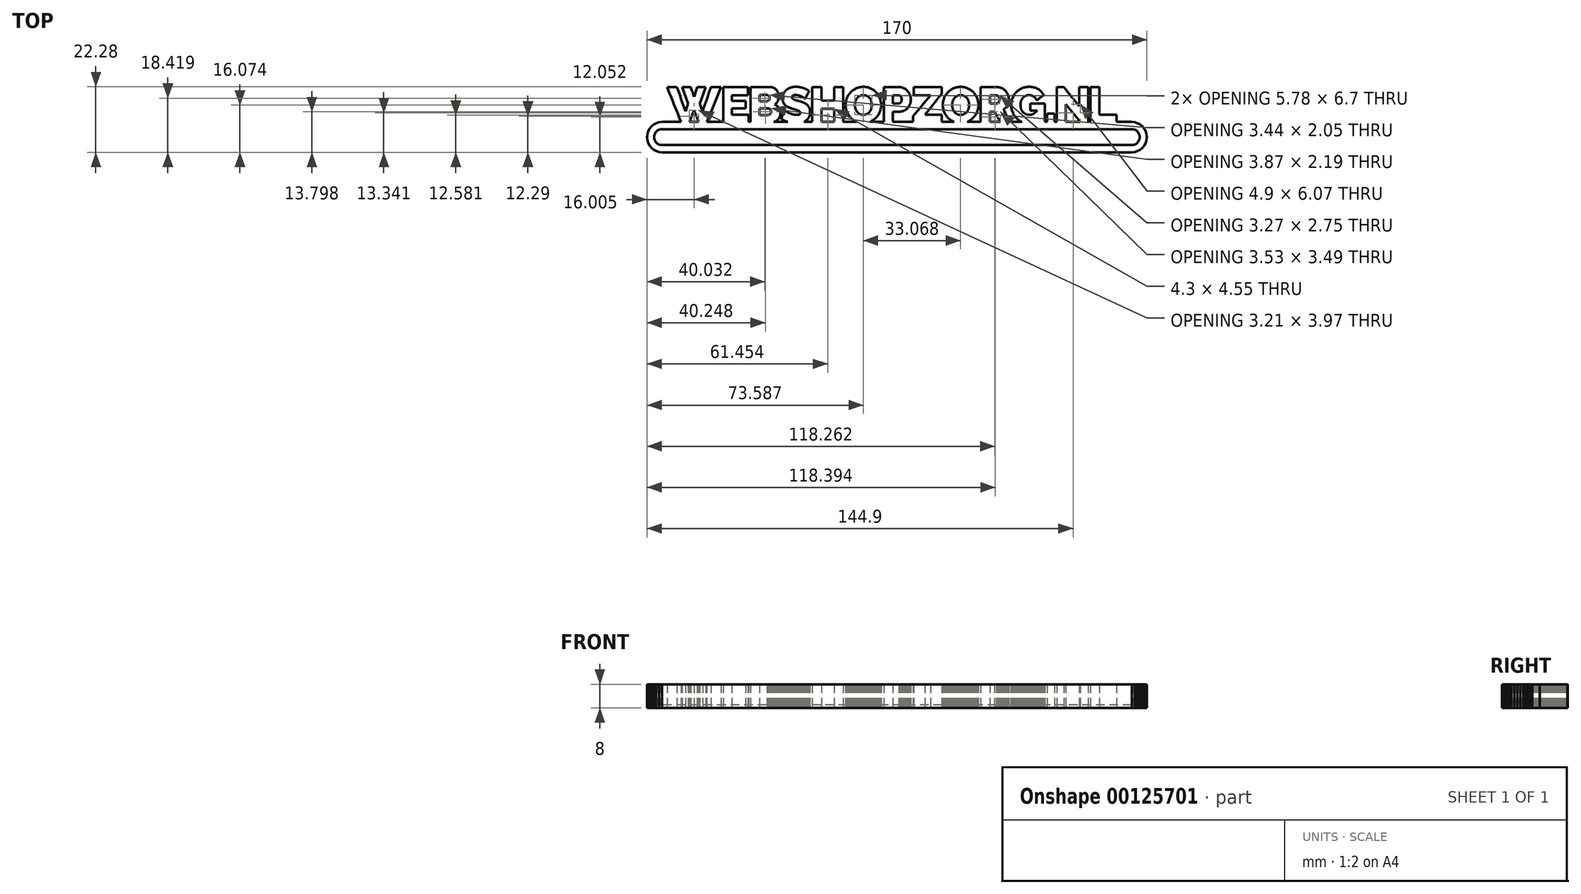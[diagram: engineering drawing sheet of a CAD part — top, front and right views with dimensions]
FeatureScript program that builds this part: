
annotation { "Feature Type Name" : "Feature", "Feature Type Description" : "" }
export const myFeature = defineFeature(function(context is Context, id is Id, definition is map)
    precondition{}
    {
        {
            var Q0;
            Q0=qCreatedBy(makeId("Top.planeOp"),FACE);
            var sketch = newSketch(context, id + "F0", { "sketchPlane" : qUnion([Q0])});
            skLineSegment(sketch, "E0", {"start": v(79.84, -0.83) * mm, "end": v(79.2, -0.83) * mm});
            skLineSegment(sketch, "E1", {"start": v(79.2, -0.83) * mm, "end": v(78.55, -0.83) * mm});
            skLineSegment(sketch, "E2", {"start": v(78.55, -0.83) * mm, "end": v(77.9, -0.83) * mm});
            skLineSegment(sketch, "E3", {"start": v(77.9, -0.83) * mm, "end": v(77.25, -0.83) * mm});
            skLineSegment(sketch, "E4", {"start": v(77.25, -0.83) * mm, "end": v(76.6, -0.83) * mm});
            skLineSegment(sketch, "E5", {"start": v(76.6, -0.83) * mm, "end": v(75.96, -0.83) * mm});
            skLineSegment(sketch, "E6", {"start": v(75.96, -0.83) * mm, "end": v(75.31, -0.83) * mm});
            skLineSegment(sketch, "E7", {"start": v(75.31, -0.83) * mm, "end": v(74.67, -0.83) * mm});
            skLineSegment(sketch, "E8", {"start": v(74.67, -0.83) * mm, "end": v(74.67, -0.53) * mm});
            skLineSegment(sketch, "E9", {"start": v(74.67, -0.53) * mm, "end": v(74.67, -0.22) * mm});
            skLineSegment(sketch, "E10", {"start": v(74.67, -0.22) * mm, "end": v(74.67, 0.1) * mm});
            skLineSegment(sketch, "E11", {"start": v(74.67, 0.1) * mm, "end": v(74.67, 0.4) * mm});
            skLineSegment(sketch, "E12", {"start": v(74.67, 0.4) * mm, "end": v(74.67, 0.7) * mm});
            skLineSegment(sketch, "E13", {"start": v(74.67, 0.7) * mm, "end": v(74.67, 1.02) * mm});
            skLineSegment(sketch, "E14", {"start": v(74.67, 1.02) * mm, "end": v(74.67, 1.33) * mm});
            skLineSegment(sketch, "E15", {"start": v(74.67, 1.33) * mm, "end": v(74.67, 1.63) * mm});
            skLineSegment(sketch, "E16", {"start": v(74.67, 1.63) * mm, "end": v(73.94, 1.63) * mm});
            skLineSegment(sketch, "E17", {"start": v(73.94, 1.63) * mm, "end": v(73.21, 1.63) * mm});
            skLineSegment(sketch, "E18", {"start": v(73.21, 1.63) * mm, "end": v(72.48, 1.63) * mm});
            skLineSegment(sketch, "E19", {"start": v(72.48, 1.63) * mm, "end": v(71.76, 1.63) * mm});
            skLineSegment(sketch, "E20", {"start": v(71.76, 1.63) * mm, "end": v(71.03, 1.63) * mm});
            skLineSegment(sketch, "E21", {"start": v(71.03, 1.63) * mm, "end": v(70.3, 1.63) * mm});
            skLineSegment(sketch, "E22", {"start": v(70.3, 1.63) * mm, "end": v(69.57, 1.63) * mm});
            skLineSegment(sketch, "E23", {"start": v(69.57, 1.63) * mm, "end": v(68.85, 1.63) * mm});
            skLineSegment(sketch, "E24", {"start": v(68.85, 1.63) * mm, "end": v(68.85, 2.8) * mm});
            skLineSegment(sketch, "E25", {"start": v(68.85, 2.8) * mm, "end": v(68.85, 3.98) * mm});
            skLineSegment(sketch, "E26", {"start": v(68.85, 3.98) * mm, "end": v(68.85, 5.15) * mm});
            skLineSegment(sketch, "E27", {"start": v(68.85, 5.15) * mm, "end": v(68.85, 6.33) * mm});
            skLineSegment(sketch, "E28", {"start": v(68.85, 6.33) * mm, "end": v(68.85, 7.5) * mm});
            skLineSegment(sketch, "E29", {"start": v(68.85, 7.5) * mm, "end": v(68.85, 8.67) * mm});
            skLineSegment(sketch, "E30", {"start": v(68.85, 8.67) * mm, "end": v(68.85, 9.85) * mm});
            skLineSegment(sketch, "E31", {"start": v(68.85, 9.85) * mm, "end": v(68.85, 11.02) * mm});
            skLineSegment(sketch, "E32", {"start": v(68.85, 11.02) * mm, "end": v(68.47, 11.02) * mm});
            skLineSegment(sketch, "E33", {"start": v(68.47, 11.02) * mm, "end": v(68.09, 11.02) * mm});
            skLineSegment(sketch, "E34", {"start": v(68.09, 11.02) * mm, "end": v(67.7, 11.02) * mm});
            skLineSegment(sketch, "E35", {"start": v(67.7, 11.02) * mm, "end": v(67.33, 11.02) * mm});
            skLineSegment(sketch, "E36", {"start": v(67.33, 11.02) * mm, "end": v(66.95, 11.02) * mm});
            skLineSegment(sketch, "E37", {"start": v(66.95, 11.02) * mm, "end": v(66.57, 11.02) * mm});
            skLineSegment(sketch, "E38", {"start": v(66.57, 11.02) * mm, "end": v(66.2, 11.02) * mm});
            skLineSegment(sketch, "E39", {"start": v(66.2, 11.02) * mm, "end": v(65.81, 11.02) * mm});
            skLineSegment(sketch, "E40", {"start": v(65.81, 11.02) * mm, "end": v(65.81, 9.54) * mm});
            skLineSegment(sketch, "E41", {"start": v(65.81, 9.54) * mm, "end": v(65.81, 8.06) * mm});
            skLineSegment(sketch, "E42", {"start": v(65.81, 8.06) * mm, "end": v(65.81, 6.57) * mm});
            skLineSegment(sketch, "E43", {"start": v(65.81, 6.57) * mm, "end": v(65.81, 5.1) * mm});
            skLineSegment(sketch, "E44", {"start": v(65.81, 5.1) * mm, "end": v(65.81, 3.61) * mm});
            skLineSegment(sketch, "E45", {"start": v(65.81, 3.61) * mm, "end": v(65.81, 2.13) * mm});
            skLineSegment(sketch, "E46", {"start": v(65.81, 2.13) * mm, "end": v(65.81, 0.65) * mm});
            skLineSegment(sketch, "E47", {"start": v(65.81, 0.65) * mm, "end": v(65.81, -0.83) * mm});
            skLineSegment(sketch, "E48", {"start": v(65.81, -0.83) * mm, "end": v(65.72, -0.83) * mm});
            skLineSegment(sketch, "E49", {"start": v(65.72, -0.83) * mm, "end": v(65.63, -0.83) * mm});
            skLineSegment(sketch, "E50", {"start": v(65.63, -0.83) * mm, "end": v(65.53, -0.83) * mm});
            skLineSegment(sketch, "E51", {"start": v(65.53, -0.83) * mm, "end": v(65.44, -0.83) * mm});
            skLineSegment(sketch, "E52", {"start": v(65.44, -0.83) * mm, "end": v(65.35, -0.83) * mm});
            skLineSegment(sketch, "E53", {"start": v(65.35, -0.83) * mm, "end": v(65.26, -0.83) * mm});
            skLineSegment(sketch, "E54", {"start": v(65.26, -0.83) * mm, "end": v(65.16, -0.83) * mm});
            skLineSegment(sketch, "E55", {"start": v(65.16, -0.83) * mm, "end": v(65.07, -0.83) * mm});
            skLineSegment(sketch, "E56", {"start": v(65.07, -0.83) * mm, "end": v(65.07, 0.65) * mm});
            skLineSegment(sketch, "E57", {"start": v(65.07, 0.65) * mm, "end": v(65.07, 2.13) * mm});
            skLineSegment(sketch, "E58", {"start": v(65.07, 2.13) * mm, "end": v(65.07, 3.61) * mm});
            skLineSegment(sketch, "E59", {"start": v(65.07, 3.61) * mm, "end": v(65.07, 5.1) * mm});
            skLineSegment(sketch, "E60", {"start": v(65.07, 5.1) * mm, "end": v(65.07, 6.57) * mm});
            skLineSegment(sketch, "E61", {"start": v(65.07, 6.57) * mm, "end": v(65.07, 8.06) * mm});
            skLineSegment(sketch, "E62", {"start": v(65.07, 8.06) * mm, "end": v(65.07, 9.54) * mm});
            skLineSegment(sketch, "E63", {"start": v(65.07, 9.54) * mm, "end": v(65.07, 11.02) * mm});
            skLineSegment(sketch, "E64", {"start": v(65.07, 11.02) * mm, "end": v(64.68, 11.02) * mm});
            skLineSegment(sketch, "E65", {"start": v(64.68, 11.02) * mm, "end": v(64.3, 11.02) * mm});
            skLineSegment(sketch, "E66", {"start": v(64.3, 11.02) * mm, "end": v(63.9, 11.02) * mm});
            skLineSegment(sketch, "E67", {"start": v(63.9, 11.02) * mm, "end": v(63.52, 11.02) * mm});
            skLineSegment(sketch, "E68", {"start": v(63.52, 11.02) * mm, "end": v(63.13, 11.02) * mm});
            skLineSegment(sketch, "E69", {"start": v(63.13, 11.02) * mm, "end": v(62.74, 11.02) * mm});
            skLineSegment(sketch, "E70", {"start": v(62.74, 11.02) * mm, "end": v(62.36, 11.02) * mm});
            skLineSegment(sketch, "E71", {"start": v(62.36, 11.02) * mm, "end": v(61.97, 11.02) * mm});
            skLineSegment(sketch, "E72", {"start": v(61.97, 11.02) * mm, "end": v(61.97, 10.2) * mm});
            skLineSegment(sketch, "E73", {"start": v(61.97, 10.2) * mm, "end": v(61.97, 9.39) * mm});
            skLineSegment(sketch, "E74", {"start": v(61.97, 9.39) * mm, "end": v(61.97, 8.57) * mm});
            skLineSegment(sketch, "E75", {"start": v(61.97, 8.57) * mm, "end": v(61.97, 7.75) * mm});
            skLineSegment(sketch, "E76", {"start": v(61.97, 7.75) * mm, "end": v(61.97, 6.94) * mm});
            skLineSegment(sketch, "E77", {"start": v(61.97, 6.94) * mm, "end": v(61.97, 6.12) * mm});
            skLineSegment(sketch, "E78", {"start": v(61.97, 6.12) * mm, "end": v(61.97, 5.3) * mm});
            skLineSegment(sketch, "E79", {"start": v(61.97, 5.3) * mm, "end": v(61.97, 4.49) * mm});
            skLineSegment(sketch, "E80", {"start": v(61.97, 4.49) * mm, "end": v(61.32, 5.3) * mm});
            skLineSegment(sketch, "E81", {"start": v(61.32, 5.3) * mm, "end": v(60.67, 6.12) * mm});
            skLineSegment(sketch, "E82", {"start": v(60.67, 6.12) * mm, "end": v(60.02, 6.94) * mm});
            skLineSegment(sketch, "E83", {"start": v(60.02, 6.94) * mm, "end": v(59.37, 7.75) * mm});
            skLineSegment(sketch, "E84", {"start": v(59.37, 7.75) * mm, "end": v(58.72, 8.57) * mm});
            skLineSegment(sketch, "E85", {"start": v(58.72, 8.57) * mm, "end": v(58.07, 9.39) * mm});
            skLineSegment(sketch, "E86", {"start": v(58.07, 9.39) * mm, "end": v(57.42, 10.2) * mm});
            skLineSegment(sketch, "E87", {"start": v(57.42, 10.2) * mm, "end": v(56.77, 11.02) * mm});
            skLineSegment(sketch, "E88", {"start": v(56.77, 11.02) * mm, "end": v(56.46, 11.02) * mm});
            skLineSegment(sketch, "E89", {"start": v(56.46, 11.02) * mm, "end": v(56.16, 11.02) * mm});
            skLineSegment(sketch, "E90", {"start": v(56.16, 11.02) * mm, "end": v(55.85, 11.02) * mm});
            skLineSegment(sketch, "E91", {"start": v(55.85, 11.02) * mm, "end": v(55.54, 11.02) * mm});
            skLineSegment(sketch, "E92", {"start": v(55.54, 11.02) * mm, "end": v(55.23, 11.02) * mm});
            skLineSegment(sketch, "E93", {"start": v(55.23, 11.02) * mm, "end": v(54.93, 11.02) * mm});
            skLineSegment(sketch, "E94", {"start": v(54.93, 11.02) * mm, "end": v(54.62, 11.02) * mm});
            skLineSegment(sketch, "E95", {"start": v(54.62, 11.02) * mm, "end": v(54.31, 11.02) * mm});
            skLineSegment(sketch, "E96", {"start": v(54.31, 11.02) * mm, "end": v(54.31, 9.54) * mm});
            skLineSegment(sketch, "E97", {"start": v(54.31, 9.54) * mm, "end": v(54.31, 8.06) * mm});
            skLineSegment(sketch, "E98", {"start": v(54.31, 8.06) * mm, "end": v(54.31, 6.57) * mm});
            skLineSegment(sketch, "E99", {"start": v(54.31, 6.57) * mm, "end": v(54.31, 5.1) * mm});
            skLineSegment(sketch, "E100", {"start": v(54.31, 5.1) * mm, "end": v(54.31, 3.61) * mm});
            skLineSegment(sketch, "E101", {"start": v(54.31, 3.61) * mm, "end": v(54.31, 2.13) * mm});
            skLineSegment(sketch, "E102", {"start": v(54.31, 2.13) * mm, "end": v(54.31, 0.65) * mm});
            skLineSegment(sketch, "E103", {"start": v(54.31, 0.65) * mm, "end": v(54.31, -0.83) * mm});
            skLineSegment(sketch, "E104", {"start": v(54.31, -0.83) * mm, "end": v(54.22, -0.83) * mm});
            skLineSegment(sketch, "E105", {"start": v(54.22, -0.83) * mm, "end": v(54.14, -0.83) * mm});
            skLineSegment(sketch, "E106", {"start": v(54.14, -0.83) * mm, "end": v(54.05, -0.83) * mm});
            skLineSegment(sketch, "E107", {"start": v(54.05, -0.83) * mm, "end": v(53.96, -0.83) * mm});
            skLineSegment(sketch, "E108", {"start": v(53.96, -0.83) * mm, "end": v(53.87, -0.83) * mm});
            skLineSegment(sketch, "E109", {"start": v(53.87, -0.83) * mm, "end": v(53.78, -0.83) * mm});
            skLineSegment(sketch, "E110", {"start": v(53.78, -0.83) * mm, "end": v(53.7, -0.83) * mm});
            skLineSegment(sketch, "E111", {"start": v(53.7, -0.83) * mm, "end": v(53.6, -0.83) * mm});
            skLineSegment(sketch, "E112", {"start": v(53.6, -0.83) * mm, "end": v(53.6, -0.48) * mm});
            skLineSegment(sketch, "E113", {"start": v(53.6, -0.48) * mm, "end": v(53.6, -0.12) * mm});
            skLineSegment(sketch, "E114", {"start": v(53.6, -0.12) * mm, "end": v(53.6, 0.24) * mm});
            skLineSegment(sketch, "E115", {"start": v(53.6, 0.24) * mm, "end": v(53.6, 0.6) * mm});
            skLineSegment(sketch, "E116", {"start": v(53.6, 0.6) * mm, "end": v(53.6, 0.95) * mm});
            skLineSegment(sketch, "E117", {"start": v(53.6, 0.95) * mm, "end": v(53.6, 1.3) * mm});
            skLineSegment(sketch, "E118", {"start": v(53.6, 1.3) * mm, "end": v(53.6, 1.67) * mm});
            skLineSegment(sketch, "E119", {"start": v(53.6, 1.67) * mm, "end": v(53.6, 2.02) * mm});
            skLineSegment(sketch, "E120", {"start": v(53.6, 2.02) * mm, "end": v(53.28, 2.02) * mm});
            skLineSegment(sketch, "E121", {"start": v(53.28, 2.02) * mm, "end": v(52.95, 2.02) * mm});
            skLineSegment(sketch, "E122", {"start": v(52.95, 2.02) * mm, "end": v(52.63, 2.02) * mm});
            skLineSegment(sketch, "E123", {"start": v(52.63, 2.02) * mm, "end": v(52.3, 2.02) * mm});
            skLineSegment(sketch, "E124", {"start": v(52.3, 2.02) * mm, "end": v(51.97, 2.02) * mm});
            skLineSegment(sketch, "E125", {"start": v(51.97, 2.02) * mm, "end": v(51.65, 2.02) * mm});
            skLineSegment(sketch, "E126", {"start": v(51.65, 2.02) * mm, "end": v(51.32, 2.02) * mm});
            skLineSegment(sketch, "E127", {"start": v(51.32, 2.02) * mm, "end": v(51, 2.02) * mm});
            skLineSegment(sketch, "E128", {"start": v(51, 2.02) * mm, "end": v(51, 1.67) * mm});
            skLineSegment(sketch, "E129", {"start": v(51, 1.67) * mm, "end": v(51, 1.3) * mm});
            skLineSegment(sketch, "E130", {"start": v(51, 1.3) * mm, "end": v(51, 0.95) * mm});
            skLineSegment(sketch, "E131", {"start": v(51, 0.95) * mm, "end": v(51, 0.6) * mm});
            skLineSegment(sketch, "E132", {"start": v(51, 0.6) * mm, "end": v(51, 0.24) * mm});
            skLineSegment(sketch, "E133", {"start": v(51, 0.24) * mm, "end": v(51, -0.12) * mm});
            skLineSegment(sketch, "E134", {"start": v(51, -0.12) * mm, "end": v(51, -0.48) * mm});
            skLineSegment(sketch, "E135", {"start": v(51, -0.48) * mm, "end": v(51, -0.83) * mm});
            skLineSegment(sketch, "E136", {"start": v(51, -0.83) * mm, "end": v(50.9, -0.83) * mm});
            skLineSegment(sketch, "E137", {"start": v(50.9, -0.83) * mm, "end": v(50.81, -0.83) * mm});
            skLineSegment(sketch, "E138", {"start": v(50.81, -0.83) * mm, "end": v(50.72, -0.83) * mm});
            skLineSegment(sketch, "E139", {"start": v(50.72, -0.83) * mm, "end": v(50.63, -0.83) * mm});
            skLineSegment(sketch, "E140", {"start": v(50.63, -0.83) * mm, "end": v(50.53, -0.83) * mm});
            skLineSegment(sketch, "E141", {"start": v(50.53, -0.83) * mm, "end": v(50.44, -0.83) * mm});
            skLineSegment(sketch, "E142", {"start": v(50.44, -0.83) * mm, "end": v(50.35, -0.83) * mm});
            skLineSegment(sketch, "E143", {"start": v(50.35, -0.83) * mm, "end": v(50.25, -0.83) * mm});
            skLineSegment(sketch, "E144", {"start": v(50.25, -0.83) * mm, "end": v(50.25, -0.05) * mm});
            skLineSegment(sketch, "E145", {"start": v(50.25, -0.05) * mm, "end": v(50.25, 0.73) * mm});
            skLineSegment(sketch, "E146", {"start": v(50.25, 0.73) * mm, "end": v(50.25, 1.5) * mm});
            skLineSegment(sketch, "E147", {"start": v(50.25, 1.5) * mm, "end": v(50.25, 2.29) * mm});
            skLineSegment(sketch, "E148", {"start": v(50.25, 2.29) * mm, "end": v(50.25, 3.07) * mm});
            skLineSegment(sketch, "E149", {"start": v(50.25, 3.07) * mm, "end": v(50.25, 3.85) * mm});
            skLineSegment(sketch, "E150", {"start": v(50.25, 3.85) * mm, "end": v(50.25, 4.63) * mm});
            skLineSegment(sketch, "E151", {"start": v(50.25, 4.63) * mm, "end": v(50.25, 5.4) * mm});
            skLineSegment(sketch, "E152", {"start": v(50.25, 5.4) * mm, "end": v(49.63, 5.4) * mm});
            skLineSegment(sketch, "E153", {"start": v(49.63, 5.4) * mm, "end": v(49.01, 5.4) * mm});
            skLineSegment(sketch, "E154", {"start": v(49.01, 5.4) * mm, "end": v(48.39, 5.4) * mm});
            skLineSegment(sketch, "E155", {"start": v(48.39, 5.4) * mm, "end": v(47.77, 5.4) * mm});
            skLineSegment(sketch, "E156", {"start": v(47.77, 5.4) * mm, "end": v(47.15, 5.4) * mm});
            skLineSegment(sketch, "E157", {"start": v(47.15, 5.4) * mm, "end": v(46.52, 5.4) * mm});
            skLineSegment(sketch, "E158", {"start": v(46.52, 5.4) * mm, "end": v(45.9, 5.4) * mm});
            skLineSegment(sketch, "E159", {"start": v(45.9, 5.4) * mm, "end": v(45.28, 5.4) * mm});
            skLineSegment(sketch, "E160", {"start": v(45.28, 5.4) * mm, "end": v(45.28, 5.1) * mm});
            skLineSegment(sketch, "E161", {"start": v(45.28, 5.1) * mm, "end": v(45.28, 4.8) * mm});
            skLineSegment(sketch, "E162", {"start": v(45.28, 4.8) * mm, "end": v(45.28, 4.5) * mm});
            skLineSegment(sketch, "E163", {"start": v(45.28, 4.5) * mm, "end": v(45.28, 4.21) * mm});
            skLineSegment(sketch, "E164", {"start": v(45.28, 4.21) * mm, "end": v(45.28, 3.91) * mm});
            skLineSegment(sketch, "E165", {"start": v(45.28, 3.91) * mm, "end": v(45.28, 3.61) * mm});
            skLineSegment(sketch, "E166", {"start": v(45.28, 3.61) * mm, "end": v(45.28, 3.31) * mm});
            skLineSegment(sketch, "E167", {"start": v(45.28, 3.31) * mm, "end": v(45.28, 3.01) * mm});
            skLineSegment(sketch, "E168", {"start": v(45.28, 3.01) * mm, "end": v(45.58, 3.01) * mm});
            skLineSegment(sketch, "E169", {"start": v(45.58, 3.01) * mm, "end": v(45.87, 3.01) * mm});
            skLineSegment(sketch, "E170", {"start": v(45.87, 3.01) * mm, "end": v(46.17, 3.01) * mm});
            skLineSegment(sketch, "E171", {"start": v(46.17, 3.01) * mm, "end": v(46.46, 3.01) * mm});
            skLineSegment(sketch, "E172", {"start": v(46.46, 3.01) * mm, "end": v(46.76, 3.01) * mm});
            skLineSegment(sketch, "E173", {"start": v(46.76, 3.01) * mm, "end": v(47.05, 3.01) * mm});
            skLineSegment(sketch, "E174", {"start": v(47.05, 3.01) * mm, "end": v(47.35, 3.01) * mm});
            skLineSegment(sketch, "E175", {"start": v(47.35, 3.01) * mm, "end": v(47.64, 3.01) * mm});
            skLineSegment(sketch, "E176", {"start": v(47.64, 3.01) * mm, "end": v(47.64, 3) * mm});
            skLineSegment(sketch, "E177", {"start": v(47.64, 3) * mm, "end": v(47.64, 3) * mm});
            skLineSegment(sketch, "E178", {"start": v(47.64, 3) * mm, "end": v(47.64, 2.99) * mm});
            skLineSegment(sketch, "E179", {"start": v(47.64, 2.99) * mm, "end": v(47.64, 2.98) * mm});
            skLineSegment(sketch, "E180", {"start": v(47.64, 2.98) * mm, "end": v(47.64, 2.97) * mm});
            skLineSegment(sketch, "E181", {"start": v(47.64, 2.97) * mm, "end": v(47.64, 2.97) * mm});
            skLineSegment(sketch, "E182", {"start": v(47.64, 2.97) * mm, "end": v(47.64, 2.96) * mm});
            skLineSegment(sketch, "E183", {"start": v(47.64, 2.96) * mm, "end": v(47.64, 2.95) * mm});
            skLineSegment(sketch, "E184", {"start": v(47.64, 2.95) * mm, "end": v(47.33, 2.63) * mm});
            skLineSegment(sketch, "E185", {"start": v(47.33, 2.63) * mm, "end": v(47, 2.36) * mm});
            skLineSegment(sketch, "E186", {"start": v(47, 2.36) * mm, "end": v(46.68, 2.12) * mm});
            skLineSegment(sketch, "E187", {"start": v(46.68, 2.12) * mm, "end": v(46.36, 1.93) * mm});
            skLineSegment(sketch, "E188", {"start": v(46.36, 1.93) * mm, "end": v(46.02, 1.79) * mm});
            skLineSegment(sketch, "E189", {"start": v(46.02, 1.79) * mm, "end": v(45.68, 1.68) * mm});
            skLineSegment(sketch, "E190", {"start": v(45.68, 1.68) * mm, "end": v(45.32, 1.62) * mm});
            skLineSegment(sketch, "E191", {"start": v(45.32, 1.62) * mm, "end": v(44.96, 1.6) * mm});
            skLineSegment(sketch, "E192", {"start": v(44.96, 1.6) * mm, "end": v(44.8, 1.6) * mm});
            skLineSegment(sketch, "E193", {"start": v(44.8, 1.6) * mm, "end": v(44.64, 1.61) * mm});
            skLineSegment(sketch, "E194", {"start": v(44.64, 1.61) * mm, "end": v(44.48, 1.63) * mm});
            skLineSegment(sketch, "E195", {"start": v(44.48, 1.63) * mm, "end": v(44.33, 1.66) * mm});
            skLineSegment(sketch, "E196", {"start": v(44.33, 1.66) * mm, "end": v(44.18, 1.7) * mm});
            skLineSegment(sketch, "E197", {"start": v(44.18, 1.7) * mm, "end": v(44.04, 1.74) * mm});
            skLineSegment(sketch, "E198", {"start": v(44.04, 1.74) * mm, "end": v(43.9, 1.79) * mm});
            skLineSegment(sketch, "E199", {"start": v(43.9, 1.79) * mm, "end": v(43.76, 1.85) * mm});
            skLineSegment(sketch, "E200", {"start": v(43.76, 1.85) * mm, "end": v(43.63, 1.91) * mm});
            skLineSegment(sketch, "E201", {"start": v(43.63, 1.91) * mm, "end": v(43.5, 1.98) * mm});
            skLineSegment(sketch, "E202", {"start": v(43.5, 1.98) * mm, "end": v(43.38, 2.06) * mm});
            skLineSegment(sketch, "E203", {"start": v(43.38, 2.06) * mm, "end": v(43.26, 2.14) * mm});
            skLineSegment(sketch, "E204", {"start": v(43.26, 2.14) * mm, "end": v(43.15, 2.23) * mm});
            skLineSegment(sketch, "E205", {"start": v(43.15, 2.23) * mm, "end": v(43.04, 2.33) * mm});
            skLineSegment(sketch, "E206", {"start": v(43.04, 2.33) * mm, "end": v(42.94, 2.43) * mm});
            skLineSegment(sketch, "E207", {"start": v(42.94, 2.43) * mm, "end": v(42.84, 2.53) * mm});
            skLineSegment(sketch, "E208", {"start": v(42.84, 2.53) * mm, "end": v(42.74, 2.65) * mm});
            skLineSegment(sketch, "E209", {"start": v(42.74, 2.65) * mm, "end": v(42.65, 2.77) * mm});
            skLineSegment(sketch, "E210", {"start": v(42.65, 2.77) * mm, "end": v(42.57, 2.9) * mm});
            skLineSegment(sketch, "E211", {"start": v(42.57, 2.9) * mm, "end": v(42.5, 3.02) * mm});
            skLineSegment(sketch, "E212", {"start": v(42.5, 3.02) * mm, "end": v(42.42, 3.16) * mm});
            skLineSegment(sketch, "E213", {"start": v(42.42, 3.16) * mm, "end": v(42.35, 3.3) * mm});
            skLineSegment(sketch, "E214", {"start": v(42.35, 3.3) * mm, "end": v(42.28, 3.44) * mm});
            skLineSegment(sketch, "E215", {"start": v(42.28, 3.44) * mm, "end": v(42.23, 3.6) * mm});
            skLineSegment(sketch, "E216", {"start": v(42.23, 3.6) * mm, "end": v(42.18, 3.75) * mm});
            skLineSegment(sketch, "E217", {"start": v(42.18, 3.75) * mm, "end": v(42.13, 3.9) * mm});
            skLineSegment(sketch, "E218", {"start": v(42.13, 3.9) * mm, "end": v(42.1, 4.07) * mm});
            skLineSegment(sketch, "E219", {"start": v(42.1, 4.07) * mm, "end": v(42.06, 4.23) * mm});
            skLineSegment(sketch, "E220", {"start": v(42.06, 4.23) * mm, "end": v(42.04, 4.4) * mm});
            skLineSegment(sketch, "E221", {"start": v(42.04, 4.4) * mm, "end": v(42.02, 4.58) * mm});
            skLineSegment(sketch, "E222", {"start": v(42.02, 4.58) * mm, "end": v(42, 4.75) * mm});
            skLineSegment(sketch, "E223", {"start": v(42, 4.75) * mm, "end": v(42, 4.93) * mm});
            skLineSegment(sketch, "E224", {"start": v(42, 4.93) * mm, "end": v(42, 5.11) * mm});
            skLineSegment(sketch, "E225", {"start": v(42, 5.11) * mm, "end": v(42.02, 5.28) * mm});
            skLineSegment(sketch, "E226", {"start": v(42.02, 5.28) * mm, "end": v(42.03, 5.46) * mm});
            skLineSegment(sketch, "E227", {"start": v(42.03, 5.46) * mm, "end": v(42.06, 5.62) * mm});
            skLineSegment(sketch, "E228", {"start": v(42.06, 5.62) * mm, "end": v(42.09, 5.79) * mm});
            skLineSegment(sketch, "E229", {"start": v(42.09, 5.79) * mm, "end": v(42.12, 5.95) * mm});
            skLineSegment(sketch, "E230", {"start": v(42.12, 5.95) * mm, "end": v(42.16, 6.1) * mm});
            skLineSegment(sketch, "E231", {"start": v(42.16, 6.1) * mm, "end": v(42.21, 6.26) * mm});
            skLineSegment(sketch, "E232", {"start": v(42.21, 6.26) * mm, "end": v(42.26, 6.42) * mm});
            skLineSegment(sketch, "E233", {"start": v(42.26, 6.42) * mm, "end": v(42.32, 6.56) * mm});
            skLineSegment(sketch, "E234", {"start": v(42.32, 6.56) * mm, "end": v(42.39, 6.7) * mm});
            skLineSegment(sketch, "E235", {"start": v(42.39, 6.7) * mm, "end": v(42.46, 6.84) * mm});
            skLineSegment(sketch, "E236", {"start": v(42.46, 6.84) * mm, "end": v(42.53, 6.97) * mm});
            skLineSegment(sketch, "E237", {"start": v(42.53, 6.97) * mm, "end": v(42.61, 7.1) * mm});
            skLineSegment(sketch, "E238", {"start": v(42.61, 7.1) * mm, "end": v(42.7, 7.22) * mm});
            skLineSegment(sketch, "E239", {"start": v(42.7, 7.22) * mm, "end": v(42.79, 7.34) * mm});
            skLineSegment(sketch, "E240", {"start": v(42.79, 7.34) * mm, "end": v(42.88, 7.45) * mm});
            skLineSegment(sketch, "E241", {"start": v(42.88, 7.45) * mm, "end": v(42.98, 7.55) * mm});
            skLineSegment(sketch, "E242", {"start": v(42.98, 7.55) * mm, "end": v(43.09, 7.65) * mm});
            skLineSegment(sketch, "E243", {"start": v(43.09, 7.65) * mm, "end": v(43.2, 7.74) * mm});
            skLineSegment(sketch, "E244", {"start": v(43.2, 7.74) * mm, "end": v(43.31, 7.83) * mm});
            skLineSegment(sketch, "E245", {"start": v(43.31, 7.83) * mm, "end": v(43.43, 7.9) * mm});
            skLineSegment(sketch, "E246", {"start": v(43.43, 7.9) * mm, "end": v(43.55, 7.98) * mm});
            skLineSegment(sketch, "E247", {"start": v(43.55, 7.98) * mm, "end": v(43.68, 8.05) * mm});
            skLineSegment(sketch, "E248", {"start": v(43.68, 8.05) * mm, "end": v(43.8, 8.1) * mm});
            skLineSegment(sketch, "E249", {"start": v(43.8, 8.1) * mm, "end": v(43.94, 8.16) * mm});
            skLineSegment(sketch, "E250", {"start": v(43.94, 8.16) * mm, "end": v(44.08, 8.2) * mm});
            skLineSegment(sketch, "E251", {"start": v(44.08, 8.2) * mm, "end": v(44.22, 8.24) * mm});
            skLineSegment(sketch, "E252", {"start": v(44.22, 8.24) * mm, "end": v(44.37, 8.27) * mm});
            skLineSegment(sketch, "E253", {"start": v(44.37, 8.27) * mm, "end": v(44.52, 8.29) * mm});
            skLineSegment(sketch, "E254", {"start": v(44.52, 8.29) * mm, "end": v(44.67, 8.3) * mm});
            skLineSegment(sketch, "E255", {"start": v(44.67, 8.3) * mm, "end": v(44.83, 8.3) * mm});
            skLineSegment(sketch, "E256", {"start": v(44.83, 8.3) * mm, "end": v(45.03, 8.3) * mm});
            skLineSegment(sketch, "E257", {"start": v(45.03, 8.3) * mm, "end": v(45.23, 8.28) * mm});
            skLineSegment(sketch, "E258", {"start": v(45.23, 8.28) * mm, "end": v(45.43, 8.24) * mm});
            skLineSegment(sketch, "E259", {"start": v(45.43, 8.24) * mm, "end": v(45.62, 8.2) * mm});
            skLineSegment(sketch, "E260", {"start": v(45.62, 8.2) * mm, "end": v(45.81, 8.14) * mm});
            skLineSegment(sketch, "E261", {"start": v(45.81, 8.14) * mm, "end": v(46, 8.07) * mm});
            skLineSegment(sketch, "E262", {"start": v(46, 8.07) * mm, "end": v(46.18, 7.99) * mm});
            skLineSegment(sketch, "E263", {"start": v(46.18, 7.99) * mm, "end": v(46.36, 7.9) * mm});
            skLineSegment(sketch, "E264", {"start": v(46.36, 7.9) * mm, "end": v(46.53, 7.78) * mm});
            skLineSegment(sketch, "E265", {"start": v(46.53, 7.78) * mm, "end": v(46.7, 7.66) * mm});
            skLineSegment(sketch, "E266", {"start": v(46.7, 7.66) * mm, "end": v(46.84, 7.54) * mm});
            skLineSegment(sketch, "E267", {"start": v(46.84, 7.54) * mm, "end": v(46.98, 7.4) * mm});
            skLineSegment(sketch, "E268", {"start": v(46.98, 7.4) * mm, "end": v(47.11, 7.25) * mm});
            skLineSegment(sketch, "E269", {"start": v(47.11, 7.25) * mm, "end": v(47.23, 7.09) * mm});
            skLineSegment(sketch, "E270", {"start": v(47.23, 7.09) * mm, "end": v(47.34, 6.92) * mm});
            skLineSegment(sketch, "E271", {"start": v(47.34, 6.92) * mm, "end": v(47.44, 6.74) * mm});
            skLineSegment(sketch, "E272", {"start": v(47.44, 6.74) * mm, "end": v(47.45, 6.7) * mm});
            skLineSegment(sketch, "E273", {"start": v(47.45, 6.7) * mm, "end": v(47.46, 6.68) * mm});
            skLineSegment(sketch, "E274", {"start": v(47.46, 6.68) * mm, "end": v(47.48, 6.66) * mm});
            skLineSegment(sketch, "E275", {"start": v(47.48, 6.66) * mm, "end": v(47.49, 6.63) * mm});
            skLineSegment(sketch, "E276", {"start": v(47.49, 6.63) * mm, "end": v(47.5, 6.6) * mm});
            skLineSegment(sketch, "E277", {"start": v(47.5, 6.6) * mm, "end": v(47.52, 6.58) * mm});
            skLineSegment(sketch, "E278", {"start": v(47.52, 6.58) * mm, "end": v(47.53, 6.55) * mm});
            skLineSegment(sketch, "E279", {"start": v(47.53, 6.55) * mm, "end": v(47.54, 6.52) * mm});
            skLineSegment(sketch, "E280", {"start": v(47.54, 6.52) * mm, "end": v(47.84, 6.75) * mm});
            skLineSegment(sketch, "E281", {"start": v(47.84, 6.75) * mm, "end": v(48.13, 6.97) * mm});
            skLineSegment(sketch, "E282", {"start": v(48.13, 6.97) * mm, "end": v(48.42, 7.19) * mm});
            skLineSegment(sketch, "E283", {"start": v(48.42, 7.19) * mm, "end": v(48.71, 7.4) * mm});
            skLineSegment(sketch, "E284", {"start": v(48.71, 7.4) * mm, "end": v(49, 7.63) * mm});
            skLineSegment(sketch, "E285", {"start": v(49, 7.63) * mm, "end": v(49.3, 7.85) * mm});
            skLineSegment(sketch, "E286", {"start": v(49.3, 7.85) * mm, "end": v(49.6, 8.07) * mm});
            skLineSegment(sketch, "E287", {"start": v(49.6, 8.07) * mm, "end": v(49.89, 8.3) * mm});
            skLineSegment(sketch, "E288", {"start": v(49.89, 8.3) * mm, "end": v(49.88, 8.31) * mm});
            skLineSegment(sketch, "E289", {"start": v(49.88, 8.31) * mm, "end": v(49.87, 8.33) * mm});
            skLineSegment(sketch, "E290", {"start": v(49.87, 8.33) * mm, "end": v(49.86, 8.35) * mm});
            skLineSegment(sketch, "E291", {"start": v(49.86, 8.35) * mm, "end": v(49.85, 8.37) * mm});
            skLineSegment(sketch, "E292", {"start": v(49.85, 8.37) * mm, "end": v(49.84, 8.39) * mm});
            skLineSegment(sketch, "E293", {"start": v(49.84, 8.39) * mm, "end": v(49.83, 8.4) * mm});
            skLineSegment(sketch, "E294", {"start": v(49.83, 8.4) * mm, "end": v(49.82, 8.42) * mm});
            skLineSegment(sketch, "E295", {"start": v(49.82, 8.42) * mm, "end": v(49.81, 8.44) * mm});
            skLineSegment(sketch, "E296", {"start": v(49.81, 8.44) * mm, "end": v(49.64, 8.74) * mm});
            skLineSegment(sketch, "E297", {"start": v(49.64, 8.74) * mm, "end": v(49.45, 9.03) * mm});
            skLineSegment(sketch, "E298", {"start": v(49.45, 9.03) * mm, "end": v(49.24, 9.3) * mm});
            skLineSegment(sketch, "E299", {"start": v(49.24, 9.3) * mm, "end": v(49.01, 9.56) * mm});
            skLineSegment(sketch, "E300", {"start": v(49.01, 9.56) * mm, "end": v(48.76, 9.8) * mm});
            skLineSegment(sketch, "E301", {"start": v(48.76, 9.8) * mm, "end": v(48.49, 10.01) * mm});
            skLineSegment(sketch, "E302", {"start": v(48.49, 10.01) * mm, "end": v(48.2, 10.22) * mm});
            skLineSegment(sketch, "E303", {"start": v(48.2, 10.22) * mm, "end": v(47.9, 10.4) * mm});
            skLineSegment(sketch, "E304", {"start": v(47.9, 10.4) * mm, "end": v(47.57, 10.57) * mm});
            skLineSegment(sketch, "E305", {"start": v(47.57, 10.57) * mm, "end": v(47.23, 10.72) * mm});
            skLineSegment(sketch, "E306", {"start": v(47.23, 10.72) * mm, "end": v(46.88, 10.84) * mm});
            skLineSegment(sketch, "E307", {"start": v(46.88, 10.84) * mm, "end": v(46.51, 10.94) * mm});
            skLineSegment(sketch, "E308", {"start": v(46.51, 10.94) * mm, "end": v(46.13, 11.02) * mm});
            skLineSegment(sketch, "E309", {"start": v(46.13, 11.02) * mm, "end": v(45.74, 11.07) * mm});
            skLineSegment(sketch, "E310", {"start": v(45.74, 11.07) * mm, "end": v(45.34, 11.1) * mm});
            skLineSegment(sketch, "E311", {"start": v(45.34, 11.1) * mm, "end": v(44.93, 11.12) * mm});
            skLineSegment(sketch, "E312", {"start": v(44.93, 11.12) * mm, "end": v(44.6, 11.11) * mm});
            skLineSegment(sketch, "E313", {"start": v(44.6, 11.11) * mm, "end": v(44.3, 11.09) * mm});
            skLineSegment(sketch, "E314", {"start": v(44.3, 11.09) * mm, "end": v(43.99, 11.05) * mm});
            skLineSegment(sketch, "E315", {"start": v(43.99, 11.05) * mm, "end": v(43.68, 11) * mm});
            skLineSegment(sketch, "E316", {"start": v(43.68, 11) * mm, "end": v(43.39, 10.93) * mm});
            skLineSegment(sketch, "E317", {"start": v(43.39, 10.93) * mm, "end": v(43.1, 10.85) * mm});
            skLineSegment(sketch, "E318", {"start": v(43.1, 10.85) * mm, "end": v(42.8, 10.75) * mm});
            skLineSegment(sketch, "E319", {"start": v(42.8, 10.75) * mm, "end": v(42.53, 10.64) * mm});
            skLineSegment(sketch, "E320", {"start": v(42.53, 10.64) * mm, "end": v(42.25, 10.51) * mm});
            skLineSegment(sketch, "E321", {"start": v(42.25, 10.51) * mm, "end": v(41.99, 10.38) * mm});
            skLineSegment(sketch, "E322", {"start": v(41.99, 10.38) * mm, "end": v(41.73, 10.23) * mm});
            skLineSegment(sketch, "E323", {"start": v(41.73, 10.23) * mm, "end": v(41.49, 10.07) * mm});
            skLineSegment(sketch, "E324", {"start": v(41.49, 10.07) * mm, "end": v(41.25, 9.9) * mm});
            skLineSegment(sketch, "E325", {"start": v(41.25, 9.9) * mm, "end": v(41.02, 9.73) * mm});
            skLineSegment(sketch, "E326", {"start": v(41.02, 9.73) * mm, "end": v(40.8, 9.54) * mm});
            skLineSegment(sketch, "E327", {"start": v(40.8, 9.54) * mm, "end": v(40.6, 9.34) * mm});
            skLineSegment(sketch, "E328", {"start": v(40.6, 9.34) * mm, "end": v(40.4, 9.13) * mm});
            skLineSegment(sketch, "E329", {"start": v(40.4, 9.13) * mm, "end": v(40.21, 8.9) * mm});
            skLineSegment(sketch, "E330", {"start": v(40.21, 8.9) * mm, "end": v(40.04, 8.68) * mm});
            skLineSegment(sketch, "E331", {"start": v(40.04, 8.68) * mm, "end": v(39.87, 8.44) * mm});
            skLineSegment(sketch, "E332", {"start": v(39.87, 8.44) * mm, "end": v(39.72, 8.2) * mm});
            skLineSegment(sketch, "E333", {"start": v(39.72, 8.2) * mm, "end": v(39.57, 7.94) * mm});
            skLineSegment(sketch, "E334", {"start": v(39.57, 7.94) * mm, "end": v(39.44, 7.67) * mm});
            skLineSegment(sketch, "E335", {"start": v(39.44, 7.67) * mm, "end": v(39.32, 7.4) * mm});
            skLineSegment(sketch, "E336", {"start": v(39.32, 7.4) * mm, "end": v(39.21, 7.12) * mm});
            skLineSegment(sketch, "E337", {"start": v(39.21, 7.12) * mm, "end": v(39.12, 6.83) * mm});
            skLineSegment(sketch, "E338", {"start": v(39.12, 6.83) * mm, "end": v(39.04, 6.54) * mm});
            skLineSegment(sketch, "E339", {"start": v(39.04, 6.54) * mm, "end": v(38.97, 6.25) * mm});
            skLineSegment(sketch, "E340", {"start": v(38.97, 6.25) * mm, "end": v(38.92, 5.95) * mm});
            skLineSegment(sketch, "E341", {"start": v(38.92, 5.95) * mm, "end": v(38.89, 5.65) * mm});
            skLineSegment(sketch, "E342", {"start": v(38.89, 5.65) * mm, "end": v(38.86, 5.34) * mm});
            skLineSegment(sketch, "E343", {"start": v(38.86, 5.34) * mm, "end": v(38.86, 5.03) * mm});
            skLineSegment(sketch, "E344", {"start": v(38.86, 5.03) * mm, "end": v(38.86, 4.7) * mm});
            skLineSegment(sketch, "E345", {"start": v(38.86, 4.7) * mm, "end": v(38.89, 4.36) * mm});
            skLineSegment(sketch, "E346", {"start": v(38.89, 4.36) * mm, "end": v(38.92, 4.03) * mm});
            skLineSegment(sketch, "E347", {"start": v(38.92, 4.03) * mm, "end": v(38.97, 3.7) * mm});
            skLineSegment(sketch, "E348", {"start": v(38.97, 3.7) * mm, "end": v(39.04, 3.4) * mm});
            skLineSegment(sketch, "E349", {"start": v(39.04, 3.4) * mm, "end": v(39.12, 3.09) * mm});
            skLineSegment(sketch, "E350", {"start": v(39.12, 3.09) * mm, "end": v(39.21, 2.79) * mm});
            skLineSegment(sketch, "E351", {"start": v(39.21, 2.79) * mm, "end": v(39.32, 2.5) * mm});
            skLineSegment(sketch, "E352", {"start": v(39.32, 2.5) * mm, "end": v(39.44, 2.21) * mm});
            skLineSegment(sketch, "E353", {"start": v(39.44, 2.21) * mm, "end": v(39.57, 1.94) * mm});
            skLineSegment(sketch, "E354", {"start": v(39.57, 1.94) * mm, "end": v(39.71, 1.68) * mm});
            skLineSegment(sketch, "E355", {"start": v(39.71, 1.68) * mm, "end": v(39.87, 1.42) * mm});
            skLineSegment(sketch, "E356", {"start": v(39.87, 1.42) * mm, "end": v(40.03, 1.18) * mm});
            skLineSegment(sketch, "E357", {"start": v(40.03, 1.18) * mm, "end": v(40.2, 0.95) * mm});
            skLineSegment(sketch, "E358", {"start": v(40.2, 0.95) * mm, "end": v(40.39, 0.73) * mm});
            skLineSegment(sketch, "E359", {"start": v(40.39, 0.73) * mm, "end": v(40.58, 0.52) * mm});
            skLineSegment(sketch, "E360", {"start": v(40.58, 0.52) * mm, "end": v(40.78, 0.32) * mm});
            skLineSegment(sketch, "E361", {"start": v(40.78, 0.32) * mm, "end": v(41, 0.13) * mm});
            skLineSegment(sketch, "E362", {"start": v(41, 0.13) * mm, "end": v(41.22, -0.05) * mm});
            skLineSegment(sketch, "E363", {"start": v(41.22, -0.05) * mm, "end": v(41.45, -0.22) * mm});
            skLineSegment(sketch, "E364", {"start": v(41.45, -0.22) * mm, "end": v(41.68, -0.38) * mm});
            skLineSegment(sketch, "E365", {"start": v(41.68, -0.38) * mm, "end": v(41.93, -0.52) * mm});
            skLineSegment(sketch, "E366", {"start": v(41.93, -0.52) * mm, "end": v(42.18, -0.66) * mm});
            skLineSegment(sketch, "E367", {"start": v(42.18, -0.66) * mm, "end": v(42.44, -0.78) * mm});
            skLineSegment(sketch, "E368", {"start": v(42.44, -0.78) * mm, "end": v(42.46, -0.78) * mm});
            skLineSegment(sketch, "E369", {"start": v(42.46, -0.78) * mm, "end": v(42.47, -0.8) * mm});
            skLineSegment(sketch, "E370", {"start": v(42.47, -0.8) * mm, "end": v(42.49, -0.8) * mm});
            skLineSegment(sketch, "E371", {"start": v(42.49, -0.8) * mm, "end": v(42.5, -0.81) * mm});
            skLineSegment(sketch, "E372", {"start": v(42.5, -0.81) * mm, "end": v(42.51, -0.82) * mm});
            skLineSegment(sketch, "E373", {"start": v(42.51, -0.82) * mm, "end": v(42.53, -0.83) * mm});
            skLineSegment(sketch, "E374", {"start": v(42.53, -0.83) * mm, "end": v(42.54, -0.83) * mm});
            skLineSegment(sketch, "E375", {"start": v(42.54, -0.83) * mm, "end": v(42.56, -0.83) * mm});
            skLineSegment(sketch, "E376", {"start": v(42.56, -0.83) * mm, "end": v(42.07, -0.83) * mm});
            skLineSegment(sketch, "E377", {"start": v(42.07, -0.83) * mm, "end": v(41.59, -0.83) * mm});
            skLineSegment(sketch, "E378", {"start": v(41.59, -0.83) * mm, "end": v(41.1, -0.83) * mm});
            skLineSegment(sketch, "E379", {"start": v(41.1, -0.83) * mm, "end": v(40.62, -0.83) * mm});
            skLineSegment(sketch, "E380", {"start": v(40.62, -0.83) * mm, "end": v(40.14, -0.83) * mm});
            skLineSegment(sketch, "E381", {"start": v(40.14, -0.83) * mm, "end": v(39.65, -0.83) * mm});
            skLineSegment(sketch, "E382", {"start": v(39.65, -0.83) * mm, "end": v(39.17, -0.83) * mm});
            skLineSegment(sketch, "E383", {"start": v(39.17, -0.83) * mm, "end": v(38.69, -0.83) * mm});
            skLineSegment(sketch, "E384", {"start": v(38.69, -0.83) * mm, "end": v(38.38, -0.3) * mm});
            skLineSegment(sketch, "E385", {"start": v(38.38, -0.3) * mm, "end": v(38.07, 0.22) * mm});
            skLineSegment(sketch, "E386", {"start": v(38.07, 0.22) * mm, "end": v(37.76, 0.74) * mm});
            skLineSegment(sketch, "E387", {"start": v(37.76, 0.74) * mm, "end": v(37.45, 1.27) * mm});
            skLineSegment(sketch, "E388", {"start": v(37.45, 1.27) * mm, "end": v(37.14, 1.8) * mm});
            skLineSegment(sketch, "E389", {"start": v(37.14, 1.8) * mm, "end": v(36.83, 2.32) * mm});
            skLineSegment(sketch, "E390", {"start": v(36.83, 2.32) * mm, "end": v(36.52, 2.84) * mm});
            skLineSegment(sketch, "E391", {"start": v(36.52, 2.84) * mm, "end": v(36.2, 3.37) * mm});
            skLineSegment(sketch, "E392", {"start": v(36.2, 3.37) * mm, "end": v(36.3, 3.42) * mm});
            skLineSegment(sketch, "E393", {"start": v(36.3, 3.42) * mm, "end": v(36.39, 3.49) * mm});
            skLineSegment(sketch, "E394", {"start": v(36.39, 3.49) * mm, "end": v(36.48, 3.55) * mm});
            skLineSegment(sketch, "E395", {"start": v(36.48, 3.55) * mm, "end": v(36.56, 3.62) * mm});
            skLineSegment(sketch, "E396", {"start": v(36.56, 3.62) * mm, "end": v(36.65, 3.68) * mm});
            skLineSegment(sketch, "E397", {"start": v(36.65, 3.68) * mm, "end": v(36.73, 3.76) * mm});
            skLineSegment(sketch, "E398", {"start": v(36.73, 3.76) * mm, "end": v(36.8, 3.83) * mm});
            skLineSegment(sketch, "E399", {"start": v(36.8, 3.83) * mm, "end": v(36.88, 3.9) * mm});
            skLineSegment(sketch, "E400", {"start": v(36.88, 3.9) * mm, "end": v(36.98, 4) * mm});
            skLineSegment(sketch, "E401", {"start": v(36.98, 4) * mm, "end": v(37.06, 4.1) * mm});
            skLineSegment(sketch, "E402", {"start": v(37.06, 4.1) * mm, "end": v(37.15, 4.2) * mm});
            skLineSegment(sketch, "E403", {"start": v(37.15, 4.2) * mm, "end": v(37.23, 4.3) * mm});
            skLineSegment(sketch, "E404", {"start": v(37.23, 4.3) * mm, "end": v(37.3, 4.41) * mm});
            skLineSegment(sketch, "E405", {"start": v(37.3, 4.41) * mm, "end": v(37.38, 4.52) * mm});
            skLineSegment(sketch, "E406", {"start": v(37.38, 4.52) * mm, "end": v(37.45, 4.64) * mm});
            skLineSegment(sketch, "E407", {"start": v(37.45, 4.64) * mm, "end": v(37.52, 4.75) * mm});
            skLineSegment(sketch, "E408", {"start": v(37.52, 4.75) * mm, "end": v(37.58, 4.87) * mm});
            skLineSegment(sketch, "E409", {"start": v(37.58, 4.87) * mm, "end": v(37.64, 5) * mm});
            skLineSegment(sketch, "E410", {"start": v(37.64, 5) * mm, "end": v(37.7, 5.11) * mm});
            skLineSegment(sketch, "E411", {"start": v(37.7, 5.11) * mm, "end": v(37.75, 5.24) * mm});
            skLineSegment(sketch, "E412", {"start": v(37.75, 5.24) * mm, "end": v(37.8, 5.36) * mm});
            skLineSegment(sketch, "E413", {"start": v(37.8, 5.36) * mm, "end": v(37.84, 5.5) * mm});
            skLineSegment(sketch, "E414", {"start": v(37.84, 5.5) * mm, "end": v(37.88, 5.62) * mm});
            skLineSegment(sketch, "E415", {"start": v(37.88, 5.62) * mm, "end": v(37.92, 5.75) * mm});
            skLineSegment(sketch, "E416", {"start": v(37.92, 5.75) * mm, "end": v(37.95, 5.89) * mm});
            skLineSegment(sketch, "E417", {"start": v(37.95, 5.89) * mm, "end": v(37.98, 6.02) * mm});
            skLineSegment(sketch, "E418", {"start": v(37.98, 6.02) * mm, "end": v(38, 6.16) * mm});
            skLineSegment(sketch, "E419", {"start": v(38, 6.16) * mm, "end": v(38.03, 6.3) * mm});
            skLineSegment(sketch, "E420", {"start": v(38.03, 6.3) * mm, "end": v(38.04, 6.43) * mm});
            skLineSegment(sketch, "E421", {"start": v(38.04, 6.43) * mm, "end": v(38.05, 6.57) * mm});
            skLineSegment(sketch, "E422", {"start": v(38.05, 6.57) * mm, "end": v(38.06, 6.72) * mm});
            skLineSegment(sketch, "E423", {"start": v(38.06, 6.72) * mm, "end": v(38.06, 6.86) * mm});
            skLineSegment(sketch, "E424", {"start": v(38.06, 6.86) * mm, "end": v(38.06, 7.05) * mm});
            skLineSegment(sketch, "E425", {"start": v(38.06, 7.05) * mm, "end": v(38.04, 7.24) * mm});
            skLineSegment(sketch, "E426", {"start": v(38.04, 7.24) * mm, "end": v(38.02, 7.43) * mm});
            skLineSegment(sketch, "E427", {"start": v(38.02, 7.43) * mm, "end": v(37.98, 7.62) * mm});
            skLineSegment(sketch, "E428", {"start": v(37.98, 7.62) * mm, "end": v(37.94, 7.81) * mm});
            skLineSegment(sketch, "E429", {"start": v(37.94, 7.81) * mm, "end": v(37.89, 8) * mm});
            skLineSegment(sketch, "E430", {"start": v(37.89, 8) * mm, "end": v(37.83, 8.19) * mm});
            skLineSegment(sketch, "E431", {"start": v(37.83, 8.19) * mm, "end": v(37.76, 8.38) * mm});
            skLineSegment(sketch, "E432", {"start": v(37.76, 8.38) * mm, "end": v(37.68, 8.56) * mm});
            skLineSegment(sketch, "E433", {"start": v(37.68, 8.56) * mm, "end": v(37.59, 8.74) * mm});
            skLineSegment(sketch, "E434", {"start": v(37.59, 8.74) * mm, "end": v(37.5, 8.91) * mm});
            skLineSegment(sketch, "E435", {"start": v(37.5, 8.91) * mm, "end": v(37.4, 9.08) * mm});
            skLineSegment(sketch, "E436", {"start": v(37.4, 9.08) * mm, "end": v(37.28, 9.25) * mm});
            skLineSegment(sketch, "E437", {"start": v(37.28, 9.25) * mm, "end": v(37.17, 9.4) * mm});
            skLineSegment(sketch, "E438", {"start": v(37.17, 9.4) * mm, "end": v(37.04, 9.56) * mm});
            skLineSegment(sketch, "E439", {"start": v(37.04, 9.56) * mm, "end": v(36.91, 9.71) * mm});
            skLineSegment(sketch, "E440", {"start": v(36.91, 9.71) * mm, "end": v(36.78, 9.86) * mm});
            skLineSegment(sketch, "E441", {"start": v(36.78, 9.86) * mm, "end": v(36.63, 10) * mm});
            skLineSegment(sketch, "E442", {"start": v(36.63, 10) * mm, "end": v(36.48, 10.12) * mm});
            skLineSegment(sketch, "E443", {"start": v(36.48, 10.12) * mm, "end": v(36.32, 10.24) * mm});
            skLineSegment(sketch, "E444", {"start": v(36.32, 10.24) * mm, "end": v(36.16, 10.36) * mm});
            skLineSegment(sketch, "E445", {"start": v(36.16, 10.36) * mm, "end": v(36, 10.46) * mm});
            skLineSegment(sketch, "E446", {"start": v(36, 10.46) * mm, "end": v(35.82, 10.57) * mm});
            skLineSegment(sketch, "E447", {"start": v(35.82, 10.57) * mm, "end": v(35.64, 10.66) * mm});
            skLineSegment(sketch, "E448", {"start": v(35.64, 10.66) * mm, "end": v(35.45, 10.74) * mm});
            skLineSegment(sketch, "E449", {"start": v(35.45, 10.74) * mm, "end": v(35.26, 10.82) * mm});
            skLineSegment(sketch, "E450", {"start": v(35.26, 10.82) * mm, "end": v(35.06, 10.88) * mm});
            skLineSegment(sketch, "E451", {"start": v(35.06, 10.88) * mm, "end": v(34.86, 10.93) * mm});
            skLineSegment(sketch, "E452", {"start": v(34.86, 10.93) * mm, "end": v(34.65, 10.97) * mm});
            skLineSegment(sketch, "E453", {"start": v(34.65, 10.97) * mm, "end": v(34.44, 11) * mm});
            skLineSegment(sketch, "E454", {"start": v(34.44, 11) * mm, "end": v(34.23, 11.01) * mm});
            skLineSegment(sketch, "E455", {"start": v(34.23, 11.01) * mm, "end": v(34.01, 11.02) * mm});
            skLineSegment(sketch, "E456", {"start": v(34.01, 11.02) * mm, "end": v(33.32, 11.02) * mm});
            skLineSegment(sketch, "E457", {"start": v(33.32, 11.02) * mm, "end": v(32.63, 11.02) * mm});
            skLineSegment(sketch, "E458", {"start": v(32.63, 11.02) * mm, "end": v(31.94, 11.02) * mm});
            skLineSegment(sketch, "E459", {"start": v(31.94, 11.02) * mm, "end": v(31.25, 11.02) * mm});
            skLineSegment(sketch, "E460", {"start": v(31.25, 11.02) * mm, "end": v(30.56, 11.02) * mm});
            skLineSegment(sketch, "E461", {"start": v(30.56, 11.02) * mm, "end": v(29.87, 11.02) * mm});
            skLineSegment(sketch, "E462", {"start": v(29.87, 11.02) * mm, "end": v(29.18, 11.02) * mm});
            skLineSegment(sketch, "E463", {"start": v(29.18, 11.02) * mm, "end": v(28.49, 11.02) * mm});
            skLineSegment(sketch, "E464", {"start": v(28.49, 11.02) * mm, "end": v(28.49, 9.54) * mm});
            skLineSegment(sketch, "E465", {"start": v(28.49, 9.54) * mm, "end": v(28.49, 8.06) * mm});
            skLineSegment(sketch, "E466", {"start": v(28.49, 8.06) * mm, "end": v(28.49, 6.57) * mm});
            skLineSegment(sketch, "E467", {"start": v(28.49, 6.57) * mm, "end": v(28.49, 5.1) * mm});
            skLineSegment(sketch, "E468", {"start": v(28.49, 5.1) * mm, "end": v(28.49, 3.61) * mm});
            skLineSegment(sketch, "E469", {"start": v(28.49, 3.61) * mm, "end": v(28.49, 2.13) * mm});
            skLineSegment(sketch, "E470", {"start": v(28.49, 2.13) * mm, "end": v(28.49, 0.65) * mm});
            skLineSegment(sketch, "E471", {"start": v(28.49, 0.65) * mm, "end": v(28.49, -0.83) * mm});
            skLineSegment(sketch, "E472", {"start": v(28.49, -0.83) * mm, "end": v(27.91, -0.83) * mm});
            skLineSegment(sketch, "E473", {"start": v(27.91, -0.83) * mm, "end": v(27.33, -0.83) * mm});
            skLineSegment(sketch, "E474", {"start": v(27.33, -0.83) * mm, "end": v(26.76, -0.83) * mm});
            skLineSegment(sketch, "E475", {"start": v(26.76, -0.83) * mm, "end": v(26.18, -0.83) * mm});
            skLineSegment(sketch, "E476", {"start": v(26.18, -0.83) * mm, "end": v(25.6, -0.83) * mm});
            skLineSegment(sketch, "E477", {"start": v(25.6, -0.83) * mm, "end": v(25.02, -0.83) * mm});
            skLineSegment(sketch, "E478", {"start": v(25.02, -0.83) * mm, "end": v(24.45, -0.83) * mm});
            skLineSegment(sketch, "E479", {"start": v(24.45, -0.83) * mm, "end": v(23.87, -0.83) * mm});
            skLineSegment(sketch, "E480", {"start": v(23.87, -0.83) * mm, "end": v(23.9, -0.82) * mm});
            skLineSegment(sketch, "E481", {"start": v(23.9, -0.82) * mm, "end": v(23.92, -0.8) * mm});
            skLineSegment(sketch, "E482", {"start": v(23.92, -0.8) * mm, "end": v(23.95, -0.8) * mm});
            skLineSegment(sketch, "E483", {"start": v(23.95, -0.8) * mm, "end": v(23.97, -0.78) * mm});
            skLineSegment(sketch, "E484", {"start": v(23.97, -0.78) * mm, "end": v(24, -0.77) * mm});
            skLineSegment(sketch, "E485", {"start": v(24, -0.77) * mm, "end": v(24.02, -0.76) * mm});
            skLineSegment(sketch, "E486", {"start": v(24.02, -0.76) * mm, "end": v(24.05, -0.74) * mm});
            skLineSegment(sketch, "E487", {"start": v(24.05, -0.74) * mm, "end": v(24.08, -0.73) * mm});
            skLineSegment(sketch, "E488", {"start": v(24.08, -0.73) * mm, "end": v(24.35, -0.6) * mm});
            skLineSegment(sketch, "E489", {"start": v(24.35, -0.6) * mm, "end": v(24.61, -0.45) * mm});
            skLineSegment(sketch, "E490", {"start": v(24.61, -0.45) * mm, "end": v(24.87, -0.3) * mm});
            skLineSegment(sketch, "E491", {"start": v(24.87, -0.3) * mm, "end": v(25.11, -0.13) * mm});
            skLineSegment(sketch, "E492", {"start": v(25.11, -0.13) * mm, "end": v(25.35, 0.05) * mm});
            skLineSegment(sketch, "E493", {"start": v(25.35, 0.05) * mm, "end": v(25.57, 0.23) * mm});
            skLineSegment(sketch, "E494", {"start": v(25.57, 0.23) * mm, "end": v(25.79, 0.43) * mm});
            skLineSegment(sketch, "E495", {"start": v(25.79, 0.43) * mm, "end": v(26, 0.64) * mm});
            skLineSegment(sketch, "E496", {"start": v(26, 0.64) * mm, "end": v(26.2, 0.85) * mm});
            skLineSegment(sketch, "E497", {"start": v(26.2, 0.85) * mm, "end": v(26.37, 1.08) * mm});
            skLineSegment(sketch, "E498", {"start": v(26.37, 1.08) * mm, "end": v(26.55, 1.31) * mm});
            skLineSegment(sketch, "E499", {"start": v(26.55, 1.31) * mm, "end": v(26.71, 1.55) * mm});
            skLineSegment(sketch, "E500", {"start": v(26.71, 1.55) * mm, "end": v(26.86, 1.8) * mm});
            skLineSegment(sketch, "E501", {"start": v(26.86, 1.8) * mm, "end": v(27, 2.06) * mm});
            skLineSegment(sketch, "E502", {"start": v(27, 2.06) * mm, "end": v(27.13, 2.33) * mm});
            skLineSegment(sketch, "E503", {"start": v(27.13, 2.33) * mm, "end": v(27.25, 2.6) * mm});
            skLineSegment(sketch, "E504", {"start": v(27.25, 2.6) * mm, "end": v(27.36, 2.88) * mm});
            skLineSegment(sketch, "E505", {"start": v(27.36, 2.88) * mm, "end": v(27.45, 3.16) * mm});
            skLineSegment(sketch, "E506", {"start": v(27.45, 3.16) * mm, "end": v(27.53, 3.45) * mm});
            skLineSegment(sketch, "E507", {"start": v(27.53, 3.45) * mm, "end": v(27.6, 3.74) * mm});
            skLineSegment(sketch, "E508", {"start": v(27.6, 3.74) * mm, "end": v(27.64, 4.03) * mm});
            skLineSegment(sketch, "E509", {"start": v(27.64, 4.03) * mm, "end": v(27.68, 4.32) * mm});
            skLineSegment(sketch, "E510", {"start": v(27.68, 4.32) * mm, "end": v(27.7, 4.62) * mm});
            skLineSegment(sketch, "E511", {"start": v(27.7, 4.62) * mm, "end": v(27.7, 4.92) * mm});
            skLineSegment(sketch, "E512", {"start": v(27.7, 4.92) * mm, "end": v(27.7, 5.2) * mm});
            skLineSegment(sketch, "E513", {"start": v(27.7, 5.2) * mm, "end": v(27.68, 5.49) * mm});
            skLineSegment(sketch, "E514", {"start": v(27.68, 5.49) * mm, "end": v(27.65, 5.77) * mm});
            skLineSegment(sketch, "E515", {"start": v(27.65, 5.77) * mm, "end": v(27.6, 6.06) * mm});
            skLineSegment(sketch, "E516", {"start": v(27.6, 6.06) * mm, "end": v(27.54, 6.34) * mm});
            skLineSegment(sketch, "E517", {"start": v(27.54, 6.34) * mm, "end": v(27.47, 6.62) * mm});
            skLineSegment(sketch, "E518", {"start": v(27.47, 6.62) * mm, "end": v(27.38, 6.9) * mm});
            skLineSegment(sketch, "E519", {"start": v(27.38, 6.9) * mm, "end": v(27.28, 7.18) * mm});
            skLineSegment(sketch, "E520", {"start": v(27.28, 7.18) * mm, "end": v(27.17, 7.45) * mm});
            skLineSegment(sketch, "E521", {"start": v(27.17, 7.45) * mm, "end": v(27.04, 7.72) * mm});
            skLineSegment(sketch, "E522", {"start": v(27.04, 7.72) * mm, "end": v(26.9, 7.98) * mm});
            skLineSegment(sketch, "E523", {"start": v(26.9, 7.98) * mm, "end": v(26.76, 8.23) * mm});
            skLineSegment(sketch, "E524", {"start": v(26.76, 8.23) * mm, "end": v(26.6, 8.47) * mm});
            skLineSegment(sketch, "E525", {"start": v(26.6, 8.47) * mm, "end": v(26.43, 8.71) * mm});
            skLineSegment(sketch, "E526", {"start": v(26.43, 8.71) * mm, "end": v(26.26, 8.94) * mm});
            skLineSegment(sketch, "E527", {"start": v(26.26, 8.94) * mm, "end": v(26.06, 9.16) * mm});
            skLineSegment(sketch, "E528", {"start": v(26.06, 9.16) * mm, "end": v(25.86, 9.38) * mm});
            skLineSegment(sketch, "E529", {"start": v(25.86, 9.38) * mm, "end": v(25.65, 9.58) * mm});
            skLineSegment(sketch, "E530", {"start": v(25.65, 9.58) * mm, "end": v(25.43, 9.77) * mm});
            skLineSegment(sketch, "E531", {"start": v(25.43, 9.77) * mm, "end": v(25.2, 9.95) * mm});
            skLineSegment(sketch, "E532", {"start": v(25.2, 9.95) * mm, "end": v(24.95, 10.12) * mm});
            skLineSegment(sketch, "E533", {"start": v(24.95, 10.12) * mm, "end": v(24.7, 10.28) * mm});
            skLineSegment(sketch, "E534", {"start": v(24.7, 10.28) * mm, "end": v(24.43, 10.43) * mm});
            skLineSegment(sketch, "E535", {"start": v(24.43, 10.43) * mm, "end": v(24.16, 10.57) * mm});
            skLineSegment(sketch, "E536", {"start": v(24.16, 10.57) * mm, "end": v(23.88, 10.7) * mm});
            skLineSegment(sketch, "E537", {"start": v(23.88, 10.7) * mm, "end": v(23.59, 10.8) * mm});
            skLineSegment(sketch, "E538", {"start": v(23.59, 10.8) * mm, "end": v(23.29, 10.9) * mm});
            skLineSegment(sketch, "E539", {"start": v(23.29, 10.9) * mm, "end": v(22.98, 10.97) * mm});
            skLineSegment(sketch, "E540", {"start": v(22.98, 10.97) * mm, "end": v(22.67, 11.03) * mm});
            skLineSegment(sketch, "E541", {"start": v(22.67, 11.03) * mm, "end": v(22.35, 11.07) * mm});
            skLineSegment(sketch, "E542", {"start": v(22.35, 11.07) * mm, "end": v(22.02, 11.1) * mm});
            skLineSegment(sketch, "E543", {"start": v(22.02, 11.1) * mm, "end": v(21.69, 11.1) * mm});
            skLineSegment(sketch, "E544", {"start": v(21.69, 11.1) * mm, "end": v(21.36, 11.1) * mm});
            skLineSegment(sketch, "E545", {"start": v(21.36, 11.1) * mm, "end": v(21.04, 11.07) * mm});
            skLineSegment(sketch, "E546", {"start": v(21.04, 11.07) * mm, "end": v(20.73, 11.03) * mm});
            skLineSegment(sketch, "E547", {"start": v(20.73, 11.03) * mm, "end": v(20.42, 10.98) * mm});
            skLineSegment(sketch, "E548", {"start": v(20.42, 10.98) * mm, "end": v(20.12, 10.9) * mm});
            skLineSegment(sketch, "E549", {"start": v(20.12, 10.9) * mm, "end": v(19.82, 10.82) * mm});
            skLineSegment(sketch, "E550", {"start": v(19.82, 10.82) * mm, "end": v(19.53, 10.71) * mm});
            skLineSegment(sketch, "E551", {"start": v(19.53, 10.71) * mm, "end": v(19.25, 10.6) * mm});
            skLineSegment(sketch, "E552", {"start": v(19.25, 10.6) * mm, "end": v(18.98, 10.46) * mm});
            skLineSegment(sketch, "E553", {"start": v(18.98, 10.46) * mm, "end": v(18.71, 10.32) * mm});
            skLineSegment(sketch, "E554", {"start": v(18.71, 10.32) * mm, "end": v(18.46, 10.17) * mm});
            skLineSegment(sketch, "E555", {"start": v(18.46, 10.17) * mm, "end": v(18.21, 10) * mm});
            skLineSegment(sketch, "E556", {"start": v(18.21, 10) * mm, "end": v(17.98, 9.83) * mm});
            skLineSegment(sketch, "E557", {"start": v(17.98, 9.83) * mm, "end": v(17.75, 9.64) * mm});
            skLineSegment(sketch, "E558", {"start": v(17.75, 9.64) * mm, "end": v(17.53, 9.45) * mm});
            skLineSegment(sketch, "E559", {"start": v(17.53, 9.45) * mm, "end": v(17.32, 9.24) * mm});
            skLineSegment(sketch, "E560", {"start": v(17.32, 9.24) * mm, "end": v(17.13, 9.03) * mm});
            skLineSegment(sketch, "E561", {"start": v(17.13, 9.03) * mm, "end": v(16.94, 8.8) * mm});
            skLineSegment(sketch, "E562", {"start": v(16.94, 8.8) * mm, "end": v(16.77, 8.57) * mm});
            skLineSegment(sketch, "E563", {"start": v(16.77, 8.57) * mm, "end": v(16.6, 8.33) * mm});
            skLineSegment(sketch, "E564", {"start": v(16.6, 8.33) * mm, "end": v(16.45, 8.08) * mm});
            skLineSegment(sketch, "E565", {"start": v(16.45, 8.08) * mm, "end": v(16.3, 7.82) * mm});
            skLineSegment(sketch, "E566", {"start": v(16.3, 7.82) * mm, "end": v(16.18, 7.55) * mm});
            skLineSegment(sketch, "E567", {"start": v(16.18, 7.55) * mm, "end": v(16.06, 7.28) * mm});
            skLineSegment(sketch, "E568", {"start": v(16.06, 7.28) * mm, "end": v(15.95, 7) * mm});
            skLineSegment(sketch, "E569", {"start": v(15.95, 7) * mm, "end": v(15.86, 6.72) * mm});
            skLineSegment(sketch, "E570", {"start": v(15.86, 6.72) * mm, "end": v(15.78, 6.43) * mm});
            skLineSegment(sketch, "E571", {"start": v(15.78, 6.43) * mm, "end": v(15.72, 6.15) * mm});
            skLineSegment(sketch, "E572", {"start": v(15.72, 6.15) * mm, "end": v(15.67, 5.85) * mm});
            skLineSegment(sketch, "E573", {"start": v(15.67, 5.85) * mm, "end": v(15.63, 5.56) * mm});
            skLineSegment(sketch, "E574", {"start": v(15.63, 5.56) * mm, "end": v(15.6, 5.26) * mm});
            skLineSegment(sketch, "E575", {"start": v(15.6, 5.26) * mm, "end": v(15.6, 4.97) * mm});
            skLineSegment(sketch, "E576", {"start": v(15.6, 4.97) * mm, "end": v(15.6, 4.67) * mm});
            skLineSegment(sketch, "E577", {"start": v(15.6, 4.67) * mm, "end": v(15.63, 4.38) * mm});
            skLineSegment(sketch, "E578", {"start": v(15.63, 4.38) * mm, "end": v(15.66, 4.1) * mm});
            skLineSegment(sketch, "E579", {"start": v(15.66, 4.1) * mm, "end": v(15.71, 3.8) * mm});
            skLineSegment(sketch, "E580", {"start": v(15.71, 3.8) * mm, "end": v(15.77, 3.52) * mm});
            skLineSegment(sketch, "E581", {"start": v(15.77, 3.52) * mm, "end": v(15.85, 3.23) * mm});
            skLineSegment(sketch, "E582", {"start": v(15.85, 3.23) * mm, "end": v(15.94, 2.95) * mm});
            skLineSegment(sketch, "E583", {"start": v(15.94, 2.95) * mm, "end": v(16.04, 2.67) * mm});
            skLineSegment(sketch, "E584", {"start": v(16.04, 2.67) * mm, "end": v(16.15, 2.4) * mm});
            skLineSegment(sketch, "E585", {"start": v(16.15, 2.4) * mm, "end": v(16.28, 2.13) * mm});
            skLineSegment(sketch, "E586", {"start": v(16.28, 2.13) * mm, "end": v(16.41, 1.87) * mm});
            skLineSegment(sketch, "E587", {"start": v(16.41, 1.87) * mm, "end": v(16.56, 1.62) * mm});
            skLineSegment(sketch, "E588", {"start": v(16.56, 1.62) * mm, "end": v(16.72, 1.38) * mm});
            skLineSegment(sketch, "E589", {"start": v(16.72, 1.38) * mm, "end": v(16.9, 1.14) * mm});
            skLineSegment(sketch, "E590", {"start": v(16.9, 1.14) * mm, "end": v(17.07, 0.92) * mm});
            skLineSegment(sketch, "E591", {"start": v(17.07, 0.92) * mm, "end": v(17.26, 0.7) * mm});
            skLineSegment(sketch, "E592", {"start": v(17.26, 0.7) * mm, "end": v(17.46, 0.48) * mm});
            skLineSegment(sketch, "E593", {"start": v(17.46, 0.48) * mm, "end": v(17.68, 0.28) * mm});
            skLineSegment(sketch, "E594", {"start": v(17.68, 0.28) * mm, "end": v(17.9, 0.1) * mm});
            skLineSegment(sketch, "E595", {"start": v(17.9, 0.1) * mm, "end": v(18.13, -0.1) * mm});
            skLineSegment(sketch, "E596", {"start": v(18.13, -0.1) * mm, "end": v(18.38, -0.26) * mm});
            skLineSegment(sketch, "E597", {"start": v(18.38, -0.26) * mm, "end": v(18.63, -0.43) * mm});
            skLineSegment(sketch, "E598", {"start": v(18.63, -0.43) * mm, "end": v(18.9, -0.58) * mm});
            skLineSegment(sketch, "E599", {"start": v(18.9, -0.58) * mm, "end": v(19.16, -0.71) * mm});
            skLineSegment(sketch, "E600", {"start": v(19.16, -0.71) * mm, "end": v(19.2, -0.73) * mm});
            skLineSegment(sketch, "E601", {"start": v(19.2, -0.73) * mm, "end": v(19.22, -0.74) * mm});
            skLineSegment(sketch, "E602", {"start": v(19.22, -0.74) * mm, "end": v(19.26, -0.76) * mm});
            skLineSegment(sketch, "E603", {"start": v(19.26, -0.76) * mm, "end": v(19.29, -0.78) * mm});
            skLineSegment(sketch, "E604", {"start": v(19.29, -0.78) * mm, "end": v(19.32, -0.8) * mm});
            skLineSegment(sketch, "E605", {"start": v(19.32, -0.8) * mm, "end": v(19.35, -0.8) * mm});
            skLineSegment(sketch, "E606", {"start": v(19.35, -0.8) * mm, "end": v(19.38, -0.82) * mm});
            skLineSegment(sketch, "E607", {"start": v(19.38, -0.82) * mm, "end": v(19.4, -0.83) * mm});
            skLineSegment(sketch, "E608", {"start": v(19.4, -0.83) * mm, "end": v(18.89, -0.83) * mm});
            skLineSegment(sketch, "E609", {"start": v(18.89, -0.83) * mm, "end": v(18.37, -0.83) * mm});
            skLineSegment(sketch, "E610", {"start": v(18.37, -0.83) * mm, "end": v(17.85, -0.83) * mm});
            skLineSegment(sketch, "E611", {"start": v(17.85, -0.83) * mm, "end": v(17.33, -0.83) * mm});
            skLineSegment(sketch, "E612", {"start": v(17.33, -0.83) * mm, "end": v(16.82, -0.83) * mm});
            skLineSegment(sketch, "E613", {"start": v(16.82, -0.83) * mm, "end": v(16.3, -0.83) * mm});
            skLineSegment(sketch, "E614", {"start": v(16.3, -0.83) * mm, "end": v(15.78, -0.83) * mm});
            skLineSegment(sketch, "E615", {"start": v(15.78, -0.83) * mm, "end": v(15.26, -0.83) * mm});
            skLineSegment(sketch, "E616", {"start": v(15.26, -0.83) * mm, "end": v(15.26, -0.53) * mm});
            skLineSegment(sketch, "E617", {"start": v(15.26, -0.53) * mm, "end": v(15.26, -0.22) * mm});
            skLineSegment(sketch, "E618", {"start": v(15.26, -0.22) * mm, "end": v(15.26, 0.1) * mm});
            skLineSegment(sketch, "E619", {"start": v(15.26, 0.1) * mm, "end": v(15.26, 0.4) * mm});
            skLineSegment(sketch, "E620", {"start": v(15.26, 0.4) * mm, "end": v(15.26, 0.7) * mm});
            skLineSegment(sketch, "E621", {"start": v(15.26, 0.7) * mm, "end": v(15.26, 1.02) * mm});
            skLineSegment(sketch, "E622", {"start": v(15.26, 1.02) * mm, "end": v(15.26, 1.33) * mm});
            skLineSegment(sketch, "E623", {"start": v(15.26, 1.33) * mm, "end": v(15.26, 1.63) * mm});
            skLineSegment(sketch, "E624", {"start": v(15.26, 1.63) * mm, "end": v(14.55, 1.63) * mm});
            skLineSegment(sketch, "E625", {"start": v(14.55, 1.63) * mm, "end": v(13.84, 1.63) * mm});
            skLineSegment(sketch, "E626", {"start": v(13.84, 1.63) * mm, "end": v(13.12, 1.63) * mm});
            skLineSegment(sketch, "E627", {"start": v(13.12, 1.63) * mm, "end": v(12.41, 1.63) * mm});
            skLineSegment(sketch, "E628", {"start": v(12.41, 1.63) * mm, "end": v(11.7, 1.63) * mm});
            skLineSegment(sketch, "E629", {"start": v(11.7, 1.63) * mm, "end": v(10.99, 1.63) * mm});
            skLineSegment(sketch, "E630", {"start": v(10.99, 1.63) * mm, "end": v(10.27, 1.63) * mm});
            skLineSegment(sketch, "E631", {"start": v(10.27, 1.63) * mm, "end": v(9.56, 1.63) * mm});
            skLineSegment(sketch, "E632", {"start": v(9.56, 1.63) * mm, "end": v(10.27, 2.52) * mm});
            skLineSegment(sketch, "E633", {"start": v(10.27, 2.52) * mm, "end": v(10.97, 3.4) * mm});
            skLineSegment(sketch, "E634", {"start": v(10.97, 3.4) * mm, "end": v(11.67, 4.3) * mm});
            skLineSegment(sketch, "E635", {"start": v(11.67, 4.3) * mm, "end": v(12.38, 5.18) * mm});
            skLineSegment(sketch, "E636", {"start": v(12.38, 5.18) * mm, "end": v(13.08, 6.07) * mm});
            skLineSegment(sketch, "E637", {"start": v(13.08, 6.07) * mm, "end": v(13.78, 6.96) * mm});
            skLineSegment(sketch, "E638", {"start": v(13.78, 6.96) * mm, "end": v(14.49, 7.84) * mm});
            skLineSegment(sketch, "E639", {"start": v(14.49, 7.84) * mm, "end": v(15.19, 8.73) * mm});
            skLineSegment(sketch, "E640", {"start": v(15.19, 8.73) * mm, "end": v(15.19, 9.02) * mm});
            skLineSegment(sketch, "E641", {"start": v(15.19, 9.02) * mm, "end": v(15.19, 9.3) * mm});
            skLineSegment(sketch, "E642", {"start": v(15.19, 9.3) * mm, "end": v(15.19, 9.59) * mm});
            skLineSegment(sketch, "E643", {"start": v(15.19, 9.59) * mm, "end": v(15.19, 9.87) * mm});
            skLineSegment(sketch, "E644", {"start": v(15.19, 9.87) * mm, "end": v(15.19, 10.16) * mm});
            skLineSegment(sketch, "E645", {"start": v(15.19, 10.16) * mm, "end": v(15.19, 10.45) * mm});
            skLineSegment(sketch, "E646", {"start": v(15.19, 10.45) * mm, "end": v(15.19, 10.73) * mm});
            skLineSegment(sketch, "E647", {"start": v(15.19, 10.73) * mm, "end": v(15.19, 11.02) * mm});
            skLineSegment(sketch, "E648", {"start": v(15.19, 11.02) * mm, "end": v(14, 11.02) * mm});
            skLineSegment(sketch, "E649", {"start": v(14, 11.02) * mm, "end": v(12.83, 11.02) * mm});
            skLineSegment(sketch, "E650", {"start": v(12.83, 11.02) * mm, "end": v(11.64, 11.02) * mm});
            skLineSegment(sketch, "E651", {"start": v(11.64, 11.02) * mm, "end": v(10.46, 11.02) * mm});
            skLineSegment(sketch, "E652", {"start": v(10.46, 11.02) * mm, "end": v(9.28, 11.02) * mm});
            skLineSegment(sketch, "E653", {"start": v(9.28, 11.02) * mm, "end": v(8.1, 11.02) * mm});
            skLineSegment(sketch, "E654", {"start": v(8.1, 11.02) * mm, "end": v(6.92, 11.02) * mm});
            skLineSegment(sketch, "E655", {"start": v(6.92, 11.02) * mm, "end": v(5.73, 11.02) * mm});
            skLineSegment(sketch, "E656", {"start": v(5.73, 11.02) * mm, "end": v(5.73, 10.67) * mm});
            skLineSegment(sketch, "E657", {"start": v(5.73, 10.67) * mm, "end": v(5.73, 10.31) * mm});
            skLineSegment(sketch, "E658", {"start": v(5.73, 10.31) * mm, "end": v(5.73, 9.96) * mm});
            skLineSegment(sketch, "E659", {"start": v(5.73, 9.96) * mm, "end": v(5.73, 9.6) * mm});
            skLineSegment(sketch, "E660", {"start": v(5.73, 9.6) * mm, "end": v(5.73, 9.25) * mm});
            skLineSegment(sketch, "E661", {"start": v(5.73, 9.25) * mm, "end": v(5.73, 8.9) * mm});
            skLineSegment(sketch, "E662", {"start": v(5.73, 8.9) * mm, "end": v(5.73, 8.55) * mm});
            skLineSegment(sketch, "E663", {"start": v(5.73, 8.55) * mm, "end": v(5.73, 8.2) * mm});
            skLineSegment(sketch, "E664", {"start": v(5.73, 8.2) * mm, "end": v(6.45, 8.2) * mm});
            skLineSegment(sketch, "E665", {"start": v(6.45, 8.2) * mm, "end": v(7.16, 8.2) * mm});
            skLineSegment(sketch, "E666", {"start": v(7.16, 8.2) * mm, "end": v(7.87, 8.2) * mm});
            skLineSegment(sketch, "E667", {"start": v(7.87, 8.2) * mm, "end": v(8.58, 8.2) * mm});
            skLineSegment(sketch, "E668", {"start": v(8.58, 8.2) * mm, "end": v(9.3, 8.2) * mm});
            skLineSegment(sketch, "E669", {"start": v(9.3, 8.2) * mm, "end": v(10, 8.2) * mm});
            skLineSegment(sketch, "E670", {"start": v(10, 8.2) * mm, "end": v(10.72, 8.2) * mm});
            skLineSegment(sketch, "E671", {"start": v(10.72, 8.2) * mm, "end": v(11.43, 8.2) * mm});
            skLineSegment(sketch, "E672", {"start": v(11.43, 8.2) * mm, "end": v(10.7, 7.32) * mm});
            skLineSegment(sketch, "E673", {"start": v(10.7, 7.32) * mm, "end": v(9.95, 6.44) * mm});
            skLineSegment(sketch, "E674", {"start": v(9.95, 6.44) * mm, "end": v(9.2, 5.56) * mm});
            skLineSegment(sketch, "E675", {"start": v(9.2, 5.56) * mm, "end": v(8.46, 4.69) * mm});
            skLineSegment(sketch, "E676", {"start": v(8.46, 4.69) * mm, "end": v(7.72, 3.8) * mm});
            skLineSegment(sketch, "E677", {"start": v(7.72, 3.8) * mm, "end": v(6.97, 2.93) * mm});
            skLineSegment(sketch, "E678", {"start": v(6.97, 2.93) * mm, "end": v(6.23, 2.05) * mm});
            skLineSegment(sketch, "E679", {"start": v(6.23, 2.05) * mm, "end": v(5.49, 1.17) * mm});
            skLineSegment(sketch, "E680", {"start": v(5.49, 1.17) * mm, "end": v(5.49, 0.92) * mm});
            skLineSegment(sketch, "E681", {"start": v(5.49, 0.92) * mm, "end": v(5.49, 0.67) * mm});
            skLineSegment(sketch, "E682", {"start": v(5.49, 0.67) * mm, "end": v(5.49, 0.42) * mm});
            skLineSegment(sketch, "E683", {"start": v(5.49, 0.42) * mm, "end": v(5.49, 0.17) * mm});
            skLineSegment(sketch, "E684", {"start": v(5.49, 0.17) * mm, "end": v(5.49, -0.08) * mm});
            skLineSegment(sketch, "E685", {"start": v(5.49, -0.08) * mm, "end": v(5.49, -0.33) * mm});
            skLineSegment(sketch, "E686", {"start": v(5.49, -0.33) * mm, "end": v(5.49, -0.58) * mm});
            skLineSegment(sketch, "E687", {"start": v(5.49, -0.58) * mm, "end": v(5.49, -0.83) * mm});
            skLineSegment(sketch, "E688", {"start": v(5.49, -0.83) * mm, "end": v(4.63, -0.83) * mm});
            skLineSegment(sketch, "E689", {"start": v(4.63, -0.83) * mm, "end": v(3.77, -0.83) * mm});
            skLineSegment(sketch, "E690", {"start": v(3.77, -0.83) * mm, "end": v(2.9, -0.83) * mm});
            skLineSegment(sketch, "E691", {"start": v(2.9, -0.83) * mm, "end": v(2.05, -0.83) * mm});
            skLineSegment(sketch, "E692", {"start": v(2.05, -0.83) * mm, "end": v(1.19, -0.83) * mm});
            skLineSegment(sketch, "E693", {"start": v(1.19, -0.83) * mm, "end": v(0.33, -0.83) * mm});
            skLineSegment(sketch, "E694", {"start": v(0.33, -0.83) * mm, "end": v(-0.53, -0.83) * mm});
            skLineSegment(sketch, "E695", {"start": v(-0.53, -0.83) * mm, "end": v(-1.4, -0.83) * mm});
            skLineSegment(sketch, "E696", {"start": v(-1.4, -0.83) * mm, "end": v(-1.4, -0.4) * mm});
            skLineSegment(sketch, "E697", {"start": v(-1.4, -0.4) * mm, "end": v(-1.4, 0.04) * mm});
            skLineSegment(sketch, "E698", {"start": v(-1.4, 0.04) * mm, "end": v(-1.4, 0.47) * mm});
            skLineSegment(sketch, "E699", {"start": v(-1.4, 0.47) * mm, "end": v(-1.4, 0.91) * mm});
            skLineSegment(sketch, "E700", {"start": v(-1.4, 0.91) * mm, "end": v(-1.4, 1.35) * mm});
            skLineSegment(sketch, "E701", {"start": v(-1.4, 1.35) * mm, "end": v(-1.4, 1.78) * mm});
            skLineSegment(sketch, "E702", {"start": v(-1.4, 1.78) * mm, "end": v(-1.4, 2.22) * mm});
            skLineSegment(sketch, "E703", {"start": v(-1.4, 2.22) * mm, "end": v(-1.4, 2.66) * mm});
            skLineSegment(sketch, "E704", {"start": v(-1.4, 2.66) * mm, "end": v(-1.12, 2.66) * mm});
            skLineSegment(sketch, "E705", {"start": v(-1.12, 2.66) * mm, "end": v(-0.85, 2.66) * mm});
            skLineSegment(sketch, "E706", {"start": v(-0.85, 2.66) * mm, "end": v(-0.57, 2.66) * mm});
            skLineSegment(sketch, "E707", {"start": v(-0.57, 2.66) * mm, "end": v(-0.3, 2.66) * mm});
            skLineSegment(sketch, "E708", {"start": v(-0.3, 2.66) * mm, "end": v(-0.03, 2.66) * mm});
            skLineSegment(sketch, "E709", {"start": v(-0.03, 2.66) * mm, "end": v(0.24, 2.66) * mm});
            skLineSegment(sketch, "E710", {"start": v(0.24, 2.66) * mm, "end": v(0.51, 2.66) * mm});
            skLineSegment(sketch, "E711", {"start": v(0.51, 2.66) * mm, "end": v(0.79, 2.66) * mm});
            skLineSegment(sketch, "E712", {"start": v(0.79, 2.66) * mm, "end": v(1, 2.66) * mm});
            skLineSegment(sketch, "E713", {"start": v(1, 2.66) * mm, "end": v(1.22, 2.68) * mm});
            skLineSegment(sketch, "E714", {"start": v(1.22, 2.68) * mm, "end": v(1.43, 2.7) * mm});
            skLineSegment(sketch, "E715", {"start": v(1.43, 2.7) * mm, "end": v(1.64, 2.75) * mm});
            skLineSegment(sketch, "E716", {"start": v(1.64, 2.75) * mm, "end": v(1.84, 2.8) * mm});
            skLineSegment(sketch, "E717", {"start": v(1.84, 2.8) * mm, "end": v(2.04, 2.86) * mm});
            skLineSegment(sketch, "E718", {"start": v(2.04, 2.86) * mm, "end": v(2.23, 2.93) * mm});
            skLineSegment(sketch, "E719", {"start": v(2.23, 2.93) * mm, "end": v(2.41, 3.01) * mm});
            skLineSegment(sketch, "E720", {"start": v(2.41, 3.01) * mm, "end": v(2.6, 3.1) * mm});
            skLineSegment(sketch, "E721", {"start": v(2.6, 3.1) * mm, "end": v(2.77, 3.2) * mm});
            skLineSegment(sketch, "E722", {"start": v(2.77, 3.2) * mm, "end": v(2.93, 3.3) * mm});
            skLineSegment(sketch, "E723", {"start": v(2.93, 3.3) * mm, "end": v(3.1, 3.42) * mm});
            skLineSegment(sketch, "E724", {"start": v(3.1, 3.42) * mm, "end": v(3.25, 3.55) * mm});
            skLineSegment(sketch, "E725", {"start": v(3.25, 3.55) * mm, "end": v(3.4, 3.68) * mm});
            skLineSegment(sketch, "E726", {"start": v(3.4, 3.68) * mm, "end": v(3.53, 3.81) * mm});
            skLineSegment(sketch, "E727", {"start": v(3.53, 3.81) * mm, "end": v(3.67, 3.96) * mm});
            skLineSegment(sketch, "E728", {"start": v(3.67, 3.96) * mm, "end": v(3.79, 4.1) * mm});
            skLineSegment(sketch, "E729", {"start": v(3.79, 4.1) * mm, "end": v(3.9, 4.26) * mm});
            skLineSegment(sketch, "E730", {"start": v(3.9, 4.26) * mm, "end": v(4.02, 4.42) * mm});
            skLineSegment(sketch, "E731", {"start": v(4.02, 4.42) * mm, "end": v(4.12, 4.59) * mm});
            skLineSegment(sketch, "E732", {"start": v(4.12, 4.59) * mm, "end": v(4.22, 4.76) * mm});
            skLineSegment(sketch, "E733", {"start": v(4.22, 4.76) * mm, "end": v(4.3, 4.93) * mm});
            skLineSegment(sketch, "E734", {"start": v(4.3, 4.93) * mm, "end": v(4.39, 5.11) * mm});
            skLineSegment(sketch, "E735", {"start": v(4.39, 5.11) * mm, "end": v(4.46, 5.3) * mm});
            skLineSegment(sketch, "E736", {"start": v(4.46, 5.3) * mm, "end": v(4.53, 5.48) * mm});
            skLineSegment(sketch, "E737", {"start": v(4.53, 5.48) * mm, "end": v(4.59, 5.67) * mm});
            skLineSegment(sketch, "E738", {"start": v(4.59, 5.67) * mm, "end": v(4.64, 5.86) * mm});
            skLineSegment(sketch, "E739", {"start": v(4.64, 5.86) * mm, "end": v(4.68, 6.06) * mm});
            skLineSegment(sketch, "E740", {"start": v(4.68, 6.06) * mm, "end": v(4.7, 6.26) * mm});
            skLineSegment(sketch, "E741", {"start": v(4.7, 6.26) * mm, "end": v(4.73, 6.46) * mm});
            skLineSegment(sketch, "E742", {"start": v(4.73, 6.46) * mm, "end": v(4.75, 6.66) * mm});
            skLineSegment(sketch, "E743", {"start": v(4.75, 6.66) * mm, "end": v(4.75, 6.86) * mm});
            skLineSegment(sketch, "E744", {"start": v(4.75, 6.86) * mm, "end": v(4.75, 7.05) * mm});
            skLineSegment(sketch, "E745", {"start": v(4.75, 7.05) * mm, "end": v(4.73, 7.24) * mm});
            skLineSegment(sketch, "E746", {"start": v(4.73, 7.24) * mm, "end": v(4.7, 7.43) * mm});
            skLineSegment(sketch, "E747", {"start": v(4.7, 7.43) * mm, "end": v(4.67, 7.62) * mm});
            skLineSegment(sketch, "E748", {"start": v(4.67, 7.62) * mm, "end": v(4.63, 7.81) * mm});
            skLineSegment(sketch, "E749", {"start": v(4.63, 7.81) * mm, "end": v(4.58, 8) * mm});
            skLineSegment(sketch, "E750", {"start": v(4.58, 8) * mm, "end": v(4.52, 8.19) * mm});
            skLineSegment(sketch, "E751", {"start": v(4.52, 8.19) * mm, "end": v(4.44, 8.38) * mm});
            skLineSegment(sketch, "E752", {"start": v(4.44, 8.38) * mm, "end": v(4.37, 8.56) * mm});
            skLineSegment(sketch, "E753", {"start": v(4.37, 8.56) * mm, "end": v(4.28, 8.74) * mm});
            skLineSegment(sketch, "E754", {"start": v(4.28, 8.74) * mm, "end": v(4.19, 8.91) * mm});
            skLineSegment(sketch, "E755", {"start": v(4.19, 8.91) * mm, "end": v(4.09, 9.08) * mm});
            skLineSegment(sketch, "E756", {"start": v(4.09, 9.08) * mm, "end": v(3.98, 9.25) * mm});
            skLineSegment(sketch, "E757", {"start": v(3.98, 9.25) * mm, "end": v(3.86, 9.4) * mm});
            skLineSegment(sketch, "E758", {"start": v(3.86, 9.4) * mm, "end": v(3.74, 9.56) * mm});
            skLineSegment(sketch, "E759", {"start": v(3.74, 9.56) * mm, "end": v(3.61, 9.71) * mm});
            skLineSegment(sketch, "E760", {"start": v(3.61, 9.71) * mm, "end": v(3.48, 9.85) * mm});
            skLineSegment(sketch, "E761", {"start": v(3.48, 9.85) * mm, "end": v(3.33, 10) * mm});
            skLineSegment(sketch, "E762", {"start": v(3.33, 10) * mm, "end": v(3.18, 10.12) * mm});
            skLineSegment(sketch, "E763", {"start": v(3.18, 10.12) * mm, "end": v(3.03, 10.24) * mm});
            skLineSegment(sketch, "E764", {"start": v(3.03, 10.24) * mm, "end": v(2.87, 10.36) * mm});
            skLineSegment(sketch, "E765", {"start": v(2.87, 10.36) * mm, "end": v(2.7, 10.46) * mm});
            skLineSegment(sketch, "E766", {"start": v(2.7, 10.46) * mm, "end": v(2.52, 10.57) * mm});
            skLineSegment(sketch, "E767", {"start": v(2.52, 10.57) * mm, "end": v(2.34, 10.66) * mm});
            skLineSegment(sketch, "E768", {"start": v(2.34, 10.66) * mm, "end": v(2.15, 10.74) * mm});
            skLineSegment(sketch, "E769", {"start": v(2.15, 10.74) * mm, "end": v(1.96, 10.82) * mm});
            skLineSegment(sketch, "E770", {"start": v(1.96, 10.82) * mm, "end": v(1.76, 10.88) * mm});
            skLineSegment(sketch, "E771", {"start": v(1.76, 10.88) * mm, "end": v(1.56, 10.93) * mm});
            skLineSegment(sketch, "E772", {"start": v(1.56, 10.93) * mm, "end": v(1.35, 10.97) * mm});
            skLineSegment(sketch, "E773", {"start": v(1.35, 10.97) * mm, "end": v(1.14, 11) * mm});
            skLineSegment(sketch, "E774", {"start": v(1.14, 11) * mm, "end": v(0.92, 11.01) * mm});
            skLineSegment(sketch, "E775", {"start": v(0.92, 11.01) * mm, "end": v(0.7, 11.02) * mm});
            skLineSegment(sketch, "E776", {"start": v(0.7, 11.02) * mm, "end": v(0.05, 11.02) * mm});
            skLineSegment(sketch, "E777", {"start": v(0.05, 11.02) * mm, "end": v(-0.6, 11.02) * mm});
            skLineSegment(sketch, "E778", {"start": v(-0.6, 11.02) * mm, "end": v(-1.25, 11.02) * mm});
            skLineSegment(sketch, "E779", {"start": v(-1.25, 11.02) * mm, "end": v(-1.9, 11.02) * mm});
            skLineSegment(sketch, "E780", {"start": v(-1.9, 11.02) * mm, "end": v(-2.55, 11.02) * mm});
            skLineSegment(sketch, "E781", {"start": v(-2.55, 11.02) * mm, "end": v(-3.2, 11.02) * mm});
            skLineSegment(sketch, "E782", {"start": v(-3.2, 11.02) * mm, "end": v(-3.85, 11.02) * mm});
            skLineSegment(sketch, "E783", {"start": v(-3.85, 11.02) * mm, "end": v(-4.5, 11.02) * mm});
            skLineSegment(sketch, "E784", {"start": v(-4.5, 11.02) * mm, "end": v(-4.5, 9.54) * mm});
            skLineSegment(sketch, "E785", {"start": v(-4.5, 9.54) * mm, "end": v(-4.5, 8.06) * mm});
            skLineSegment(sketch, "E786", {"start": v(-4.5, 8.06) * mm, "end": v(-4.5, 6.57) * mm});
            skLineSegment(sketch, "E787", {"start": v(-4.5, 6.57) * mm, "end": v(-4.5, 5.1) * mm});
            skLineSegment(sketch, "E788", {"start": v(-4.5, 5.1) * mm, "end": v(-4.5, 3.61) * mm});
            skLineSegment(sketch, "E789", {"start": v(-4.5, 3.61) * mm, "end": v(-4.5, 2.13) * mm});
            skLineSegment(sketch, "E790", {"start": v(-4.5, 2.13) * mm, "end": v(-4.5, 0.65) * mm});
            skLineSegment(sketch, "E791", {"start": v(-4.5, 0.65) * mm, "end": v(-4.5, -0.83) * mm});
            skLineSegment(sketch, "E792", {"start": v(-4.5, -0.83) * mm, "end": v(-5.08, -0.83) * mm});
            skLineSegment(sketch, "E793", {"start": v(-5.08, -0.83) * mm, "end": v(-5.67, -0.83) * mm});
            skLineSegment(sketch, "E794", {"start": v(-5.67, -0.83) * mm, "end": v(-6.26, -0.83) * mm});
            skLineSegment(sketch, "E795", {"start": v(-6.26, -0.83) * mm, "end": v(-6.85, -0.83) * mm});
            skLineSegment(sketch, "E796", {"start": v(-6.85, -0.83) * mm, "end": v(-7.44, -0.83) * mm});
            skLineSegment(sketch, "E797", {"start": v(-7.44, -0.83) * mm, "end": v(-8.02, -0.83) * mm});
            skLineSegment(sketch, "E798", {"start": v(-8.02, -0.83) * mm, "end": v(-8.61, -0.83) * mm});
            skLineSegment(sketch, "E799", {"start": v(-8.61, -0.83) * mm, "end": v(-9.2, -0.83) * mm});
            skLineSegment(sketch, "E800", {"start": v(-9.2, -0.83) * mm, "end": v(-9.17, -0.82) * mm});
            skLineSegment(sketch, "E801", {"start": v(-9.17, -0.82) * mm, "end": v(-9.15, -0.8) * mm});
            skLineSegment(sketch, "E802", {"start": v(-9.15, -0.8) * mm, "end": v(-9.12, -0.8) * mm});
            skLineSegment(sketch, "E803", {"start": v(-9.12, -0.8) * mm, "end": v(-9.1, -0.78) * mm});
            skLineSegment(sketch, "E804", {"start": v(-9.1, -0.78) * mm, "end": v(-9.07, -0.77) * mm});
            skLineSegment(sketch, "E805", {"start": v(-9.07, -0.77) * mm, "end": v(-9.04, -0.76) * mm});
            skLineSegment(sketch, "E806", {"start": v(-9.04, -0.76) * mm, "end": v(-9.02, -0.74) * mm});
            skLineSegment(sketch, "E807", {"start": v(-9.02, -0.74) * mm, "end": v(-9, -0.73) * mm});
            skLineSegment(sketch, "E808", {"start": v(-9, -0.73) * mm, "end": v(-8.72, -0.6) * mm});
            skLineSegment(sketch, "E809", {"start": v(-8.72, -0.6) * mm, "end": v(-8.46, -0.45) * mm});
            skLineSegment(sketch, "E810", {"start": v(-8.46, -0.45) * mm, "end": v(-8.2, -0.3) * mm});
            skLineSegment(sketch, "E811", {"start": v(-8.2, -0.3) * mm, "end": v(-7.96, -0.13) * mm});
            skLineSegment(sketch, "E812", {"start": v(-7.96, -0.13) * mm, "end": v(-7.72, 0.05) * mm});
            skLineSegment(sketch, "E813", {"start": v(-7.72, 0.05) * mm, "end": v(-7.5, 0.23) * mm});
            skLineSegment(sketch, "E814", {"start": v(-7.5, 0.23) * mm, "end": v(-7.28, 0.43) * mm});
            skLineSegment(sketch, "E815", {"start": v(-7.28, 0.43) * mm, "end": v(-7.07, 0.64) * mm});
            skLineSegment(sketch, "E816", {"start": v(-7.07, 0.64) * mm, "end": v(-6.88, 0.85) * mm});
            skLineSegment(sketch, "E817", {"start": v(-6.88, 0.85) * mm, "end": v(-6.7, 1.08) * mm});
            skLineSegment(sketch, "E818", {"start": v(-6.7, 1.08) * mm, "end": v(-6.52, 1.31) * mm});
            skLineSegment(sketch, "E819", {"start": v(-6.52, 1.31) * mm, "end": v(-6.36, 1.55) * mm});
            skLineSegment(sketch, "E820", {"start": v(-6.36, 1.55) * mm, "end": v(-6.2, 1.8) * mm});
            skLineSegment(sketch, "E821", {"start": v(-6.2, 1.8) * mm, "end": v(-6.06, 2.06) * mm});
            skLineSegment(sketch, "E822", {"start": v(-6.06, 2.06) * mm, "end": v(-5.93, 2.33) * mm});
            skLineSegment(sketch, "E823", {"start": v(-5.93, 2.33) * mm, "end": v(-5.81, 2.6) * mm});
            skLineSegment(sketch, "E824", {"start": v(-5.81, 2.6) * mm, "end": v(-5.7, 2.88) * mm});
            skLineSegment(sketch, "E825", {"start": v(-5.7, 2.88) * mm, "end": v(-5.62, 3.16) * mm});
            skLineSegment(sketch, "E826", {"start": v(-5.62, 3.16) * mm, "end": v(-5.54, 3.45) * mm});
            skLineSegment(sketch, "E827", {"start": v(-5.54, 3.45) * mm, "end": v(-5.47, 3.74) * mm});
            skLineSegment(sketch, "E828", {"start": v(-5.47, 3.74) * mm, "end": v(-5.42, 4.03) * mm});
            skLineSegment(sketch, "E829", {"start": v(-5.42, 4.03) * mm, "end": v(-5.39, 4.32) * mm});
            skLineSegment(sketch, "E830", {"start": v(-5.39, 4.32) * mm, "end": v(-5.37, 4.62) * mm});
            skLineSegment(sketch, "E831", {"start": v(-5.37, 4.62) * mm, "end": v(-5.36, 4.92) * mm});
            skLineSegment(sketch, "E832", {"start": v(-5.36, 4.92) * mm, "end": v(-5.37, 5.2) * mm});
            skLineSegment(sketch, "E833", {"start": v(-5.37, 5.2) * mm, "end": v(-5.39, 5.49) * mm});
            skLineSegment(sketch, "E834", {"start": v(-5.39, 5.49) * mm, "end": v(-5.42, 5.77) * mm});
            skLineSegment(sketch, "E835", {"start": v(-5.42, 5.77) * mm, "end": v(-5.47, 6.05) * mm});
            skLineSegment(sketch, "E836", {"start": v(-5.47, 6.05) * mm, "end": v(-5.53, 6.34) * mm});
            skLineSegment(sketch, "E837", {"start": v(-5.53, 6.34) * mm, "end": v(-5.6, 6.62) * mm});
            skLineSegment(sketch, "E838", {"start": v(-5.6, 6.62) * mm, "end": v(-5.69, 6.9) * mm});
            skLineSegment(sketch, "E839", {"start": v(-5.69, 6.9) * mm, "end": v(-5.79, 7.18) * mm});
            skLineSegment(sketch, "E840", {"start": v(-5.79, 7.18) * mm, "end": v(-5.9, 7.45) * mm});
            skLineSegment(sketch, "E841", {"start": v(-5.9, 7.45) * mm, "end": v(-6.02, 7.72) * mm});
            skLineSegment(sketch, "E842", {"start": v(-6.02, 7.72) * mm, "end": v(-6.16, 7.98) * mm});
            skLineSegment(sketch, "E843", {"start": v(-6.16, 7.98) * mm, "end": v(-6.3, 8.23) * mm});
            skLineSegment(sketch, "E844", {"start": v(-6.3, 8.23) * mm, "end": v(-6.46, 8.47) * mm});
            skLineSegment(sketch, "E845", {"start": v(-6.46, 8.47) * mm, "end": v(-6.63, 8.71) * mm});
            skLineSegment(sketch, "E846", {"start": v(-6.63, 8.71) * mm, "end": v(-6.81, 8.94) * mm});
            skLineSegment(sketch, "E847", {"start": v(-6.81, 8.94) * mm, "end": v(-7, 9.16) * mm});
            skLineSegment(sketch, "E848", {"start": v(-7, 9.16) * mm, "end": v(-7.2, 9.38) * mm});
            skLineSegment(sketch, "E849", {"start": v(-7.2, 9.38) * mm, "end": v(-7.42, 9.58) * mm});
            skLineSegment(sketch, "E850", {"start": v(-7.42, 9.58) * mm, "end": v(-7.64, 9.77) * mm});
            skLineSegment(sketch, "E851", {"start": v(-7.64, 9.77) * mm, "end": v(-7.87, 9.95) * mm});
            skLineSegment(sketch, "E852", {"start": v(-7.87, 9.95) * mm, "end": v(-8.12, 10.12) * mm});
            skLineSegment(sketch, "E853", {"start": v(-8.12, 10.12) * mm, "end": v(-8.37, 10.28) * mm});
            skLineSegment(sketch, "E854", {"start": v(-8.37, 10.28) * mm, "end": v(-8.63, 10.43) * mm});
            skLineSegment(sketch, "E855", {"start": v(-8.63, 10.43) * mm, "end": v(-8.9, 10.57) * mm});
            skLineSegment(sketch, "E856", {"start": v(-8.9, 10.57) * mm, "end": v(-9.19, 10.7) * mm});
            skLineSegment(sketch, "E857", {"start": v(-9.19, 10.7) * mm, "end": v(-9.48, 10.8) * mm});
            skLineSegment(sketch, "E858", {"start": v(-9.48, 10.8) * mm, "end": v(-9.78, 10.9) * mm});
            skLineSegment(sketch, "E859", {"start": v(-9.78, 10.9) * mm, "end": v(-10.08, 10.97) * mm});
            skLineSegment(sketch, "E860", {"start": v(-10.08, 10.97) * mm, "end": v(-10.4, 11.03) * mm});
            skLineSegment(sketch, "E861", {"start": v(-10.4, 11.03) * mm, "end": v(-10.72, 11.07) * mm});
            skLineSegment(sketch, "E862", {"start": v(-10.72, 11.07) * mm, "end": v(-11.05, 11.1) * mm});
            skLineSegment(sketch, "E863", {"start": v(-11.05, 11.1) * mm, "end": v(-11.38, 11.1) * mm});
            skLineSegment(sketch, "E864", {"start": v(-11.38, 11.1) * mm, "end": v(-11.7, 11.1) * mm});
            skLineSegment(sketch, "E865", {"start": v(-11.7, 11.1) * mm, "end": v(-12.03, 11.07) * mm});
            skLineSegment(sketch, "E866", {"start": v(-12.03, 11.07) * mm, "end": v(-12.34, 11.03) * mm});
            skLineSegment(sketch, "E867", {"start": v(-12.34, 11.03) * mm, "end": v(-12.65, 10.98) * mm});
            skLineSegment(sketch, "E868", {"start": v(-12.65, 10.98) * mm, "end": v(-12.95, 10.9) * mm});
            skLineSegment(sketch, "E869", {"start": v(-12.95, 10.9) * mm, "end": v(-13.25, 10.82) * mm});
            skLineSegment(sketch, "E870", {"start": v(-13.25, 10.82) * mm, "end": v(-13.54, 10.71) * mm});
            skLineSegment(sketch, "E871", {"start": v(-13.54, 10.71) * mm, "end": v(-13.82, 10.6) * mm});
            skLineSegment(sketch, "E872", {"start": v(-13.82, 10.6) * mm, "end": v(-14.09, 10.46) * mm});
            skLineSegment(sketch, "E873", {"start": v(-14.09, 10.46) * mm, "end": v(-14.35, 10.32) * mm});
            skLineSegment(sketch, "E874", {"start": v(-14.35, 10.32) * mm, "end": v(-14.6, 10.17) * mm});
            skLineSegment(sketch, "E875", {"start": v(-14.6, 10.17) * mm, "end": v(-14.85, 10) * mm});
            skLineSegment(sketch, "E876", {"start": v(-14.85, 10) * mm, "end": v(-15.1, 9.83) * mm});
            skLineSegment(sketch, "E877", {"start": v(-15.1, 9.83) * mm, "end": v(-15.32, 9.64) * mm});
            skLineSegment(sketch, "E878", {"start": v(-15.32, 9.64) * mm, "end": v(-15.54, 9.45) * mm});
            skLineSegment(sketch, "E879", {"start": v(-15.54, 9.45) * mm, "end": v(-15.74, 9.24) * mm});
            skLineSegment(sketch, "E880", {"start": v(-15.74, 9.24) * mm, "end": v(-15.94, 9.03) * mm});
            skLineSegment(sketch, "E881", {"start": v(-15.94, 9.03) * mm, "end": v(-16.13, 8.8) * mm});
            skLineSegment(sketch, "E882", {"start": v(-16.13, 8.8) * mm, "end": v(-16.3, 8.57) * mm});
            skLineSegment(sketch, "E883", {"start": v(-16.3, 8.57) * mm, "end": v(-16.47, 8.33) * mm});
            skLineSegment(sketch, "E884", {"start": v(-16.47, 8.33) * mm, "end": v(-16.62, 8.08) * mm});
            skLineSegment(sketch, "E885", {"start": v(-16.62, 8.08) * mm, "end": v(-16.76, 7.82) * mm});
            skLineSegment(sketch, "E886", {"start": v(-16.76, 7.82) * mm, "end": v(-16.9, 7.55) * mm});
            skLineSegment(sketch, "E887", {"start": v(-16.9, 7.55) * mm, "end": v(-17.01, 7.28) * mm});
            skLineSegment(sketch, "E888", {"start": v(-17.01, 7.28) * mm, "end": v(-17.12, 7) * mm});
            skLineSegment(sketch, "E889", {"start": v(-17.12, 7) * mm, "end": v(-17.2, 6.72) * mm});
            skLineSegment(sketch, "E890", {"start": v(-17.2, 6.72) * mm, "end": v(-17.29, 6.43) * mm});
            skLineSegment(sketch, "E891", {"start": v(-17.29, 6.43) * mm, "end": v(-17.35, 6.15) * mm});
            skLineSegment(sketch, "E892", {"start": v(-17.35, 6.15) * mm, "end": v(-17.4, 5.85) * mm});
            skLineSegment(sketch, "E893", {"start": v(-17.4, 5.85) * mm, "end": v(-17.44, 5.56) * mm});
            skLineSegment(sketch, "E894", {"start": v(-17.44, 5.56) * mm, "end": v(-17.46, 5.26) * mm});
            skLineSegment(sketch, "E895", {"start": v(-17.46, 5.26) * mm, "end": v(-17.47, 4.97) * mm});
            skLineSegment(sketch, "E896", {"start": v(-17.47, 4.97) * mm, "end": v(-17.46, 4.67) * mm});
            skLineSegment(sketch, "E897", {"start": v(-17.46, 4.67) * mm, "end": v(-17.44, 4.38) * mm});
            skLineSegment(sketch, "E898", {"start": v(-17.44, 4.38) * mm, "end": v(-17.4, 4.1) * mm});
            skLineSegment(sketch, "E899", {"start": v(-17.4, 4.1) * mm, "end": v(-17.36, 3.8) * mm});
            skLineSegment(sketch, "E900", {"start": v(-17.36, 3.8) * mm, "end": v(-17.3, 3.52) * mm});
            skLineSegment(sketch, "E901", {"start": v(-17.3, 3.52) * mm, "end": v(-17.22, 3.23) * mm});
            skLineSegment(sketch, "E902", {"start": v(-17.22, 3.23) * mm, "end": v(-17.13, 2.95) * mm});
            skLineSegment(sketch, "E903", {"start": v(-17.13, 2.95) * mm, "end": v(-17.03, 2.67) * mm});
            skLineSegment(sketch, "E904", {"start": v(-17.03, 2.67) * mm, "end": v(-16.91, 2.4) * mm});
            skLineSegment(sketch, "E905", {"start": v(-16.91, 2.4) * mm, "end": v(-16.79, 2.13) * mm});
            skLineSegment(sketch, "E906", {"start": v(-16.79, 2.13) * mm, "end": v(-16.65, 1.87) * mm});
            skLineSegment(sketch, "E907", {"start": v(-16.65, 1.87) * mm, "end": v(-16.5, 1.62) * mm});
            skLineSegment(sketch, "E908", {"start": v(-16.5, 1.62) * mm, "end": v(-16.35, 1.38) * mm});
            skLineSegment(sketch, "E909", {"start": v(-16.35, 1.38) * mm, "end": v(-16.18, 1.14) * mm});
            skLineSegment(sketch, "E910", {"start": v(-16.18, 1.14) * mm, "end": v(-16, 0.92) * mm});
            skLineSegment(sketch, "E911", {"start": v(-16, 0.92) * mm, "end": v(-15.8, 0.7) * mm});
            skLineSegment(sketch, "E912", {"start": v(-15.8, 0.7) * mm, "end": v(-15.6, 0.48) * mm});
            skLineSegment(sketch, "E913", {"start": v(-15.6, 0.48) * mm, "end": v(-15.4, 0.28) * mm});
            skLineSegment(sketch, "E914", {"start": v(-15.4, 0.28) * mm, "end": v(-15.17, 0.1) * mm});
            skLineSegment(sketch, "E915", {"start": v(-15.17, 0.1) * mm, "end": v(-14.93, -0.1) * mm});
            skLineSegment(sketch, "E916", {"start": v(-14.93, -0.1) * mm, "end": v(-14.7, -0.26) * mm});
            skLineSegment(sketch, "E917", {"start": v(-14.7, -0.26) * mm, "end": v(-14.44, -0.43) * mm});
            skLineSegment(sketch, "E918", {"start": v(-14.44, -0.43) * mm, "end": v(-14.18, -0.58) * mm});
            skLineSegment(sketch, "E919", {"start": v(-14.18, -0.58) * mm, "end": v(-13.9, -0.71) * mm});
            skLineSegment(sketch, "E920", {"start": v(-13.9, -0.71) * mm, "end": v(-13.87, -0.73) * mm});
            skLineSegment(sketch, "E921", {"start": v(-13.87, -0.73) * mm, "end": v(-13.84, -0.74) * mm});
            skLineSegment(sketch, "E922", {"start": v(-13.84, -0.74) * mm, "end": v(-13.81, -0.76) * mm});
            skLineSegment(sketch, "E923", {"start": v(-13.81, -0.76) * mm, "end": v(-13.78, -0.78) * mm});
            skLineSegment(sketch, "E924", {"start": v(-13.78, -0.78) * mm, "end": v(-13.75, -0.8) * mm});
            skLineSegment(sketch, "E925", {"start": v(-13.75, -0.8) * mm, "end": v(-13.72, -0.8) * mm});
            skLineSegment(sketch, "E926", {"start": v(-13.72, -0.8) * mm, "end": v(-13.7, -0.82) * mm});
            skLineSegment(sketch, "E927", {"start": v(-13.7, -0.82) * mm, "end": v(-13.66, -0.83) * mm});
            skLineSegment(sketch, "E928", {"start": v(-13.66, -0.83) * mm, "end": v(-14.24, -0.83) * mm});
            skLineSegment(sketch, "E929", {"start": v(-14.24, -0.83) * mm, "end": v(-14.83, -0.83) * mm});
            skLineSegment(sketch, "E930", {"start": v(-14.83, -0.83) * mm, "end": v(-15.4, -0.83) * mm});
            skLineSegment(sketch, "E931", {"start": v(-15.4, -0.83) * mm, "end": v(-16, -0.83) * mm});
            skLineSegment(sketch, "E932", {"start": v(-16, -0.83) * mm, "end": v(-16.58, -0.83) * mm});
            skLineSegment(sketch, "E933", {"start": v(-16.58, -0.83) * mm, "end": v(-17.16, -0.83) * mm});
            skLineSegment(sketch, "E934", {"start": v(-17.16, -0.83) * mm, "end": v(-17.74, -0.83) * mm});
            skLineSegment(sketch, "E935", {"start": v(-17.74, -0.83) * mm, "end": v(-18.33, -0.83) * mm});
            skLineSegment(sketch, "E936", {"start": v(-18.33, -0.83) * mm, "end": v(-18.33, 0.65) * mm});
            skLineSegment(sketch, "E937", {"start": v(-18.33, 0.65) * mm, "end": v(-18.33, 2.13) * mm});
            skLineSegment(sketch, "E938", {"start": v(-18.33, 2.13) * mm, "end": v(-18.33, 3.61) * mm});
            skLineSegment(sketch, "E939", {"start": v(-18.33, 3.61) * mm, "end": v(-18.33, 5.1) * mm});
            skLineSegment(sketch, "E940", {"start": v(-18.33, 5.1) * mm, "end": v(-18.33, 6.57) * mm});
            skLineSegment(sketch, "E941", {"start": v(-18.33, 6.57) * mm, "end": v(-18.33, 8.06) * mm});
            skLineSegment(sketch, "E942", {"start": v(-18.33, 8.06) * mm, "end": v(-18.33, 9.54) * mm});
            skLineSegment(sketch, "E943", {"start": v(-18.33, 9.54) * mm, "end": v(-18.33, 11.02) * mm});
            skLineSegment(sketch, "E944", {"start": v(-18.33, 11.02) * mm, "end": v(-18.7, 11.02) * mm});
            skLineSegment(sketch, "E945", {"start": v(-18.7, 11.02) * mm, "end": v(-19.1, 11.02) * mm});
            skLineSegment(sketch, "E946", {"start": v(-19.1, 11.02) * mm, "end": v(-19.48, 11.02) * mm});
            skLineSegment(sketch, "E947", {"start": v(-19.48, 11.02) * mm, "end": v(-19.86, 11.02) * mm});
            skLineSegment(sketch, "E948", {"start": v(-19.86, 11.02) * mm, "end": v(-20.24, 11.02) * mm});
            skLineSegment(sketch, "E949", {"start": v(-20.24, 11.02) * mm, "end": v(-20.63, 11.02) * mm});
            skLineSegment(sketch, "E950", {"start": v(-20.63, 11.02) * mm, "end": v(-21.01, 11.02) * mm});
            skLineSegment(sketch, "E951", {"start": v(-21.01, 11.02) * mm, "end": v(-21.4, 11.02) * mm});
            skLineSegment(sketch, "E952", {"start": v(-21.4, 11.02) * mm, "end": v(-21.4, 10.45) * mm});
            skLineSegment(sketch, "E953", {"start": v(-21.4, 10.45) * mm, "end": v(-21.4, 9.88) * mm});
            skLineSegment(sketch, "E954", {"start": v(-21.4, 9.88) * mm, "end": v(-21.4, 9.31) * mm});
            skLineSegment(sketch, "E955", {"start": v(-21.4, 9.31) * mm, "end": v(-21.4, 8.74) * mm});
            skLineSegment(sketch, "E956", {"start": v(-21.4, 8.74) * mm, "end": v(-21.4, 8.17) * mm});
            skLineSegment(sketch, "E957", {"start": v(-21.4, 8.17) * mm, "end": v(-21.4, 7.6) * mm});
            skLineSegment(sketch, "E958", {"start": v(-21.4, 7.6) * mm, "end": v(-21.4, 7.04) * mm});
            skLineSegment(sketch, "E959", {"start": v(-21.4, 7.04) * mm, "end": v(-21.4, 6.47) * mm});
            skLineSegment(sketch, "E960", {"start": v(-21.4, 6.47) * mm, "end": v(-21.93, 6.47) * mm});
            skLineSegment(sketch, "E961", {"start": v(-21.93, 6.47) * mm, "end": v(-22.47, 6.47) * mm});
            skLineSegment(sketch, "E962", {"start": v(-22.47, 6.47) * mm, "end": v(-23, 6.47) * mm});
            skLineSegment(sketch, "E963", {"start": v(-23, 6.47) * mm, "end": v(-23.55, 6.47) * mm});
            skLineSegment(sketch, "E964", {"start": v(-23.55, 6.47) * mm, "end": v(-24.08, 6.47) * mm});
            skLineSegment(sketch, "E965", {"start": v(-24.08, 6.47) * mm, "end": v(-24.62, 6.47) * mm});
            skLineSegment(sketch, "E966", {"start": v(-24.62, 6.47) * mm, "end": v(-25.16, 6.47) * mm});
            skLineSegment(sketch, "E967", {"start": v(-25.16, 6.47) * mm, "end": v(-25.7, 6.47) * mm});
            skLineSegment(sketch, "E968", {"start": v(-25.7, 6.47) * mm, "end": v(-25.7, 7.04) * mm});
            skLineSegment(sketch, "E969", {"start": v(-25.7, 7.04) * mm, "end": v(-25.7, 7.6) * mm});
            skLineSegment(sketch, "E970", {"start": v(-25.7, 7.6) * mm, "end": v(-25.7, 8.17) * mm});
            skLineSegment(sketch, "E971", {"start": v(-25.7, 8.17) * mm, "end": v(-25.7, 8.74) * mm});
            skLineSegment(sketch, "E972", {"start": v(-25.7, 8.74) * mm, "end": v(-25.7, 9.31) * mm});
            skLineSegment(sketch, "E973", {"start": v(-25.7, 9.31) * mm, "end": v(-25.7, 9.88) * mm});
            skLineSegment(sketch, "E974", {"start": v(-25.7, 9.88) * mm, "end": v(-25.7, 10.45) * mm});
            skLineSegment(sketch, "E975", {"start": v(-25.7, 10.45) * mm, "end": v(-25.7, 11.02) * mm});
            skLineSegment(sketch, "E976", {"start": v(-25.7, 11.02) * mm, "end": v(-26.1, 11.02) * mm});
            skLineSegment(sketch, "E977", {"start": v(-26.1, 11.02) * mm, "end": v(-26.48, 11.02) * mm});
            skLineSegment(sketch, "E978", {"start": v(-26.48, 11.02) * mm, "end": v(-26.88, 11.02) * mm});
            skLineSegment(sketch, "E979", {"start": v(-26.88, 11.02) * mm, "end": v(-27.27, 11.02) * mm});
            skLineSegment(sketch, "E980", {"start": v(-27.27, 11.02) * mm, "end": v(-27.66, 11.02) * mm});
            skLineSegment(sketch, "E981", {"start": v(-27.66, 11.02) * mm, "end": v(-28.05, 11.02) * mm});
            skLineSegment(sketch, "E982", {"start": v(-28.05, 11.02) * mm, "end": v(-28.45, 11.02) * mm});
            skLineSegment(sketch, "E983", {"start": v(-28.45, 11.02) * mm, "end": v(-28.84, 11.02) * mm});
            skLineSegment(sketch, "E984", {"start": v(-28.84, 11.02) * mm, "end": v(-28.84, 9.54) * mm});
            skLineSegment(sketch, "E985", {"start": v(-28.84, 9.54) * mm, "end": v(-28.84, 8.06) * mm});
            skLineSegment(sketch, "E986", {"start": v(-28.84, 8.06) * mm, "end": v(-28.84, 6.57) * mm});
            skLineSegment(sketch, "E987", {"start": v(-28.84, 6.57) * mm, "end": v(-28.84, 5.1) * mm});
            skLineSegment(sketch, "E988", {"start": v(-28.84, 5.1) * mm, "end": v(-28.84, 3.61) * mm});
            skLineSegment(sketch, "E989", {"start": v(-28.84, 3.61) * mm, "end": v(-28.84, 2.13) * mm});
            skLineSegment(sketch, "E990", {"start": v(-28.84, 2.13) * mm, "end": v(-28.84, 0.65) * mm});
            skLineSegment(sketch, "E991", {"start": v(-28.84, 0.65) * mm, "end": v(-28.84, -0.83) * mm});
            skLineSegment(sketch, "E992", {"start": v(-28.84, -0.83) * mm, "end": v(-29.2, -0.83) * mm});
            skLineSegment(sketch, "E993", {"start": v(-29.2, -0.83) * mm, "end": v(-29.55, -0.83) * mm});
            skLineSegment(sketch, "E994", {"start": v(-29.55, -0.83) * mm, "end": v(-29.9, -0.83) * mm});
            skLineSegment(sketch, "E995", {"start": v(-29.9, -0.83) * mm, "end": v(-30.25, -0.83) * mm});
            skLineSegment(sketch, "E996", {"start": v(-30.25, -0.83) * mm, "end": v(-30.6, -0.83) * mm});
            skLineSegment(sketch, "E997", {"start": v(-30.6, -0.83) * mm, "end": v(-30.96, -0.83) * mm});
            skLineSegment(sketch, "E998", {"start": v(-30.96, -0.83) * mm, "end": v(-31.32, -0.83) * mm});
            skLineSegment(sketch, "E999", {"start": v(-31.32, -0.83) * mm, "end": v(-31.67, -0.83) * mm});
            skLineSegment(sketch, "E1000", {"start": v(-31.67, -0.83) * mm, "end": v(-31.58, -0.8) * mm});
            skLineSegment(sketch, "E1001", {"start": v(-31.58, -0.8) * mm, "end": v(-31.49, -0.75) * mm});
            skLineSegment(sketch, "E1002", {"start": v(-31.49, -0.75) * mm, "end": v(-31.4, -0.7) * mm});
            skLineSegment(sketch, "E1003", {"start": v(-31.4, -0.7) * mm, "end": v(-31.31, -0.65) * mm});
            skLineSegment(sketch, "E1004", {"start": v(-31.31, -0.65) * mm, "end": v(-31.23, -0.6) * mm});
            skLineSegment(sketch, "E1005", {"start": v(-31.23, -0.6) * mm, "end": v(-31.14, -0.55) * mm});
            skLineSegment(sketch, "E1006", {"start": v(-31.14, -0.55) * mm, "end": v(-31.06, -0.5) * mm});
            skLineSegment(sketch, "E1007", {"start": v(-31.06, -0.5) * mm, "end": v(-30.98, -0.44) * mm});
            skLineSegment(sketch, "E1008", {"start": v(-30.98, -0.44) * mm, "end": v(-30.82, -0.32) * mm});
            skLineSegment(sketch, "E1009", {"start": v(-30.82, -0.32) * mm, "end": v(-30.67, -0.2) * mm});
            skLineSegment(sketch, "E1010", {"start": v(-30.67, -0.2) * mm, "end": v(-30.53, -0.06) * mm});
            skLineSegment(sketch, "E1011", {"start": v(-30.53, -0.06) * mm, "end": v(-30.4, 0.08) * mm});
            skLineSegment(sketch, "E1012", {"start": v(-30.4, 0.08) * mm, "end": v(-30.27, 0.24) * mm});
            skLineSegment(sketch, "E1013", {"start": v(-30.27, 0.24) * mm, "end": v(-30.15, 0.4) * mm});
            skLineSegment(sketch, "E1014", {"start": v(-30.15, 0.4) * mm, "end": v(-30.04, 0.57) * mm});
            skLineSegment(sketch, "E1015", {"start": v(-30.04, 0.57) * mm, "end": v(-29.93, 0.74) * mm});
            skLineSegment(sketch, "E1016", {"start": v(-29.93, 0.74) * mm, "end": v(-29.84, 0.93) * mm});
            skLineSegment(sketch, "E1017", {"start": v(-29.84, 0.93) * mm, "end": v(-29.76, 1.13) * mm});
            skLineSegment(sketch, "E1018", {"start": v(-29.76, 1.13) * mm, "end": v(-29.7, 1.34) * mm});
            skLineSegment(sketch, "E1019", {"start": v(-29.7, 1.34) * mm, "end": v(-29.64, 1.56) * mm});
            skLineSegment(sketch, "E1020", {"start": v(-29.64, 1.56) * mm, "end": v(-29.6, 1.79) * mm});
            skLineSegment(sketch, "E1021", {"start": v(-29.6, 1.79) * mm, "end": v(-29.56, 2.02) * mm});
            skLineSegment(sketch, "E1022", {"start": v(-29.56, 2.02) * mm, "end": v(-29.54, 2.27) * mm});
            skLineSegment(sketch, "E1023", {"start": v(-29.54, 2.27) * mm, "end": v(-29.54, 2.53) * mm});
            skLineSegment(sketch, "E1024", {"start": v(-29.54, 2.53) * mm, "end": v(-29.54, 2.74) * mm});
            skLineSegment(sketch, "E1025", {"start": v(-29.54, 2.74) * mm, "end": v(-29.55, 2.94) * mm});
            skLineSegment(sketch, "E1026", {"start": v(-29.55, 2.94) * mm, "end": v(-29.57, 3.13) * mm});
            skLineSegment(sketch, "E1027", {"start": v(-29.57, 3.13) * mm, "end": v(-29.6, 3.32) * mm});
            skLineSegment(sketch, "E1028", {"start": v(-29.6, 3.32) * mm, "end": v(-29.64, 3.5) * mm});
            skLineSegment(sketch, "E1029", {"start": v(-29.64, 3.5) * mm, "end": v(-29.7, 3.68) * mm});
            skLineSegment(sketch, "E1030", {"start": v(-29.7, 3.68) * mm, "end": v(-29.75, 3.84) * mm});
            skLineSegment(sketch, "E1031", {"start": v(-29.75, 3.84) * mm, "end": v(-29.8, 4) * mm});
            skLineSegment(sketch, "E1032", {"start": v(-29.8, 4) * mm, "end": v(-29.88, 4.15) * mm});
            skLineSegment(sketch, "E1033", {"start": v(-29.88, 4.15) * mm, "end": v(-29.96, 4.3) * mm});
            skLineSegment(sketch, "E1034", {"start": v(-29.96, 4.3) * mm, "end": v(-30.05, 4.44) * mm});
            skLineSegment(sketch, "E1035", {"start": v(-30.05, 4.44) * mm, "end": v(-30.14, 4.58) * mm});
            skLineSegment(sketch, "E1036", {"start": v(-30.14, 4.58) * mm, "end": v(-30.24, 4.7) * mm});
            skLineSegment(sketch, "E1037", {"start": v(-30.24, 4.7) * mm, "end": v(-30.35, 4.83) * mm});
            skLineSegment(sketch, "E1038", {"start": v(-30.35, 4.83) * mm, "end": v(-30.47, 4.95) * mm});
            skLineSegment(sketch, "E1039", {"start": v(-30.47, 4.95) * mm, "end": v(-30.6, 5.06) * mm});
            skLineSegment(sketch, "E1040", {"start": v(-30.6, 5.06) * mm, "end": v(-30.72, 5.16) * mm});
            skLineSegment(sketch, "E1041", {"start": v(-30.72, 5.16) * mm, "end": v(-30.85, 5.26) * mm});
            skLineSegment(sketch, "E1042", {"start": v(-30.85, 5.26) * mm, "end": v(-31, 5.36) * mm});
            skLineSegment(sketch, "E1043", {"start": v(-31, 5.36) * mm, "end": v(-31.14, 5.45) * mm});
            skLineSegment(sketch, "E1044", {"start": v(-31.14, 5.45) * mm, "end": v(-31.3, 5.54) * mm});
            skLineSegment(sketch, "E1045", {"start": v(-31.3, 5.54) * mm, "end": v(-31.46, 5.62) * mm});
            skLineSegment(sketch, "E1046", {"start": v(-31.46, 5.62) * mm, "end": v(-31.63, 5.7) * mm});
            skLineSegment(sketch, "E1047", {"start": v(-31.63, 5.7) * mm, "end": v(-31.8, 5.77) * mm});
            skLineSegment(sketch, "E1048", {"start": v(-31.8, 5.77) * mm, "end": v(-31.97, 5.84) * mm});
            skLineSegment(sketch, "E1049", {"start": v(-31.97, 5.84) * mm, "end": v(-32.15, 5.9) * mm});
            skLineSegment(sketch, "E1050", {"start": v(-32.15, 5.9) * mm, "end": v(-32.34, 5.97) * mm});
            skLineSegment(sketch, "E1051", {"start": v(-32.34, 5.97) * mm, "end": v(-32.53, 6.04) * mm});
            skLineSegment(sketch, "E1052", {"start": v(-32.53, 6.04) * mm, "end": v(-32.73, 6.1) * mm});
            skLineSegment(sketch, "E1053", {"start": v(-32.73, 6.1) * mm, "end": v(-32.93, 6.16) * mm});
            skLineSegment(sketch, "E1054", {"start": v(-32.93, 6.16) * mm, "end": v(-33.14, 6.23) * mm});
            skLineSegment(sketch, "E1055", {"start": v(-33.14, 6.23) * mm, "end": v(-33.35, 6.29) * mm});
            skLineSegment(sketch, "E1056", {"start": v(-33.35, 6.29) * mm, "end": v(-33.5, 6.33) * mm});
            skLineSegment(sketch, "E1057", {"start": v(-33.5, 6.33) * mm, "end": v(-33.64, 6.37) * mm});
            skLineSegment(sketch, "E1058", {"start": v(-33.64, 6.37) * mm, "end": v(-33.79, 6.4) * mm});
            skLineSegment(sketch, "E1059", {"start": v(-33.79, 6.4) * mm, "end": v(-33.92, 6.44) * mm});
            skLineSegment(sketch, "E1060", {"start": v(-33.92, 6.44) * mm, "end": v(-34.06, 6.48) * mm});
            skLineSegment(sketch, "E1061", {"start": v(-34.06, 6.48) * mm, "end": v(-34.18, 6.52) * mm});
            skLineSegment(sketch, "E1062", {"start": v(-34.18, 6.52) * mm, "end": v(-34.3, 6.55) * mm});
            skLineSegment(sketch, "E1063", {"start": v(-34.3, 6.55) * mm, "end": v(-34.42, 6.58) * mm});
            skLineSegment(sketch, "E1064", {"start": v(-34.42, 6.58) * mm, "end": v(-34.53, 6.62) * mm});
            skLineSegment(sketch, "E1065", {"start": v(-34.53, 6.62) * mm, "end": v(-34.64, 6.65) * mm});
            skLineSegment(sketch, "E1066", {"start": v(-34.64, 6.65) * mm, "end": v(-34.74, 6.68) * mm});
            skLineSegment(sketch, "E1067", {"start": v(-34.74, 6.68) * mm, "end": v(-34.83, 6.72) * mm});
            skLineSegment(sketch, "E1068", {"start": v(-34.83, 6.72) * mm, "end": v(-34.92, 6.75) * mm});
            skLineSegment(sketch, "E1069", {"start": v(-34.92, 6.75) * mm, "end": v(-35, 6.79) * mm});
            skLineSegment(sketch, "E1070", {"start": v(-35, 6.79) * mm, "end": v(-35.08, 6.82) * mm});
            skLineSegment(sketch, "E1071", {"start": v(-35.08, 6.82) * mm, "end": v(-35.16, 6.86) * mm});
            skLineSegment(sketch, "E1072", {"start": v(-35.16, 6.86) * mm, "end": v(-35.22, 6.9) * mm});
            skLineSegment(sketch, "E1073", {"start": v(-35.22, 6.9) * mm, "end": v(-35.28, 6.93) * mm});
            skLineSegment(sketch, "E1074", {"start": v(-35.28, 6.93) * mm, "end": v(-35.34, 6.97) * mm});
            skLineSegment(sketch, "E1075", {"start": v(-35.34, 6.97) * mm, "end": v(-35.4, 7) * mm});
            skLineSegment(sketch, "E1076", {"start": v(-35.4, 7) * mm, "end": v(-35.44, 7.04) * mm});
            skLineSegment(sketch, "E1077", {"start": v(-35.44, 7.04) * mm, "end": v(-35.48, 7.08) * mm});
            skLineSegment(sketch, "E1078", {"start": v(-35.48, 7.08) * mm, "end": v(-35.52, 7.12) * mm});
            skLineSegment(sketch, "E1079", {"start": v(-35.52, 7.12) * mm, "end": v(-35.56, 7.16) * mm});
            skLineSegment(sketch, "E1080", {"start": v(-35.56, 7.16) * mm, "end": v(-35.59, 7.2) * mm});
            skLineSegment(sketch, "E1081", {"start": v(-35.59, 7.2) * mm, "end": v(-35.6, 7.24) * mm});
            skLineSegment(sketch, "E1082", {"start": v(-35.6, 7.24) * mm, "end": v(-35.63, 7.28) * mm});
            skLineSegment(sketch, "E1083", {"start": v(-35.63, 7.28) * mm, "end": v(-35.64, 7.33) * mm});
            skLineSegment(sketch, "E1084", {"start": v(-35.64, 7.33) * mm, "end": v(-35.66, 7.38) * mm});
            skLineSegment(sketch, "E1085", {"start": v(-35.66, 7.38) * mm, "end": v(-35.67, 7.43) * mm});
            skLineSegment(sketch, "E1086", {"start": v(-35.67, 7.43) * mm, "end": v(-35.67, 7.48) * mm});
            skLineSegment(sketch, "E1087", {"start": v(-35.67, 7.48) * mm, "end": v(-35.67, 7.54) * mm});
            skLineSegment(sketch, "E1088", {"start": v(-35.67, 7.54) * mm, "end": v(-35.67, 7.67) * mm});
            skLineSegment(sketch, "E1089", {"start": v(-35.67, 7.67) * mm, "end": v(-35.63, 7.8) * mm});
            skLineSegment(sketch, "E1090", {"start": v(-35.63, 7.8) * mm, "end": v(-35.57, 7.93) * mm});
            skLineSegment(sketch, "E1091", {"start": v(-35.57, 7.93) * mm, "end": v(-35.47, 8.05) * mm});
            skLineSegment(sketch, "E1092", {"start": v(-35.47, 8.05) * mm, "end": v(-35.3, 8.16) * mm});
            skLineSegment(sketch, "E1093", {"start": v(-35.3, 8.16) * mm, "end": v(-35.09, 8.24) * mm});
            skLineSegment(sketch, "E1094", {"start": v(-35.09, 8.24) * mm, "end": v(-34.79, 8.3) * mm});
            skLineSegment(sketch, "E1095", {"start": v(-34.79, 8.3) * mm, "end": v(-34.41, 8.32) * mm});
            skLineSegment(sketch, "E1096", {"start": v(-34.41, 8.32) * mm, "end": v(-34.29, 8.32) * mm});
            skLineSegment(sketch, "E1097", {"start": v(-34.29, 8.32) * mm, "end": v(-34.16, 8.31) * mm});
            skLineSegment(sketch, "E1098", {"start": v(-34.16, 8.31) * mm, "end": v(-34.03, 8.3) * mm});
            skLineSegment(sketch, "E1099", {"start": v(-34.03, 8.3) * mm, "end": v(-33.9, 8.28) * mm});
            skLineSegment(sketch, "E1100", {"start": v(-33.9, 8.28) * mm, "end": v(-33.78, 8.26) * mm});
            skLineSegment(sketch, "E1101", {"start": v(-33.78, 8.26) * mm, "end": v(-33.66, 8.24) * mm});
            skLineSegment(sketch, "E1102", {"start": v(-33.66, 8.24) * mm, "end": v(-33.53, 8.21) * mm});
            skLineSegment(sketch, "E1103", {"start": v(-33.53, 8.21) * mm, "end": v(-33.4, 8.18) * mm});
            skLineSegment(sketch, "E1104", {"start": v(-33.4, 8.18) * mm, "end": v(-33.27, 8.14) * mm});
            skLineSegment(sketch, "E1105", {"start": v(-33.27, 8.14) * mm, "end": v(-33.15, 8.1) * mm});
            skLineSegment(sketch, "E1106", {"start": v(-33.15, 8.1) * mm, "end": v(-33.03, 8.06) * mm});
            skLineSegment(sketch, "E1107", {"start": v(-33.03, 8.06) * mm, "end": v(-32.9, 8.02) * mm});
            skLineSegment(sketch, "E1108", {"start": v(-32.9, 8.02) * mm, "end": v(-32.79, 7.98) * mm});
            skLineSegment(sketch, "E1109", {"start": v(-32.79, 7.98) * mm, "end": v(-32.67, 7.93) * mm});
            skLineSegment(sketch, "E1110", {"start": v(-32.67, 7.93) * mm, "end": v(-32.56, 7.89) * mm});
            skLineSegment(sketch, "E1111", {"start": v(-32.56, 7.89) * mm, "end": v(-32.45, 7.84) * mm});
            skLineSegment(sketch, "E1112", {"start": v(-32.45, 7.84) * mm, "end": v(-32.34, 7.8) * mm});
            skLineSegment(sketch, "E1113", {"start": v(-32.34, 7.8) * mm, "end": v(-32.24, 7.74) * mm});
            skLineSegment(sketch, "E1114", {"start": v(-32.24, 7.74) * mm, "end": v(-32.15, 7.7) * mm});
            skLineSegment(sketch, "E1115", {"start": v(-32.15, 7.7) * mm, "end": v(-32.05, 7.65) * mm});
            skLineSegment(sketch, "E1116", {"start": v(-32.05, 7.65) * mm, "end": v(-31.96, 7.6) * mm});
            skLineSegment(sketch, "E1117", {"start": v(-31.96, 7.6) * mm, "end": v(-31.88, 7.56) * mm});
            skLineSegment(sketch, "E1118", {"start": v(-31.88, 7.56) * mm, "end": v(-31.8, 7.51) * mm});
            skLineSegment(sketch, "E1119", {"start": v(-31.8, 7.51) * mm, "end": v(-31.73, 7.47) * mm});
            skLineSegment(sketch, "E1120", {"start": v(-31.73, 7.47) * mm, "end": v(-31.65, 7.42) * mm});
            skLineSegment(sketch, "E1121", {"start": v(-31.65, 7.42) * mm, "end": v(-31.59, 7.38) * mm});
            skLineSegment(sketch, "E1122", {"start": v(-31.59, 7.38) * mm, "end": v(-31.54, 7.35) * mm});
            skLineSegment(sketch, "E1123", {"start": v(-31.54, 7.35) * mm, "end": v(-31.5, 7.32) * mm});
            skLineSegment(sketch, "E1124", {"start": v(-31.5, 7.32) * mm, "end": v(-31.47, 7.3) * mm});
            skLineSegment(sketch, "E1125", {"start": v(-31.47, 7.3) * mm, "end": v(-31.45, 7.28) * mm});
            skLineSegment(sketch, "E1126", {"start": v(-31.45, 7.28) * mm, "end": v(-31.44, 7.27) * mm});
            skLineSegment(sketch, "E1127", {"start": v(-31.44, 7.27) * mm, "end": v(-31.43, 7.27) * mm});
            skLineSegment(sketch, "E1128", {"start": v(-31.43, 7.27) * mm, "end": v(-31.4, 7.24) * mm});
            skLineSegment(sketch, "E1129", {"start": v(-31.4, 7.24) * mm, "end": v(-31.39, 7.2) * mm});
            skLineSegment(sketch, "E1130", {"start": v(-31.39, 7.2) * mm, "end": v(-31.36, 7.18) * mm});
            skLineSegment(sketch, "E1131", {"start": v(-31.36, 7.18) * mm, "end": v(-31.34, 7.14) * mm});
            skLineSegment(sketch, "E1132", {"start": v(-31.34, 7.14) * mm, "end": v(-31.32, 7.11) * mm});
            skLineSegment(sketch, "E1133", {"start": v(-31.32, 7.11) * mm, "end": v(-31.3, 7.08) * mm});
            skLineSegment(sketch, "E1134", {"start": v(-31.3, 7.08) * mm, "end": v(-31.27, 7.05) * mm});
            skLineSegment(sketch, "E1135", {"start": v(-31.27, 7.05) * mm, "end": v(-31.25, 7.02) * mm});
            skLineSegment(sketch, "E1136", {"start": v(-31.25, 7.02) * mm, "end": v(-31.07, 7.36) * mm});
            skLineSegment(sketch, "E1137", {"start": v(-31.07, 7.36) * mm, "end": v(-30.9, 7.7) * mm});
            skLineSegment(sketch, "E1138", {"start": v(-30.9, 7.7) * mm, "end": v(-30.71, 8.03) * mm});
            skLineSegment(sketch, "E1139", {"start": v(-30.71, 8.03) * mm, "end": v(-30.53, 8.37) * mm});
            skLineSegment(sketch, "E1140", {"start": v(-30.53, 8.37) * mm, "end": v(-30.35, 8.7) * mm});
            skLineSegment(sketch, "E1141", {"start": v(-30.35, 8.7) * mm, "end": v(-30.18, 9.05) * mm});
            skLineSegment(sketch, "E1142", {"start": v(-30.18, 9.05) * mm, "end": v(-30, 9.38) * mm});
            skLineSegment(sketch, "E1143", {"start": v(-30, 9.38) * mm, "end": v(-29.82, 9.72) * mm});
            skLineSegment(sketch, "E1144", {"start": v(-29.82, 9.72) * mm, "end": v(-29.84, 9.73) * mm});
            skLineSegment(sketch, "E1145", {"start": v(-29.84, 9.73) * mm, "end": v(-29.86, 9.74) * mm});
            skLineSegment(sketch, "E1146", {"start": v(-29.86, 9.74) * mm, "end": v(-29.88, 9.76) * mm});
            skLineSegment(sketch, "E1147", {"start": v(-29.88, 9.76) * mm, "end": v(-29.9, 9.77) * mm});
            skLineSegment(sketch, "E1148", {"start": v(-29.9, 9.77) * mm, "end": v(-29.92, 9.78) * mm});
            skLineSegment(sketch, "E1149", {"start": v(-29.92, 9.78) * mm, "end": v(-29.94, 9.8) * mm});
            skLineSegment(sketch, "E1150", {"start": v(-29.94, 9.8) * mm, "end": v(-29.96, 9.8) * mm});
            skLineSegment(sketch, "E1151", {"start": v(-29.96, 9.8) * mm, "end": v(-29.98, 9.82) * mm});
            skLineSegment(sketch, "E1152", {"start": v(-29.98, 9.82) * mm, "end": v(-30.08, 9.87) * mm});
            skLineSegment(sketch, "E1153", {"start": v(-30.08, 9.87) * mm, "end": v(-30.19, 9.93) * mm});
            skLineSegment(sketch, "E1154", {"start": v(-30.19, 9.93) * mm, "end": v(-30.3, 9.99) * mm});
            skLineSegment(sketch, "E1155", {"start": v(-30.3, 9.99) * mm, "end": v(-30.4, 10.05) * mm});
            skLineSegment(sketch, "E1156", {"start": v(-30.4, 10.05) * mm, "end": v(-30.51, 10.1) * mm});
            skLineSegment(sketch, "E1157", {"start": v(-30.51, 10.1) * mm, "end": v(-30.63, 10.17) * mm});
            skLineSegment(sketch, "E1158", {"start": v(-30.63, 10.17) * mm, "end": v(-30.75, 10.23) * mm});
            skLineSegment(sketch, "E1159", {"start": v(-30.75, 10.23) * mm, "end": v(-30.87, 10.29) * mm});
            skLineSegment(sketch, "E1160", {"start": v(-30.87, 10.29) * mm, "end": v(-30.99, 10.34) * mm});
            skLineSegment(sketch, "E1161", {"start": v(-30.99, 10.34) * mm, "end": v(-31.11, 10.4) * mm});
            skLineSegment(sketch, "E1162", {"start": v(-31.11, 10.4) * mm, "end": v(-31.24, 10.46) * mm});
            skLineSegment(sketch, "E1163", {"start": v(-31.24, 10.46) * mm, "end": v(-31.37, 10.51) * mm});
            skLineSegment(sketch, "E1164", {"start": v(-31.37, 10.51) * mm, "end": v(-31.5, 10.56) * mm});
            skLineSegment(sketch, "E1165", {"start": v(-31.5, 10.56) * mm, "end": v(-31.63, 10.61) * mm});
            skLineSegment(sketch, "E1166", {"start": v(-31.63, 10.61) * mm, "end": v(-31.77, 10.66) * mm});
            skLineSegment(sketch, "E1167", {"start": v(-31.77, 10.66) * mm, "end": v(-31.91, 10.71) * mm});
            skLineSegment(sketch, "E1168", {"start": v(-31.91, 10.71) * mm, "end": v(-32.05, 10.76) * mm});
            skLineSegment(sketch, "E1169", {"start": v(-32.05, 10.76) * mm, "end": v(-32.2, 10.8) * mm});
            skLineSegment(sketch, "E1170", {"start": v(-32.2, 10.8) * mm, "end": v(-32.34, 10.84) * mm});
            skLineSegment(sketch, "E1171", {"start": v(-32.34, 10.84) * mm, "end": v(-32.48, 10.88) * mm});
            skLineSegment(sketch, "E1172", {"start": v(-32.48, 10.88) * mm, "end": v(-32.63, 10.92) * mm});
            skLineSegment(sketch, "E1173", {"start": v(-32.63, 10.92) * mm, "end": v(-32.78, 10.95) * mm});
            skLineSegment(sketch, "E1174", {"start": v(-32.78, 10.95) * mm, "end": v(-32.93, 10.99) * mm});
            skLineSegment(sketch, "E1175", {"start": v(-32.93, 10.99) * mm, "end": v(-33.08, 11.02) * mm});
            skLineSegment(sketch, "E1176", {"start": v(-33.08, 11.02) * mm, "end": v(-33.23, 11.04) * mm});
            skLineSegment(sketch, "E1177", {"start": v(-33.23, 11.04) * mm, "end": v(-33.39, 11.07) * mm});
            skLineSegment(sketch, "E1178", {"start": v(-33.39, 11.07) * mm, "end": v(-33.54, 11.09) * mm});
            skLineSegment(sketch, "E1179", {"start": v(-33.54, 11.09) * mm, "end": v(-33.7, 11.1) * mm});
            skLineSegment(sketch, "E1180", {"start": v(-33.7, 11.1) * mm, "end": v(-33.86, 11.12) * mm});
            skLineSegment(sketch, "E1181", {"start": v(-33.86, 11.12) * mm, "end": v(-34.01, 11.13) * mm});
            skLineSegment(sketch, "E1182", {"start": v(-34.01, 11.13) * mm, "end": v(-34.17, 11.13) * mm});
            skLineSegment(sketch, "E1183", {"start": v(-34.17, 11.13) * mm, "end": v(-34.33, 11.14) * mm});
            skLineSegment(sketch, "E1184", {"start": v(-34.33, 11.14) * mm, "end": v(-34.55, 11.13) * mm});
            skLineSegment(sketch, "E1185", {"start": v(-34.55, 11.13) * mm, "end": v(-34.78, 11.12) * mm});
            skLineSegment(sketch, "E1186", {"start": v(-34.78, 11.12) * mm, "end": v(-35, 11.1) * mm});
            skLineSegment(sketch, "E1187", {"start": v(-35, 11.1) * mm, "end": v(-35.21, 11.07) * mm});
            skLineSegment(sketch, "E1188", {"start": v(-35.21, 11.07) * mm, "end": v(-35.43, 11.03) * mm});
            skLineSegment(sketch, "E1189", {"start": v(-35.43, 11.03) * mm, "end": v(-35.64, 11) * mm});
            skLineSegment(sketch, "E1190", {"start": v(-35.64, 11) * mm, "end": v(-35.85, 10.94) * mm});
            skLineSegment(sketch, "E1191", {"start": v(-35.85, 10.94) * mm, "end": v(-36.05, 10.88) * mm});
            skLineSegment(sketch, "E1192", {"start": v(-36.05, 10.88) * mm, "end": v(-36.26, 10.8) * mm});
            skLineSegment(sketch, "E1193", {"start": v(-36.26, 10.8) * mm, "end": v(-36.45, 10.73) * mm});
            skLineSegment(sketch, "E1194", {"start": v(-36.45, 10.73) * mm, "end": v(-36.64, 10.65) * mm});
            skLineSegment(sketch, "E1195", {"start": v(-36.64, 10.65) * mm, "end": v(-36.83, 10.55) * mm});
            skLineSegment(sketch, "E1196", {"start": v(-36.83, 10.55) * mm, "end": v(-37, 10.45) * mm});
            skLineSegment(sketch, "E1197", {"start": v(-37, 10.45) * mm, "end": v(-37.18, 10.34) * mm});
            skLineSegment(sketch, "E1198", {"start": v(-37.18, 10.34) * mm, "end": v(-37.35, 10.23) * mm});
            skLineSegment(sketch, "E1199", {"start": v(-37.35, 10.23) * mm, "end": v(-37.5, 10.1) * mm});
            skLineSegment(sketch, "E1200", {"start": v(-37.5, 10.1) * mm, "end": v(-37.66, 9.97) * mm});
            skLineSegment(sketch, "E1201", {"start": v(-37.66, 9.97) * mm, "end": v(-37.8, 9.83) * mm});
            skLineSegment(sketch, "E1202", {"start": v(-37.8, 9.83) * mm, "end": v(-37.94, 9.68) * mm});
            skLineSegment(sketch, "E1203", {"start": v(-37.94, 9.68) * mm, "end": v(-38.07, 9.53) * mm});
            skLineSegment(sketch, "E1204", {"start": v(-38.07, 9.53) * mm, "end": v(-38.2, 9.37) * mm});
            skLineSegment(sketch, "E1205", {"start": v(-38.2, 9.37) * mm, "end": v(-38.3, 9.2) * mm});
            skLineSegment(sketch, "E1206", {"start": v(-38.3, 9.2) * mm, "end": v(-38.4, 9.02) * mm});
            skLineSegment(sketch, "E1207", {"start": v(-38.4, 9.02) * mm, "end": v(-38.5, 8.84) * mm});
            skLineSegment(sketch, "E1208", {"start": v(-38.5, 8.84) * mm, "end": v(-38.59, 8.64) * mm});
            skLineSegment(sketch, "E1209", {"start": v(-38.59, 8.64) * mm, "end": v(-38.66, 8.45) * mm});
            skLineSegment(sketch, "E1210", {"start": v(-38.66, 8.45) * mm, "end": v(-38.73, 8.24) * mm});
            skLineSegment(sketch, "E1211", {"start": v(-38.73, 8.24) * mm, "end": v(-38.78, 8.03) * mm});
            skLineSegment(sketch, "E1212", {"start": v(-38.78, 8.03) * mm, "end": v(-38.82, 7.8) * mm});
            skLineSegment(sketch, "E1213", {"start": v(-38.82, 7.8) * mm, "end": v(-38.85, 7.58) * mm});
            skLineSegment(sketch, "E1214", {"start": v(-38.85, 7.58) * mm, "end": v(-38.87, 7.35) * mm});
            skLineSegment(sketch, "E1215", {"start": v(-38.87, 7.35) * mm, "end": v(-38.87, 7.1) * mm});
            skLineSegment(sketch, "E1216", {"start": v(-38.87, 7.1) * mm, "end": v(-38.87, 6.94) * mm});
            skLineSegment(sketch, "E1217", {"start": v(-38.87, 6.94) * mm, "end": v(-38.86, 6.77) * mm});
            skLineSegment(sketch, "E1218", {"start": v(-38.86, 6.77) * mm, "end": v(-38.84, 6.6) * mm});
            skLineSegment(sketch, "E1219", {"start": v(-38.84, 6.6) * mm, "end": v(-38.82, 6.45) * mm});
            skLineSegment(sketch, "E1220", {"start": v(-38.82, 6.45) * mm, "end": v(-38.8, 6.3) * mm});
            skLineSegment(sketch, "E1221", {"start": v(-38.8, 6.3) * mm, "end": v(-38.76, 6.15) * mm});
            skLineSegment(sketch, "E1222", {"start": v(-38.76, 6.15) * mm, "end": v(-38.71, 6.01) * mm});
            skLineSegment(sketch, "E1223", {"start": v(-38.71, 6.01) * mm, "end": v(-38.67, 5.88) * mm});
            skLineSegment(sketch, "E1224", {"start": v(-38.67, 5.88) * mm, "end": v(-38.61, 5.74) * mm});
            skLineSegment(sketch, "E1225", {"start": v(-38.61, 5.74) * mm, "end": v(-38.55, 5.61) * mm});
            skLineSegment(sketch, "E1226", {"start": v(-38.55, 5.61) * mm, "end": v(-38.48, 5.49) * mm});
            skLineSegment(sketch, "E1227", {"start": v(-38.48, 5.49) * mm, "end": v(-38.4, 5.37) * mm});
            skLineSegment(sketch, "E1228", {"start": v(-38.4, 5.37) * mm, "end": v(-38.33, 5.25) * mm});
            skLineSegment(sketch, "E1229", {"start": v(-38.33, 5.25) * mm, "end": v(-38.24, 5.14) * mm});
            skLineSegment(sketch, "E1230", {"start": v(-38.24, 5.14) * mm, "end": v(-38.14, 5.03) * mm});
            skLineSegment(sketch, "E1231", {"start": v(-38.14, 5.03) * mm, "end": v(-38.04, 4.93) * mm});
            skLineSegment(sketch, "E1232", {"start": v(-38.04, 4.93) * mm, "end": v(-37.93, 4.83) * mm});
            skLineSegment(sketch, "E1233", {"start": v(-37.93, 4.83) * mm, "end": v(-37.82, 4.73) * mm});
            skLineSegment(sketch, "E1234", {"start": v(-37.82, 4.73) * mm, "end": v(-37.7, 4.64) * mm});
            skLineSegment(sketch, "E1235", {"start": v(-37.7, 4.64) * mm, "end": v(-37.58, 4.55) * mm});
            skLineSegment(sketch, "E1236", {"start": v(-37.58, 4.55) * mm, "end": v(-37.44, 4.46) * mm});
            skLineSegment(sketch, "E1237", {"start": v(-37.44, 4.46) * mm, "end": v(-37.3, 4.38) * mm});
            skLineSegment(sketch, "E1238", {"start": v(-37.3, 4.38) * mm, "end": v(-37.15, 4.3) * mm});
            skLineSegment(sketch, "E1239", {"start": v(-37.15, 4.3) * mm, "end": v(-37, 4.22) * mm});
            skLineSegment(sketch, "E1240", {"start": v(-37, 4.22) * mm, "end": v(-36.85, 4.14) * mm});
            skLineSegment(sketch, "E1241", {"start": v(-36.85, 4.14) * mm, "end": v(-36.68, 4.07) * mm});
            skLineSegment(sketch, "E1242", {"start": v(-36.68, 4.07) * mm, "end": v(-36.51, 4) * mm});
            skLineSegment(sketch, "E1243", {"start": v(-36.51, 4) * mm, "end": v(-36.34, 3.93) * mm});
            skLineSegment(sketch, "E1244", {"start": v(-36.34, 3.93) * mm, "end": v(-36.15, 3.86) * mm});
            skLineSegment(sketch, "E1245", {"start": v(-36.15, 3.86) * mm, "end": v(-35.96, 3.8) * mm});
            skLineSegment(sketch, "E1246", {"start": v(-35.96, 3.8) * mm, "end": v(-35.77, 3.73) * mm});
            skLineSegment(sketch, "E1247", {"start": v(-35.77, 3.73) * mm, "end": v(-35.56, 3.67) * mm});
            skLineSegment(sketch, "E1248", {"start": v(-35.56, 3.67) * mm, "end": v(-35.42, 3.62) * mm});
            skLineSegment(sketch, "E1249", {"start": v(-35.42, 3.62) * mm, "end": v(-35.28, 3.58) * mm});
            skLineSegment(sketch, "E1250", {"start": v(-35.28, 3.58) * mm, "end": v(-35.13, 3.54) * mm});
            skLineSegment(sketch, "E1251", {"start": v(-35.13, 3.54) * mm, "end": v(-34.99, 3.5) * mm});
            skLineSegment(sketch, "E1252", {"start": v(-34.99, 3.5) * mm, "end": v(-34.85, 3.46) * mm});
            skLineSegment(sketch, "E1253", {"start": v(-34.85, 3.46) * mm, "end": v(-34.7, 3.42) * mm});
            skLineSegment(sketch, "E1254", {"start": v(-34.7, 3.42) * mm, "end": v(-34.56, 3.37) * mm});
            skLineSegment(sketch, "E1255", {"start": v(-34.56, 3.37) * mm, "end": v(-34.42, 3.33) * mm});
            skLineSegment(sketch, "E1256", {"start": v(-34.42, 3.33) * mm, "end": v(-34.3, 3.3) * mm});
            skLineSegment(sketch, "E1257", {"start": v(-34.3, 3.3) * mm, "end": v(-34.18, 3.26) * mm});
            skLineSegment(sketch, "E1258", {"start": v(-34.18, 3.26) * mm, "end": v(-34.06, 3.22) * mm});
            skLineSegment(sketch, "E1259", {"start": v(-34.06, 3.22) * mm, "end": v(-33.95, 3.18) * mm});
            skLineSegment(sketch, "E1260", {"start": v(-33.95, 3.18) * mm, "end": v(-33.84, 3.14) * mm});
            skLineSegment(sketch, "E1261", {"start": v(-33.84, 3.14) * mm, "end": v(-33.74, 3.1) * mm});
            skLineSegment(sketch, "E1262", {"start": v(-33.74, 3.1) * mm, "end": v(-33.64, 3.06) * mm});
            skLineSegment(sketch, "E1263", {"start": v(-33.64, 3.06) * mm, "end": v(-33.55, 3.02) * mm});
            skLineSegment(sketch, "E1264", {"start": v(-33.55, 3.02) * mm, "end": v(-33.46, 2.98) * mm});
            skLineSegment(sketch, "E1265", {"start": v(-33.46, 2.98) * mm, "end": v(-33.38, 2.94) * mm});
            skLineSegment(sketch, "E1266", {"start": v(-33.38, 2.94) * mm, "end": v(-33.3, 2.9) * mm});
            skLineSegment(sketch, "E1267", {"start": v(-33.3, 2.9) * mm, "end": v(-33.24, 2.85) * mm});
            skLineSegment(sketch, "E1268", {"start": v(-33.24, 2.85) * mm, "end": v(-33.17, 2.8) * mm});
            skLineSegment(sketch, "E1269", {"start": v(-33.17, 2.8) * mm, "end": v(-33.11, 2.76) * mm});
            skLineSegment(sketch, "E1270", {"start": v(-33.11, 2.76) * mm, "end": v(-33.06, 2.72) * mm});
            skLineSegment(sketch, "E1271", {"start": v(-33.06, 2.72) * mm, "end": v(-33, 2.67) * mm});
            skLineSegment(sketch, "E1272", {"start": v(-33, 2.67) * mm, "end": v(-32.97, 2.63) * mm});
            skLineSegment(sketch, "E1273", {"start": v(-32.97, 2.63) * mm, "end": v(-32.94, 2.59) * mm});
            skLineSegment(sketch, "E1274", {"start": v(-32.94, 2.59) * mm, "end": v(-32.91, 2.54) * mm});
            skLineSegment(sketch, "E1275", {"start": v(-32.91, 2.54) * mm, "end": v(-32.89, 2.5) * mm});
            skLineSegment(sketch, "E1276", {"start": v(-32.89, 2.5) * mm, "end": v(-32.87, 2.44) * mm});
            skLineSegment(sketch, "E1277", {"start": v(-32.87, 2.44) * mm, "end": v(-32.86, 2.38) * mm});
            skLineSegment(sketch, "E1278", {"start": v(-32.86, 2.38) * mm, "end": v(-32.85, 2.33) * mm});
            skLineSegment(sketch, "E1279", {"start": v(-32.85, 2.33) * mm, "end": v(-32.85, 2.26) * mm});
            skLineSegment(sketch, "E1280", {"start": v(-32.85, 2.26) * mm, "end": v(-32.85, 2.19) * mm});
            skLineSegment(sketch, "E1281", {"start": v(-32.85, 2.19) * mm, "end": v(-32.87, 2.09) * mm});
            skLineSegment(sketch, "E1282", {"start": v(-32.87, 2.09) * mm, "end": v(-32.92, 1.97) * mm});
            skLineSegment(sketch, "E1283", {"start": v(-32.92, 1.97) * mm, "end": v(-33, 1.86) * mm});
            skLineSegment(sketch, "E1284", {"start": v(-33, 1.86) * mm, "end": v(-33.15, 1.75) * mm});
            skLineSegment(sketch, "E1285", {"start": v(-33.15, 1.75) * mm, "end": v(-33.38, 1.66) * mm});
            skLineSegment(sketch, "E1286", {"start": v(-33.38, 1.66) * mm, "end": v(-33.68, 1.6) * mm});
            skLineSegment(sketch, "E1287", {"start": v(-33.68, 1.6) * mm, "end": v(-34.1, 1.58) * mm});
            skLineSegment(sketch, "E1288", {"start": v(-34.1, 1.58) * mm, "end": v(-34.26, 1.58) * mm});
            skLineSegment(sketch, "E1289", {"start": v(-34.26, 1.58) * mm, "end": v(-34.42, 1.6) * mm});
            skLineSegment(sketch, "E1290", {"start": v(-34.42, 1.6) * mm, "end": v(-34.58, 1.6) * mm});
            skLineSegment(sketch, "E1291", {"start": v(-34.58, 1.6) * mm, "end": v(-34.74, 1.63) * mm});
            skLineSegment(sketch, "E1292", {"start": v(-34.74, 1.63) * mm, "end": v(-34.9, 1.65) * mm});
            skLineSegment(sketch, "E1293", {"start": v(-34.9, 1.65) * mm, "end": v(-35.07, 1.68) * mm});
            skLineSegment(sketch, "E1294", {"start": v(-35.07, 1.68) * mm, "end": v(-35.23, 1.72) * mm});
            skLineSegment(sketch, "E1295", {"start": v(-35.23, 1.72) * mm, "end": v(-35.39, 1.76) * mm});
            skLineSegment(sketch, "E1296", {"start": v(-35.39, 1.76) * mm, "end": v(-35.55, 1.8) * mm});
            skLineSegment(sketch, "E1297", {"start": v(-35.55, 1.8) * mm, "end": v(-35.7, 1.85) * mm});
            skLineSegment(sketch, "E1298", {"start": v(-35.7, 1.85) * mm, "end": v(-35.86, 1.9) * mm});
            skLineSegment(sketch, "E1299", {"start": v(-35.86, 1.9) * mm, "end": v(-36, 1.95) * mm});
            skLineSegment(sketch, "E1300", {"start": v(-36, 1.95) * mm, "end": v(-36.15, 2) * mm});
            skLineSegment(sketch, "E1301", {"start": v(-36.15, 2) * mm, "end": v(-36.3, 2.05) * mm});
            skLineSegment(sketch, "E1302", {"start": v(-36.3, 2.05) * mm, "end": v(-36.43, 2.1) * mm});
            skLineSegment(sketch, "E1303", {"start": v(-36.43, 2.1) * mm, "end": v(-36.56, 2.16) * mm});
            skLineSegment(sketch, "E1304", {"start": v(-36.56, 2.16) * mm, "end": v(-36.7, 2.22) * mm});
            skLineSegment(sketch, "E1305", {"start": v(-36.7, 2.22) * mm, "end": v(-36.81, 2.28) * mm});
            skLineSegment(sketch, "E1306", {"start": v(-36.81, 2.28) * mm, "end": v(-36.93, 2.33) * mm});
            skLineSegment(sketch, "E1307", {"start": v(-36.93, 2.33) * mm, "end": v(-37.05, 2.39) * mm});
            skLineSegment(sketch, "E1308", {"start": v(-37.05, 2.39) * mm, "end": v(-37.15, 2.44) * mm});
            skLineSegment(sketch, "E1309", {"start": v(-37.15, 2.44) * mm, "end": v(-37.25, 2.5) * mm});
            skLineSegment(sketch, "E1310", {"start": v(-37.25, 2.5) * mm, "end": v(-37.35, 2.56) * mm});
            skLineSegment(sketch, "E1311", {"start": v(-37.35, 2.56) * mm, "end": v(-37.44, 2.61) * mm});
            skLineSegment(sketch, "E1312", {"start": v(-37.44, 2.61) * mm, "end": v(-37.55, 2.68) * mm});
            skLineSegment(sketch, "E1313", {"start": v(-37.55, 2.68) * mm, "end": v(-37.63, 2.74) * mm});
            skLineSegment(sketch, "E1314", {"start": v(-37.63, 2.74) * mm, "end": v(-37.7, 2.78) * mm});
            skLineSegment(sketch, "E1315", {"start": v(-37.7, 2.78) * mm, "end": v(-37.75, 2.82) * mm});
            skLineSegment(sketch, "E1316", {"start": v(-37.75, 2.82) * mm, "end": v(-37.78, 2.85) * mm});
            skLineSegment(sketch, "E1317", {"start": v(-37.78, 2.85) * mm, "end": v(-37.8, 2.87) * mm});
            skLineSegment(sketch, "E1318", {"start": v(-37.8, 2.87) * mm, "end": v(-37.82, 2.88) * mm});
            skLineSegment(sketch, "E1319", {"start": v(-37.82, 2.88) * mm, "end": v(-37.82, 2.88) * mm});
            skLineSegment(sketch, "E1320", {"start": v(-37.82, 2.88) * mm, "end": v(-37.85, 2.91) * mm});
            skLineSegment(sketch, "E1321", {"start": v(-37.85, 2.91) * mm, "end": v(-37.87, 2.94) * mm});
            skLineSegment(sketch, "E1322", {"start": v(-37.87, 2.94) * mm, "end": v(-37.9, 2.97) * mm});
            skLineSegment(sketch, "E1323", {"start": v(-37.9, 2.97) * mm, "end": v(-37.92, 3) * mm});
            skLineSegment(sketch, "E1324", {"start": v(-37.92, 3) * mm, "end": v(-37.94, 3.04) * mm});
            skLineSegment(sketch, "E1325", {"start": v(-37.94, 3.04) * mm, "end": v(-37.97, 3.07) * mm});
            skLineSegment(sketch, "E1326", {"start": v(-37.97, 3.07) * mm, "end": v(-38, 3.1) * mm});
            skLineSegment(sketch, "E1327", {"start": v(-38, 3.1) * mm, "end": v(-38.01, 3.13) * mm});
            skLineSegment(sketch, "E1328", {"start": v(-38.01, 3.13) * mm, "end": v(-38.2, 2.78) * mm});
            skLineSegment(sketch, "E1329", {"start": v(-38.2, 2.78) * mm, "end": v(-38.37, 2.43) * mm});
            skLineSegment(sketch, "E1330", {"start": v(-38.37, 2.43) * mm, "end": v(-38.54, 2.07) * mm});
            skLineSegment(sketch, "E1331", {"start": v(-38.54, 2.07) * mm, "end": v(-38.72, 1.72) * mm});
            skLineSegment(sketch, "E1332", {"start": v(-38.72, 1.72) * mm, "end": v(-38.9, 1.37) * mm});
            skLineSegment(sketch, "E1333", {"start": v(-38.9, 1.37) * mm, "end": v(-39.07, 1.02) * mm});
            skLineSegment(sketch, "E1334", {"start": v(-39.07, 1.02) * mm, "end": v(-39.25, 0.67) * mm});
            skLineSegment(sketch, "E1335", {"start": v(-39.25, 0.67) * mm, "end": v(-39.43, 0.32) * mm});
            skLineSegment(sketch, "E1336", {"start": v(-39.43, 0.32) * mm, "end": v(-39.4, 0.31) * mm});
            skLineSegment(sketch, "E1337", {"start": v(-39.4, 0.31) * mm, "end": v(-39.39, 0.3) * mm});
            skLineSegment(sketch, "E1338", {"start": v(-39.39, 0.3) * mm, "end": v(-39.37, 0.29) * mm});
            skLineSegment(sketch, "E1339", {"start": v(-39.37, 0.29) * mm, "end": v(-39.35, 0.27) * mm});
            skLineSegment(sketch, "E1340", {"start": v(-39.35, 0.27) * mm, "end": v(-39.34, 0.26) * mm});
            skLineSegment(sketch, "E1341", {"start": v(-39.34, 0.26) * mm, "end": v(-39.32, 0.25) * mm});
            skLineSegment(sketch, "E1342", {"start": v(-39.32, 0.25) * mm, "end": v(-39.3, 0.24) * mm});
            skLineSegment(sketch, "E1343", {"start": v(-39.3, 0.24) * mm, "end": v(-39.28, 0.23) * mm});
            skLineSegment(sketch, "E1344", {"start": v(-39.28, 0.23) * mm, "end": v(-39.15, 0.14) * mm});
            skLineSegment(sketch, "E1345", {"start": v(-39.15, 0.14) * mm, "end": v(-39.01, 0.05) * mm});
            skLineSegment(sketch, "E1346", {"start": v(-39.01, 0.05) * mm, "end": v(-38.87, -0.04) * mm});
            skLineSegment(sketch, "E1347", {"start": v(-38.87, -0.04) * mm, "end": v(-38.73, -0.12) * mm});
            skLineSegment(sketch, "E1348", {"start": v(-38.73, -0.12) * mm, "end": v(-38.58, -0.2) * mm});
            skLineSegment(sketch, "E1349", {"start": v(-38.58, -0.2) * mm, "end": v(-38.43, -0.28) * mm});
            skLineSegment(sketch, "E1350", {"start": v(-38.43, -0.28) * mm, "end": v(-38.28, -0.35) * mm});
            skLineSegment(sketch, "E1351", {"start": v(-38.28, -0.35) * mm, "end": v(-38.13, -0.42) * mm});
            skLineSegment(sketch, "E1352", {"start": v(-38.13, -0.42) * mm, "end": v(-38, -0.48) * mm});
            skLineSegment(sketch, "E1353", {"start": v(-38, -0.48) * mm, "end": v(-37.87, -0.53) * mm});
            skLineSegment(sketch, "E1354", {"start": v(-37.87, -0.53) * mm, "end": v(-37.73, -0.59) * mm});
            skLineSegment(sketch, "E1355", {"start": v(-37.73, -0.59) * mm, "end": v(-37.6, -0.64) * mm});
            skLineSegment(sketch, "E1356", {"start": v(-37.6, -0.64) * mm, "end": v(-37.46, -0.7) * mm});
            skLineSegment(sketch, "E1357", {"start": v(-37.46, -0.7) * mm, "end": v(-37.33, -0.75) * mm});
            skLineSegment(sketch, "E1358", {"start": v(-37.33, -0.75) * mm, "end": v(-37.2, -0.8) * mm});
            skLineSegment(sketch, "E1359", {"start": v(-37.2, -0.8) * mm, "end": v(-37.05, -0.83) * mm});
            skLineSegment(sketch, "E1360", {"start": v(-37.05, -0.83) * mm, "end": v(-37.65, -0.83) * mm});
            skLineSegment(sketch, "E1361", {"start": v(-37.65, -0.83) * mm, "end": v(-38.25, -0.83) * mm});
            skLineSegment(sketch, "E1362", {"start": v(-38.25, -0.83) * mm, "end": v(-38.85, -0.83) * mm});
            skLineSegment(sketch, "E1363", {"start": v(-38.85, -0.83) * mm, "end": v(-39.45, -0.83) * mm});
            skLineSegment(sketch, "E1364", {"start": v(-39.45, -0.83) * mm, "end": v(-40.05, -0.83) * mm});
            skLineSegment(sketch, "E1365", {"start": v(-40.05, -0.83) * mm, "end": v(-40.65, -0.83) * mm});
            skLineSegment(sketch, "E1366", {"start": v(-40.65, -0.83) * mm, "end": v(-41.25, -0.83) * mm});
            skLineSegment(sketch, "E1367", {"start": v(-41.25, -0.83) * mm, "end": v(-41.85, -0.83) * mm});
            skLineSegment(sketch, "E1368", {"start": v(-41.85, -0.83) * mm, "end": v(-41.73, -0.78) * mm});
            skLineSegment(sketch, "E1369", {"start": v(-41.73, -0.78) * mm, "end": v(-41.6, -0.73) * mm});
            skLineSegment(sketch, "E1370", {"start": v(-41.6, -0.73) * mm, "end": v(-41.48, -0.67) * mm});
            skLineSegment(sketch, "E1371", {"start": v(-41.48, -0.67) * mm, "end": v(-41.36, -0.61) * mm});
            skLineSegment(sketch, "E1372", {"start": v(-41.36, -0.61) * mm, "end": v(-41.24, -0.55) * mm});
            skLineSegment(sketch, "E1373", {"start": v(-41.24, -0.55) * mm, "end": v(-41.13, -0.5) * mm});
            skLineSegment(sketch, "E1374", {"start": v(-41.13, -0.5) * mm, "end": v(-41.02, -0.42) * mm});
            skLineSegment(sketch, "E1375", {"start": v(-41.02, -0.42) * mm, "end": v(-40.91, -0.36) * mm});
            skLineSegment(sketch, "E1376", {"start": v(-40.91, -0.36) * mm, "end": v(-40.77, -0.25) * mm});
            skLineSegment(sketch, "E1377", {"start": v(-40.77, -0.25) * mm, "end": v(-40.64, -0.14) * mm});
            skLineSegment(sketch, "E1378", {"start": v(-40.64, -0.14) * mm, "end": v(-40.51, -0.03) * mm});
            skLineSegment(sketch, "E1379", {"start": v(-40.51, -0.03) * mm, "end": v(-40.4, 0.1) * mm});
            skLineSegment(sketch, "E1380", {"start": v(-40.4, 0.1) * mm, "end": v(-40.28, 0.23) * mm});
            skLineSegment(sketch, "E1381", {"start": v(-40.28, 0.23) * mm, "end": v(-40.18, 0.36) * mm});
            skLineSegment(sketch, "E1382", {"start": v(-40.18, 0.36) * mm, "end": v(-40.08, 0.5) * mm});
            skLineSegment(sketch, "E1383", {"start": v(-40.08, 0.5) * mm, "end": v(-40, 0.65) * mm});
            skLineSegment(sketch, "E1384", {"start": v(-40, 0.65) * mm, "end": v(-39.91, 0.8) * mm});
            skLineSegment(sketch, "E1385", {"start": v(-39.91, 0.8) * mm, "end": v(-39.84, 0.97) * mm});
            skLineSegment(sketch, "E1386", {"start": v(-39.84, 0.97) * mm, "end": v(-39.78, 1.14) * mm});
            skLineSegment(sketch, "E1387", {"start": v(-39.78, 1.14) * mm, "end": v(-39.74, 1.31) * mm});
            skLineSegment(sketch, "E1388", {"start": v(-39.74, 1.31) * mm, "end": v(-39.7, 1.5) * mm});
            skLineSegment(sketch, "E1389", {"start": v(-39.7, 1.5) * mm, "end": v(-39.67, 1.68) * mm});
            skLineSegment(sketch, "E1390", {"start": v(-39.67, 1.68) * mm, "end": v(-39.66, 1.88) * mm});
            skLineSegment(sketch, "E1391", {"start": v(-39.66, 1.88) * mm, "end": v(-39.65, 2.08) * mm});
            skLineSegment(sketch, "E1392", {"start": v(-39.65, 2.08) * mm, "end": v(-39.66, 2.39) * mm});
            skLineSegment(sketch, "E1393", {"start": v(-39.66, 2.39) * mm, "end": v(-39.7, 2.68) * mm});
            skLineSegment(sketch, "E1394", {"start": v(-39.7, 2.68) * mm, "end": v(-39.74, 2.96) * mm});
            skLineSegment(sketch, "E1395", {"start": v(-39.74, 2.96) * mm, "end": v(-39.8, 3.23) * mm});
            skLineSegment(sketch, "E1396", {"start": v(-39.8, 3.23) * mm, "end": v(-39.9, 3.48) * mm});
            skLineSegment(sketch, "E1397", {"start": v(-39.9, 3.48) * mm, "end": v(-40, 3.72) * mm});
            skLineSegment(sketch, "E1398", {"start": v(-40, 3.72) * mm, "end": v(-40.13, 3.95) * mm});
            skLineSegment(sketch, "E1399", {"start": v(-40.13, 3.95) * mm, "end": v(-40.28, 4.16) * mm});
            skLineSegment(sketch, "E1400", {"start": v(-40.28, 4.16) * mm, "end": v(-40.4, 4.31) * mm});
            skLineSegment(sketch, "E1401", {"start": v(-40.4, 4.31) * mm, "end": v(-40.55, 4.46) * mm});
            skLineSegment(sketch, "E1402", {"start": v(-40.55, 4.46) * mm, "end": v(-40.7, 4.6) * mm});
            skLineSegment(sketch, "E1403", {"start": v(-40.7, 4.6) * mm, "end": v(-40.85, 4.72) * mm});
            skLineSegment(sketch, "E1404", {"start": v(-40.85, 4.72) * mm, "end": v(-41.01, 4.84) * mm});
            skLineSegment(sketch, "E1405", {"start": v(-41.01, 4.84) * mm, "end": v(-41.18, 4.95) * mm});
            skLineSegment(sketch, "E1406", {"start": v(-41.18, 4.95) * mm, "end": v(-41.36, 5.05) * mm});
            skLineSegment(sketch, "E1407", {"start": v(-41.36, 5.05) * mm, "end": v(-41.55, 5.13) * mm});
            skLineSegment(sketch, "E1408", {"start": v(-41.55, 5.13) * mm, "end": v(-41.4, 5.23) * mm});
            skLineSegment(sketch, "E1409", {"start": v(-41.4, 5.23) * mm, "end": v(-41.27, 5.34) * mm});
            skLineSegment(sketch, "E1410", {"start": v(-41.27, 5.34) * mm, "end": v(-41.13, 5.45) * mm});
            skLineSegment(sketch, "E1411", {"start": v(-41.13, 5.45) * mm, "end": v(-41, 5.58) * mm});
            skLineSegment(sketch, "E1412", {"start": v(-41, 5.58) * mm, "end": v(-40.9, 5.7) * mm});
            skLineSegment(sketch, "E1413", {"start": v(-40.9, 5.7) * mm, "end": v(-40.79, 5.84) * mm});
            skLineSegment(sketch, "E1414", {"start": v(-40.79, 5.84) * mm, "end": v(-40.69, 5.98) * mm});
            skLineSegment(sketch, "E1415", {"start": v(-40.69, 5.98) * mm, "end": v(-40.6, 6.13) * mm});
            skLineSegment(sketch, "E1416", {"start": v(-40.6, 6.13) * mm, "end": v(-40.5, 6.33) * mm});
            skLineSegment(sketch, "E1417", {"start": v(-40.5, 6.33) * mm, "end": v(-40.4, 6.53) * mm});
            skLineSegment(sketch, "E1418", {"start": v(-40.4, 6.53) * mm, "end": v(-40.32, 6.74) * mm});
            skLineSegment(sketch, "E1419", {"start": v(-40.32, 6.74) * mm, "end": v(-40.26, 6.95) * mm});
            skLineSegment(sketch, "E1420", {"start": v(-40.26, 6.95) * mm, "end": v(-40.21, 7.16) * mm});
            skLineSegment(sketch, "E1421", {"start": v(-40.21, 7.16) * mm, "end": v(-40.18, 7.38) * mm});
            skLineSegment(sketch, "E1422", {"start": v(-40.18, 7.38) * mm, "end": v(-40.16, 7.6) * mm});
            skLineSegment(sketch, "E1423", {"start": v(-40.16, 7.6) * mm, "end": v(-40.15, 7.82) * mm});
            skLineSegment(sketch, "E1424", {"start": v(-40.15, 7.82) * mm, "end": v(-40.15, 7.97) * mm});
            skLineSegment(sketch, "E1425", {"start": v(-40.15, 7.97) * mm, "end": v(-40.16, 8.12) * mm});
            skLineSegment(sketch, "E1426", {"start": v(-40.16, 8.12) * mm, "end": v(-40.18, 8.26) * mm});
            skLineSegment(sketch, "E1427", {"start": v(-40.18, 8.26) * mm, "end": v(-40.2, 8.41) * mm});
            skLineSegment(sketch, "E1428", {"start": v(-40.2, 8.41) * mm, "end": v(-40.23, 8.56) * mm});
            skLineSegment(sketch, "E1429", {"start": v(-40.23, 8.56) * mm, "end": v(-40.26, 8.7) * mm});
            skLineSegment(sketch, "E1430", {"start": v(-40.26, 8.7) * mm, "end": v(-40.3, 8.85) * mm});
            skLineSegment(sketch, "E1431", {"start": v(-40.3, 8.85) * mm, "end": v(-40.35, 8.99) * mm});
            skLineSegment(sketch, "E1432", {"start": v(-40.35, 8.99) * mm, "end": v(-40.4, 9.13) * mm});
            skLineSegment(sketch, "E1433", {"start": v(-40.4, 9.13) * mm, "end": v(-40.46, 9.27) * mm});
            skLineSegment(sketch, "E1434", {"start": v(-40.46, 9.27) * mm, "end": v(-40.53, 9.4) * mm});
            skLineSegment(sketch, "E1435", {"start": v(-40.53, 9.4) * mm, "end": v(-40.6, 9.53) * mm});
            skLineSegment(sketch, "E1436", {"start": v(-40.6, 9.53) * mm, "end": v(-40.67, 9.66) * mm});
            skLineSegment(sketch, "E1437", {"start": v(-40.67, 9.66) * mm, "end": v(-40.75, 9.78) * mm});
            skLineSegment(sketch, "E1438", {"start": v(-40.75, 9.78) * mm, "end": v(-40.83, 9.9) * mm});
            skLineSegment(sketch, "E1439", {"start": v(-40.83, 9.9) * mm, "end": v(-40.92, 10.01) * mm});
            skLineSegment(sketch, "E1440", {"start": v(-40.92, 10.01) * mm, "end": v(-41.02, 10.12) * mm});
            skLineSegment(sketch, "E1441", {"start": v(-41.02, 10.12) * mm, "end": v(-41.12, 10.23) * mm});
            skLineSegment(sketch, "E1442", {"start": v(-41.12, 10.23) * mm, "end": v(-41.23, 10.32) * mm});
            skLineSegment(sketch, "E1443", {"start": v(-41.23, 10.32) * mm, "end": v(-41.34, 10.42) * mm});
            skLineSegment(sketch, "E1444", {"start": v(-41.34, 10.42) * mm, "end": v(-41.45, 10.5) * mm});
            skLineSegment(sketch, "E1445", {"start": v(-41.45, 10.5) * mm, "end": v(-41.57, 10.59) * mm});
            skLineSegment(sketch, "E1446", {"start": v(-41.57, 10.59) * mm, "end": v(-41.7, 10.67) * mm});
            skLineSegment(sketch, "E1447", {"start": v(-41.7, 10.67) * mm, "end": v(-41.83, 10.74) * mm});
            skLineSegment(sketch, "E1448", {"start": v(-41.83, 10.74) * mm, "end": v(-41.97, 10.8) * mm});
            skLineSegment(sketch, "E1449", {"start": v(-41.97, 10.8) * mm, "end": v(-42.1, 10.86) * mm});
            skLineSegment(sketch, "E1450", {"start": v(-42.1, 10.86) * mm, "end": v(-42.25, 10.91) * mm});
            skLineSegment(sketch, "E1451", {"start": v(-42.25, 10.91) * mm, "end": v(-42.4, 10.95) * mm});
            skLineSegment(sketch, "E1452", {"start": v(-42.4, 10.95) * mm, "end": v(-42.55, 10.98) * mm});
            skLineSegment(sketch, "E1453", {"start": v(-42.55, 10.98) * mm, "end": v(-42.7, 11) * mm});
            skLineSegment(sketch, "E1454", {"start": v(-42.7, 11) * mm, "end": v(-42.87, 11.01) * mm});
            skLineSegment(sketch, "E1455", {"start": v(-42.87, 11.01) * mm, "end": v(-43.03, 11.02) * mm});
            skLineSegment(sketch, "E1456", {"start": v(-43.03, 11.02) * mm, "end": v(-43.88, 11.02) * mm});
            skLineSegment(sketch, "E1457", {"start": v(-43.88, 11.02) * mm, "end": v(-44.72, 11.02) * mm});
            skLineSegment(sketch, "E1458", {"start": v(-44.72, 11.02) * mm, "end": v(-45.57, 11.02) * mm});
            skLineSegment(sketch, "E1459", {"start": v(-45.57, 11.02) * mm, "end": v(-46.41, 11.02) * mm});
            skLineSegment(sketch, "E1460", {"start": v(-46.41, 11.02) * mm, "end": v(-47.26, 11.02) * mm});
            skLineSegment(sketch, "E1461", {"start": v(-47.26, 11.02) * mm, "end": v(-48.1, 11.02) * mm});
            skLineSegment(sketch, "E1462", {"start": v(-48.1, 11.02) * mm, "end": v(-48.95, 11.02) * mm});
            skLineSegment(sketch, "E1463", {"start": v(-48.95, 11.02) * mm, "end": v(-49.8, 11.02) * mm});
            skLineSegment(sketch, "E1464", {"start": v(-49.8, 11.02) * mm, "end": v(-49.8, 9.54) * mm});
            skLineSegment(sketch, "E1465", {"start": v(-49.8, 9.54) * mm, "end": v(-49.8, 8.06) * mm});
            skLineSegment(sketch, "E1466", {"start": v(-49.8, 8.06) * mm, "end": v(-49.8, 6.57) * mm});
            skLineSegment(sketch, "E1467", {"start": v(-49.8, 6.57) * mm, "end": v(-49.8, 5.1) * mm});
            skLineSegment(sketch, "E1468", {"start": v(-49.8, 5.1) * mm, "end": v(-49.8, 3.61) * mm});
            skLineSegment(sketch, "E1469", {"start": v(-49.8, 3.61) * mm, "end": v(-49.8, 2.13) * mm});
            skLineSegment(sketch, "E1470", {"start": v(-49.8, 2.13) * mm, "end": v(-49.8, 0.65) * mm});
            skLineSegment(sketch, "E1471", {"start": v(-49.8, 0.65) * mm, "end": v(-49.8, -0.83) * mm});
            skLineSegment(sketch, "E1472", {"start": v(-49.8, -0.83) * mm, "end": v(-49.88, -0.83) * mm});
            skLineSegment(sketch, "E1473", {"start": v(-49.88, -0.83) * mm, "end": v(-49.96, -0.83) * mm});
            skLineSegment(sketch, "E1474", {"start": v(-49.96, -0.83) * mm, "end": v(-50.04, -0.83) * mm});
            skLineSegment(sketch, "E1475", {"start": v(-50.04, -0.83) * mm, "end": v(-50.13, -0.83) * mm});
            skLineSegment(sketch, "E1476", {"start": v(-50.13, -0.83) * mm, "end": v(-50.21, -0.83) * mm});
            skLineSegment(sketch, "E1477", {"start": v(-50.21, -0.83) * mm, "end": v(-50.3, -0.83) * mm});
            skLineSegment(sketch, "E1478", {"start": v(-50.3, -0.83) * mm, "end": v(-50.38, -0.83) * mm});
            skLineSegment(sketch, "E1479", {"start": v(-50.38, -0.83) * mm, "end": v(-50.46, -0.83) * mm});
            skLineSegment(sketch, "E1480", {"start": v(-50.46, -0.83) * mm, "end": v(-50.46, -0.53) * mm});
            skLineSegment(sketch, "E1481", {"start": v(-50.46, -0.53) * mm, "end": v(-50.46, -0.22) * mm});
            skLineSegment(sketch, "E1482", {"start": v(-50.46, -0.22) * mm, "end": v(-50.46, 0.1) * mm});
            skLineSegment(sketch, "E1483", {"start": v(-50.46, 0.1) * mm, "end": v(-50.46, 0.4) * mm});
            skLineSegment(sketch, "E1484", {"start": v(-50.46, 0.4) * mm, "end": v(-50.46, 0.7) * mm});
            skLineSegment(sketch, "E1485", {"start": v(-50.46, 0.7) * mm, "end": v(-50.46, 1.02) * mm});
            skLineSegment(sketch, "E1486", {"start": v(-50.46, 1.02) * mm, "end": v(-50.46, 1.33) * mm});
            skLineSegment(sketch, "E1487", {"start": v(-50.46, 1.33) * mm, "end": v(-50.46, 1.63) * mm});
            skLineSegment(sketch, "E1488", {"start": v(-50.46, 1.63) * mm, "end": v(-51.16, 1.63) * mm});
            skLineSegment(sketch, "E1489", {"start": v(-51.16, 1.63) * mm, "end": v(-51.87, 1.63) * mm});
            skLineSegment(sketch, "E1490", {"start": v(-51.87, 1.63) * mm, "end": v(-52.57, 1.63) * mm});
            skLineSegment(sketch, "E1491", {"start": v(-52.57, 1.63) * mm, "end": v(-53.27, 1.63) * mm});
            skLineSegment(sketch, "E1492", {"start": v(-53.27, 1.63) * mm, "end": v(-53.97, 1.63) * mm});
            skLineSegment(sketch, "E1493", {"start": v(-53.97, 1.63) * mm, "end": v(-54.67, 1.63) * mm});
            skLineSegment(sketch, "E1494", {"start": v(-54.67, 1.63) * mm, "end": v(-55.37, 1.63) * mm});
            skLineSegment(sketch, "E1495", {"start": v(-55.37, 1.63) * mm, "end": v(-56.07, 1.63) * mm});
            skLineSegment(sketch, "E1496", {"start": v(-56.07, 1.63) * mm, "end": v(-56.07, 1.9) * mm});
            skLineSegment(sketch, "E1497", {"start": v(-56.07, 1.9) * mm, "end": v(-56.07, 2.16) * mm});
            skLineSegment(sketch, "E1498", {"start": v(-56.07, 2.16) * mm, "end": v(-56.07, 2.43) * mm});
            skLineSegment(sketch, "E1499", {"start": v(-56.07, 2.43) * mm, "end": v(-56.07, 2.7) * mm});
            skLineSegment(sketch, "E1500", {"start": v(-56.07, 2.7) * mm, "end": v(-56.07, 2.96) * mm});
            skLineSegment(sketch, "E1501", {"start": v(-56.07, 2.96) * mm, "end": v(-56.07, 3.22) * mm});
            skLineSegment(sketch, "E1502", {"start": v(-56.07, 3.22) * mm, "end": v(-56.07, 3.49) * mm});
            skLineSegment(sketch, "E1503", {"start": v(-56.07, 3.49) * mm, "end": v(-56.07, 3.75) * mm});
            skLineSegment(sketch, "E1504", {"start": v(-56.07, 3.75) * mm, "end": v(-55.5, 3.75) * mm});
            skLineSegment(sketch, "E1505", {"start": v(-55.5, 3.75) * mm, "end": v(-54.9, 3.75) * mm});
            skLineSegment(sketch, "E1506", {"start": v(-54.9, 3.75) * mm, "end": v(-54.33, 3.75) * mm});
            skLineSegment(sketch, "E1507", {"start": v(-54.33, 3.75) * mm, "end": v(-53.74, 3.75) * mm});
            skLineSegment(sketch, "E1508", {"start": v(-53.74, 3.75) * mm, "end": v(-53.16, 3.75) * mm});
            skLineSegment(sketch, "E1509", {"start": v(-53.16, 3.75) * mm, "end": v(-52.58, 3.75) * mm});
            skLineSegment(sketch, "E1510", {"start": v(-52.58, 3.75) * mm, "end": v(-52, 3.75) * mm});
            skLineSegment(sketch, "E1511", {"start": v(-52, 3.75) * mm, "end": v(-51.42, 3.75) * mm});
            skLineSegment(sketch, "E1512", {"start": v(-51.42, 3.75) * mm, "end": v(-51.42, 4.08) * mm});
            skLineSegment(sketch, "E1513", {"start": v(-51.42, 4.08) * mm, "end": v(-51.42, 4.4) * mm});
            skLineSegment(sketch, "E1514", {"start": v(-51.42, 4.4) * mm, "end": v(-51.42, 4.73) * mm});
            skLineSegment(sketch, "E1515", {"start": v(-51.42, 4.73) * mm, "end": v(-51.42, 5.06) * mm});
            skLineSegment(sketch, "E1516", {"start": v(-51.42, 5.06) * mm, "end": v(-51.42, 5.38) * mm});
            skLineSegment(sketch, "E1517", {"start": v(-51.42, 5.38) * mm, "end": v(-51.42, 5.7) * mm});
            skLineSegment(sketch, "E1518", {"start": v(-51.42, 5.7) * mm, "end": v(-51.42, 6.04) * mm});
            skLineSegment(sketch, "E1519", {"start": v(-51.42, 6.04) * mm, "end": v(-51.42, 6.36) * mm});
            skLineSegment(sketch, "E1520", {"start": v(-51.42, 6.36) * mm, "end": v(-52, 6.36) * mm});
            skLineSegment(sketch, "E1521", {"start": v(-52, 6.36) * mm, "end": v(-52.58, 6.36) * mm});
            skLineSegment(sketch, "E1522", {"start": v(-52.58, 6.36) * mm, "end": v(-53.16, 6.36) * mm});
            skLineSegment(sketch, "E1523", {"start": v(-53.16, 6.36) * mm, "end": v(-53.74, 6.36) * mm});
            skLineSegment(sketch, "E1524", {"start": v(-53.74, 6.36) * mm, "end": v(-54.33, 6.36) * mm});
            skLineSegment(sketch, "E1525", {"start": v(-54.33, 6.36) * mm, "end": v(-54.9, 6.36) * mm});
            skLineSegment(sketch, "E1526", {"start": v(-54.9, 6.36) * mm, "end": v(-55.5, 6.36) * mm});
            skLineSegment(sketch, "E1527", {"start": v(-55.5, 6.36) * mm, "end": v(-56.07, 6.36) * mm});
            skLineSegment(sketch, "E1528", {"start": v(-56.07, 6.36) * mm, "end": v(-56.07, 6.6) * mm});
            skLineSegment(sketch, "E1529", {"start": v(-56.07, 6.6) * mm, "end": v(-56.07, 6.82) * mm});
            skLineSegment(sketch, "E1530", {"start": v(-56.07, 6.82) * mm, "end": v(-56.07, 7.05) * mm});
            skLineSegment(sketch, "E1531", {"start": v(-56.07, 7.05) * mm, "end": v(-56.07, 7.28) * mm});
            skLineSegment(sketch, "E1532", {"start": v(-56.07, 7.28) * mm, "end": v(-56.07, 7.5) * mm});
            skLineSegment(sketch, "E1533", {"start": v(-56.07, 7.5) * mm, "end": v(-56.07, 7.74) * mm});
            skLineSegment(sketch, "E1534", {"start": v(-56.07, 7.74) * mm, "end": v(-56.07, 7.97) * mm});
            skLineSegment(sketch, "E1535", {"start": v(-56.07, 7.97) * mm, "end": v(-56.07, 8.2) * mm});
            skLineSegment(sketch, "E1536", {"start": v(-56.07, 8.2) * mm, "end": v(-55.4, 8.2) * mm});
            skLineSegment(sketch, "E1537", {"start": v(-55.4, 8.2) * mm, "end": v(-54.72, 8.2) * mm});
            skLineSegment(sketch, "E1538", {"start": v(-54.72, 8.2) * mm, "end": v(-54.05, 8.2) * mm});
            skLineSegment(sketch, "E1539", {"start": v(-54.05, 8.2) * mm, "end": v(-53.37, 8.2) * mm});
            skLineSegment(sketch, "E1540", {"start": v(-53.37, 8.2) * mm, "end": v(-52.7, 8.2) * mm});
            skLineSegment(sketch, "E1541", {"start": v(-52.7, 8.2) * mm, "end": v(-52.02, 8.2) * mm});
            skLineSegment(sketch, "E1542", {"start": v(-52.02, 8.2) * mm, "end": v(-51.35, 8.2) * mm});
            skLineSegment(sketch, "E1543", {"start": v(-51.35, 8.2) * mm, "end": v(-50.67, 8.2) * mm});
            skLineSegment(sketch, "E1544", {"start": v(-50.67, 8.2) * mm, "end": v(-50.67, 8.55) * mm});
            skLineSegment(sketch, "E1545", {"start": v(-50.67, 8.55) * mm, "end": v(-50.67, 8.9) * mm});
            skLineSegment(sketch, "E1546", {"start": v(-50.67, 8.9) * mm, "end": v(-50.67, 9.25) * mm});
            skLineSegment(sketch, "E1547", {"start": v(-50.67, 9.25) * mm, "end": v(-50.67, 9.6) * mm});
            skLineSegment(sketch, "E1548", {"start": v(-50.67, 9.6) * mm, "end": v(-50.67, 9.96) * mm});
            skLineSegment(sketch, "E1549", {"start": v(-50.67, 9.96) * mm, "end": v(-50.67, 10.31) * mm});
            skLineSegment(sketch, "E1550", {"start": v(-50.67, 10.31) * mm, "end": v(-50.67, 10.67) * mm});
            skLineSegment(sketch, "E1551", {"start": v(-50.67, 10.67) * mm, "end": v(-50.67, 11.02) * mm});
            skLineSegment(sketch, "E1552", {"start": v(-50.67, 11.02) * mm, "end": v(-51.73, 11.02) * mm});
            skLineSegment(sketch, "E1553", {"start": v(-51.73, 11.02) * mm, "end": v(-52.78, 11.02) * mm});
            skLineSegment(sketch, "E1554", {"start": v(-52.78, 11.02) * mm, "end": v(-53.84, 11.02) * mm});
            skLineSegment(sketch, "E1555", {"start": v(-53.84, 11.02) * mm, "end": v(-54.9, 11.02) * mm});
            skLineSegment(sketch, "E1556", {"start": v(-54.9, 11.02) * mm, "end": v(-55.94, 11.02) * mm});
            skLineSegment(sketch, "E1557", {"start": v(-55.94, 11.02) * mm, "end": v(-57, 11.02) * mm});
            skLineSegment(sketch, "E1558", {"start": v(-57, 11.02) * mm, "end": v(-58.05, 11.02) * mm});
            skLineSegment(sketch, "E1559", {"start": v(-58.05, 11.02) * mm, "end": v(-59.1, 11.02) * mm});
            skLineSegment(sketch, "E1560", {"start": v(-59.1, 11.02) * mm, "end": v(-59.1, 9.54) * mm});
            skLineSegment(sketch, "E1561", {"start": v(-59.1, 9.54) * mm, "end": v(-59.1, 8.06) * mm});
            skLineSegment(sketch, "E1562", {"start": v(-59.1, 8.06) * mm, "end": v(-59.1, 6.57) * mm});
            skLineSegment(sketch, "E1563", {"start": v(-59.1, 6.57) * mm, "end": v(-59.1, 5.1) * mm});
            skLineSegment(sketch, "E1564", {"start": v(-59.1, 5.1) * mm, "end": v(-59.1, 3.61) * mm});
            skLineSegment(sketch, "E1565", {"start": v(-59.1, 3.61) * mm, "end": v(-59.1, 2.13) * mm});
            skLineSegment(sketch, "E1566", {"start": v(-59.1, 2.13) * mm, "end": v(-59.1, 0.65) * mm});
            skLineSegment(sketch, "E1567", {"start": v(-59.1, 0.65) * mm, "end": v(-59.1, -0.83) * mm});
            skLineSegment(sketch, "E1568", {"start": v(-59.1, -0.83) * mm, "end": v(-59.8, -0.83) * mm});
            skLineSegment(sketch, "E1569", {"start": v(-59.8, -0.83) * mm, "end": v(-60.48, -0.83) * mm});
            skLineSegment(sketch, "E1570", {"start": v(-60.48, -0.83) * mm, "end": v(-61.17, -0.83) * mm});
            skLineSegment(sketch, "E1571", {"start": v(-61.17, -0.83) * mm, "end": v(-61.85, -0.83) * mm});
            skLineSegment(sketch, "E1572", {"start": v(-61.85, -0.83) * mm, "end": v(-62.54, -0.83) * mm});
            skLineSegment(sketch, "E1573", {"start": v(-62.54, -0.83) * mm, "end": v(-63.22, -0.83) * mm});
            skLineSegment(sketch, "E1574", {"start": v(-63.22, -0.83) * mm, "end": v(-63.91, -0.83) * mm});
            skLineSegment(sketch, "E1575", {"start": v(-63.91, -0.83) * mm, "end": v(-64.6, -0.83) * mm});
            skLineSegment(sketch, "E1576", {"start": v(-64.6, -0.83) * mm, "end": v(-64, 0.65) * mm});
            skLineSegment(sketch, "E1577", {"start": v(-64, 0.65) * mm, "end": v(-63.41, 2.13) * mm});
            skLineSegment(sketch, "E1578", {"start": v(-63.41, 2.13) * mm, "end": v(-62.82, 3.61) * mm});
            skLineSegment(sketch, "E1579", {"start": v(-62.82, 3.61) * mm, "end": v(-62.23, 5.1) * mm});
            skLineSegment(sketch, "E1580", {"start": v(-62.23, 5.1) * mm, "end": v(-61.63, 6.57) * mm});
            skLineSegment(sketch, "E1581", {"start": v(-61.63, 6.57) * mm, "end": v(-61.04, 8.06) * mm});
            skLineSegment(sketch, "E1582", {"start": v(-61.04, 8.06) * mm, "end": v(-60.45, 9.54) * mm});
            skLineSegment(sketch, "E1583", {"start": v(-60.45, 9.54) * mm, "end": v(-59.85, 11.02) * mm});
            skLineSegment(sketch, "E1584", {"start": v(-59.85, 11.02) * mm, "end": v(-60.28, 11.02) * mm});
            skLineSegment(sketch, "E1585", {"start": v(-60.28, 11.02) * mm, "end": v(-60.7, 11.02) * mm});
            skLineSegment(sketch, "E1586", {"start": v(-60.7, 11.02) * mm, "end": v(-61.13, 11.02) * mm});
            skLineSegment(sketch, "E1587", {"start": v(-61.13, 11.02) * mm, "end": v(-61.55, 11.02) * mm});
            skLineSegment(sketch, "E1588", {"start": v(-61.55, 11.02) * mm, "end": v(-61.98, 11.02) * mm});
            skLineSegment(sketch, "E1589", {"start": v(-61.98, 11.02) * mm, "end": v(-62.4, 11.02) * mm});
            skLineSegment(sketch, "E1590", {"start": v(-62.4, 11.02) * mm, "end": v(-62.83, 11.02) * mm});
            skLineSegment(sketch, "E1591", {"start": v(-62.83, 11.02) * mm, "end": v(-63.26, 11.02) * mm});
            skLineSegment(sketch, "E1592", {"start": v(-63.26, 11.02) * mm, "end": v(-63.6, 9.99) * mm});
            skLineSegment(sketch, "E1593", {"start": v(-63.6, 9.99) * mm, "end": v(-63.96, 8.95) * mm});
            skLineSegment(sketch, "E1594", {"start": v(-63.96, 8.95) * mm, "end": v(-64.31, 7.92) * mm});
            skLineSegment(sketch, "E1595", {"start": v(-64.31, 7.92) * mm, "end": v(-64.67, 6.89) * mm});
            skLineSegment(sketch, "E1596", {"start": v(-64.67, 6.89) * mm, "end": v(-65.02, 5.85) * mm});
            skLineSegment(sketch, "E1597", {"start": v(-65.02, 5.85) * mm, "end": v(-65.37, 4.82) * mm});
            skLineSegment(sketch, "E1598", {"start": v(-65.37, 4.82) * mm, "end": v(-65.72, 3.79) * mm});
            skLineSegment(sketch, "E1599", {"start": v(-65.72, 3.79) * mm, "end": v(-66.08, 2.76) * mm});
            skLineSegment(sketch, "E1600", {"start": v(-66.08, 2.76) * mm, "end": v(-66.2, 3.08) * mm});
            skLineSegment(sketch, "E1601", {"start": v(-66.2, 3.08) * mm, "end": v(-66.32, 3.4) * mm});
            skLineSegment(sketch, "E1602", {"start": v(-66.32, 3.4) * mm, "end": v(-66.44, 3.72) * mm});
            skLineSegment(sketch, "E1603", {"start": v(-66.44, 3.72) * mm, "end": v(-66.56, 4.04) * mm});
            skLineSegment(sketch, "E1604", {"start": v(-66.56, 4.04) * mm, "end": v(-66.69, 4.36) * mm});
            skLineSegment(sketch, "E1605", {"start": v(-66.69, 4.36) * mm, "end": v(-66.8, 4.68) * mm});
            skLineSegment(sketch, "E1606", {"start": v(-66.8, 4.68) * mm, "end": v(-66.93, 5) * mm});
            skLineSegment(sketch, "E1607", {"start": v(-66.93, 5) * mm, "end": v(-67.05, 5.33) * mm});
            skLineSegment(sketch, "E1608", {"start": v(-67.05, 5.33) * mm, "end": v(-66.8, 6.03) * mm});
            skLineSegment(sketch, "E1609", {"start": v(-66.8, 6.03) * mm, "end": v(-66.54, 6.74) * mm});
            skLineSegment(sketch, "E1610", {"start": v(-66.54, 6.74) * mm, "end": v(-66.28, 7.45) * mm});
            skLineSegment(sketch, "E1611", {"start": v(-66.28, 7.45) * mm, "end": v(-66.03, 8.16) * mm});
            skLineSegment(sketch, "E1612", {"start": v(-66.03, 8.16) * mm, "end": v(-65.77, 8.86) * mm});
            skLineSegment(sketch, "E1613", {"start": v(-65.77, 8.86) * mm, "end": v(-65.52, 9.57) * mm});
            skLineSegment(sketch, "E1614", {"start": v(-65.52, 9.57) * mm, "end": v(-65.26, 10.28) * mm});
            skLineSegment(sketch, "E1615", {"start": v(-65.26, 10.28) * mm, "end": v(-65, 10.98) * mm});
            skLineSegment(sketch, "E1616", {"start": v(-65, 10.98) * mm, "end": v(-65.37, 10.98) * mm});
            skLineSegment(sketch, "E1617", {"start": v(-65.37, 10.98) * mm, "end": v(-65.74, 10.98) * mm});
            skLineSegment(sketch, "E1618", {"start": v(-65.74, 10.98) * mm, "end": v(-66.11, 10.98) * mm});
            skLineSegment(sketch, "E1619", {"start": v(-66.11, 10.98) * mm, "end": v(-66.48, 10.98) * mm});
            skLineSegment(sketch, "E1620", {"start": v(-66.48, 10.98) * mm, "end": v(-66.85, 10.98) * mm});
            skLineSegment(sketch, "E1621", {"start": v(-66.85, 10.98) * mm, "end": v(-67.22, 10.98) * mm});
            skLineSegment(sketch, "E1622", {"start": v(-67.22, 10.98) * mm, "end": v(-67.58, 10.98) * mm});
            skLineSegment(sketch, "E1623", {"start": v(-67.58, 10.98) * mm, "end": v(-67.95, 10.98) * mm});
            skLineSegment(sketch, "E1624", {"start": v(-67.95, 10.98) * mm, "end": v(-68.08, 10.57) * mm});
            skLineSegment(sketch, "E1625", {"start": v(-68.08, 10.57) * mm, "end": v(-68.22, 10.16) * mm});
            skLineSegment(sketch, "E1626", {"start": v(-68.22, 10.16) * mm, "end": v(-68.35, 9.74) * mm});
            skLineSegment(sketch, "E1627", {"start": v(-68.35, 9.74) * mm, "end": v(-68.48, 9.33) * mm});
            skLineSegment(sketch, "E1628", {"start": v(-68.48, 9.33) * mm, "end": v(-68.6, 8.91) * mm});
            skLineSegment(sketch, "E1629", {"start": v(-68.6, 8.91) * mm, "end": v(-68.74, 8.5) * mm});
            skLineSegment(sketch, "E1630", {"start": v(-68.74, 8.5) * mm, "end": v(-68.87, 8.09) * mm});
            skLineSegment(sketch, "E1631", {"start": v(-68.87, 8.09) * mm, "end": v(-69, 7.67) * mm});
            skLineSegment(sketch, "E1632", {"start": v(-69, 7.67) * mm, "end": v(-69.13, 8.09) * mm});
            skLineSegment(sketch, "E1633", {"start": v(-69.13, 8.09) * mm, "end": v(-69.27, 8.5) * mm});
            skLineSegment(sketch, "E1634", {"start": v(-69.27, 8.5) * mm, "end": v(-69.4, 8.91) * mm});
            skLineSegment(sketch, "E1635", {"start": v(-69.4, 8.91) * mm, "end": v(-69.53, 9.33) * mm});
            skLineSegment(sketch, "E1636", {"start": v(-69.53, 9.33) * mm, "end": v(-69.66, 9.74) * mm});
            skLineSegment(sketch, "E1637", {"start": v(-69.66, 9.74) * mm, "end": v(-69.8, 10.16) * mm});
            skLineSegment(sketch, "E1638", {"start": v(-69.8, 10.16) * mm, "end": v(-69.92, 10.57) * mm});
            skLineSegment(sketch, "E1639", {"start": v(-69.92, 10.57) * mm, "end": v(-70.05, 10.98) * mm});
            skLineSegment(sketch, "E1640", {"start": v(-70.05, 10.98) * mm, "end": v(-70.42, 10.98) * mm});
            skLineSegment(sketch, "E1641", {"start": v(-70.42, 10.98) * mm, "end": v(-70.78, 10.98) * mm});
            skLineSegment(sketch, "E1642", {"start": v(-70.78, 10.98) * mm, "end": v(-71.15, 10.98) * mm});
            skLineSegment(sketch, "E1643", {"start": v(-71.15, 10.98) * mm, "end": v(-71.52, 10.98) * mm});
            skLineSegment(sketch, "E1644", {"start": v(-71.52, 10.98) * mm, "end": v(-71.88, 10.98) * mm});
            skLineSegment(sketch, "E1645", {"start": v(-71.88, 10.98) * mm, "end": v(-72.25, 10.98) * mm});
            skLineSegment(sketch, "E1646", {"start": v(-72.25, 10.98) * mm, "end": v(-72.62, 10.98) * mm});
            skLineSegment(sketch, "E1647", {"start": v(-72.62, 10.98) * mm, "end": v(-72.98, 10.98) * mm});
            skLineSegment(sketch, "E1648", {"start": v(-72.98, 10.98) * mm, "end": v(-72.73, 10.28) * mm});
            skLineSegment(sketch, "E1649", {"start": v(-72.73, 10.28) * mm, "end": v(-72.48, 9.57) * mm});
            skLineSegment(sketch, "E1650", {"start": v(-72.48, 9.57) * mm, "end": v(-72.23, 8.86) * mm});
            skLineSegment(sketch, "E1651", {"start": v(-72.23, 8.86) * mm, "end": v(-71.98, 8.16) * mm});
            skLineSegment(sketch, "E1652", {"start": v(-71.98, 8.16) * mm, "end": v(-71.72, 7.45) * mm});
            skLineSegment(sketch, "E1653", {"start": v(-71.72, 7.45) * mm, "end": v(-71.47, 6.74) * mm});
            skLineSegment(sketch, "E1654", {"start": v(-71.47, 6.74) * mm, "end": v(-71.22, 6.04) * mm});
            skLineSegment(sketch, "E1655", {"start": v(-71.22, 6.04) * mm, "end": v(-70.97, 5.33) * mm});
            skLineSegment(sketch, "E1656", {"start": v(-70.97, 5.33) * mm, "end": v(-71.09, 5) * mm});
            skLineSegment(sketch, "E1657", {"start": v(-71.09, 5) * mm, "end": v(-71.2, 4.69) * mm});
            skLineSegment(sketch, "E1658", {"start": v(-71.2, 4.69) * mm, "end": v(-71.33, 4.36) * mm});
            skLineSegment(sketch, "E1659", {"start": v(-71.33, 4.36) * mm, "end": v(-71.44, 4.04) * mm});
            skLineSegment(sketch, "E1660", {"start": v(-71.44, 4.04) * mm, "end": v(-71.56, 3.72) * mm});
            skLineSegment(sketch, "E1661", {"start": v(-71.56, 3.72) * mm, "end": v(-71.68, 3.4) * mm});
            skLineSegment(sketch, "E1662", {"start": v(-71.68, 3.4) * mm, "end": v(-71.8, 3.08) * mm});
            skLineSegment(sketch, "E1663", {"start": v(-71.8, 3.08) * mm, "end": v(-71.92, 2.75) * mm});
            skLineSegment(sketch, "E1664", {"start": v(-71.92, 2.75) * mm, "end": v(-72.27, 3.79) * mm});
            skLineSegment(sketch, "E1665", {"start": v(-72.27, 3.79) * mm, "end": v(-72.62, 4.82) * mm});
            skLineSegment(sketch, "E1666", {"start": v(-72.62, 4.82) * mm, "end": v(-72.98, 5.85) * mm});
            skLineSegment(sketch, "E1667", {"start": v(-72.98, 5.85) * mm, "end": v(-73.33, 6.89) * mm});
            skLineSegment(sketch, "E1668", {"start": v(-73.33, 6.89) * mm, "end": v(-73.69, 7.92) * mm});
            skLineSegment(sketch, "E1669", {"start": v(-73.69, 7.92) * mm, "end": v(-74.04, 8.95) * mm});
            skLineSegment(sketch, "E1670", {"start": v(-74.04, 8.95) * mm, "end": v(-74.4, 9.99) * mm});
            skLineSegment(sketch, "E1671", {"start": v(-74.4, 9.99) * mm, "end": v(-74.75, 11.02) * mm});
            skLineSegment(sketch, "E1672", {"start": v(-74.75, 11.02) * mm, "end": v(-75.17, 11.02) * mm});
            skLineSegment(sketch, "E1673", {"start": v(-75.17, 11.02) * mm, "end": v(-75.6, 11.02) * mm});
            skLineSegment(sketch, "E1674", {"start": v(-75.6, 11.02) * mm, "end": v(-76.02, 11.02) * mm});
            skLineSegment(sketch, "E1675", {"start": v(-76.02, 11.02) * mm, "end": v(-76.44, 11.02) * mm});
            skLineSegment(sketch, "E1676", {"start": v(-76.44, 11.02) * mm, "end": v(-76.87, 11.02) * mm});
            skLineSegment(sketch, "E1677", {"start": v(-76.87, 11.02) * mm, "end": v(-77.29, 11.02) * mm});
            skLineSegment(sketch, "E1678", {"start": v(-77.29, 11.02) * mm, "end": v(-77.71, 11.02) * mm});
            skLineSegment(sketch, "E1679", {"start": v(-77.71, 11.02) * mm, "end": v(-78.14, 11.02) * mm});
            skLineSegment(sketch, "E1680", {"start": v(-78.14, 11.02) * mm, "end": v(-77.54, 9.54) * mm});
            skLineSegment(sketch, "E1681", {"start": v(-77.54, 9.54) * mm, "end": v(-76.95, 8.06) * mm});
            skLineSegment(sketch, "E1682", {"start": v(-76.95, 8.06) * mm, "end": v(-76.36, 6.57) * mm});
            skLineSegment(sketch, "E1683", {"start": v(-76.36, 6.57) * mm, "end": v(-75.77, 5.1) * mm});
            skLineSegment(sketch, "E1684", {"start": v(-75.77, 5.1) * mm, "end": v(-75.18, 3.61) * mm});
            skLineSegment(sketch, "E1685", {"start": v(-75.18, 3.61) * mm, "end": v(-74.6, 2.13) * mm});
            skLineSegment(sketch, "E1686", {"start": v(-74.6, 2.13) * mm, "end": v(-74, 0.65) * mm});
            skLineSegment(sketch, "E1687", {"start": v(-74, 0.65) * mm, "end": v(-73.4, -0.83) * mm});
            skLineSegment(sketch, "E1688", {"start": v(-73.4, -0.83) * mm, "end": v(-74.21, -0.83) * mm});
            skLineSegment(sketch, "E1689", {"start": v(-74.21, -0.83) * mm, "end": v(-75.02, -0.83) * mm});
            skLineSegment(sketch, "E1690", {"start": v(-75.02, -0.83) * mm, "end": v(-75.82, -0.83) * mm});
            skLineSegment(sketch, "E1691", {"start": v(-75.82, -0.83) * mm, "end": v(-76.62, -0.83) * mm});
            skLineSegment(sketch, "E1692", {"start": v(-76.62, -0.83) * mm, "end": v(-77.43, -0.83) * mm});
            skLineSegment(sketch, "E1693", {"start": v(-77.43, -0.83) * mm, "end": v(-78.23, -0.83) * mm});
            skLineSegment(sketch, "E1694", {"start": v(-78.23, -0.83) * mm, "end": v(-79.04, -0.83) * mm});
            skLineSegment(sketch, "E1695", {"start": v(-79.04, -0.83) * mm, "end": v(-79.84, -0.83) * mm});
            skLineSegment(sketch, "E1696", {"start": v(-79.84, -0.83) * mm, "end": v(-80.88, -0.94) * mm});
            skLineSegment(sketch, "E1697", {"start": v(-80.88, -0.94) * mm, "end": v(-81.85, -1.24) * mm});
            skLineSegment(sketch, "E1698", {"start": v(-81.85, -1.24) * mm, "end": v(-82.72, -1.71) * mm});
            skLineSegment(sketch, "E1699", {"start": v(-82.72, -1.71) * mm, "end": v(-83.49, -2.34) * mm});
            skLineSegment(sketch, "E1700", {"start": v(-83.49, -2.34) * mm, "end": v(-84.12, -3.1) * mm});
            skLineSegment(sketch, "E1701", {"start": v(-84.12, -3.1) * mm, "end": v(-84.6, -3.98) * mm});
            skLineSegment(sketch, "E1702", {"start": v(-84.6, -3.98) * mm, "end": v(-84.9, -4.95) * mm});
            skLineSegment(sketch, "E1703", {"start": v(-84.9, -4.95) * mm, "end": v(-85, -5.99) * mm});
            skLineSegment(sketch, "E1704", {"start": v(-85, -5.99) * mm, "end": v(-84.9, -7.02) * mm});
            skLineSegment(sketch, "E1705", {"start": v(-84.9, -7.02) * mm, "end": v(-84.6, -8) * mm});
            skLineSegment(sketch, "E1706", {"start": v(-84.6, -8) * mm, "end": v(-84.12, -8.87) * mm});
            skLineSegment(sketch, "E1707", {"start": v(-84.12, -8.87) * mm, "end": v(-83.49, -9.63) * mm});
            skLineSegment(sketch, "E1708", {"start": v(-83.49, -9.63) * mm, "end": v(-82.72, -10.26) * mm});
            skLineSegment(sketch, "E1709", {"start": v(-82.72, -10.26) * mm, "end": v(-81.85, -10.73) * mm});
            skLineSegment(sketch, "E1710", {"start": v(-81.85, -10.73) * mm, "end": v(-80.88, -11.03) * mm});
            skLineSegment(sketch, "E1711", {"start": v(-80.88, -11.03) * mm, "end": v(-79.84, -11.14) * mm});
            skLineSegment(sketch, "E1712", {"start": v(-79.84, -11.14) * mm, "end": v(-59.88, -11.14) * mm});
            skLineSegment(sketch, "E1713", {"start": v(-59.88, -11.14) * mm, "end": v(-39.92, -11.14) * mm});
            skLineSegment(sketch, "E1714", {"start": v(-39.92, -11.14) * mm, "end": v(-19.96, -11.14) * mm});
            skLineSegment(sketch, "E1715", {"start": v(-19.96, -11.14) * mm, "end": v(0, -11.14) * mm});
            skLineSegment(sketch, "E1716", {"start": v(0, -11.14) * mm, "end": v(19.96, -11.14) * mm});
            skLineSegment(sketch, "E1717", {"start": v(19.96, -11.14) * mm, "end": v(39.92, -11.14) * mm});
            skLineSegment(sketch, "E1718", {"start": v(39.92, -11.14) * mm, "end": v(59.88, -11.14) * mm});
            skLineSegment(sketch, "E1719", {"start": v(59.88, -11.14) * mm, "end": v(79.84, -11.14) * mm});
            skLineSegment(sketch, "E1720", {"start": v(79.84, -11.14) * mm, "end": v(80.88, -11.03) * mm});
            skLineSegment(sketch, "E1721", {"start": v(80.88, -11.03) * mm, "end": v(81.85, -10.73) * mm});
            skLineSegment(sketch, "E1722", {"start": v(81.85, -10.73) * mm, "end": v(82.72, -10.26) * mm});
            skLineSegment(sketch, "E1723", {"start": v(82.72, -10.26) * mm, "end": v(83.49, -9.63) * mm});
            skLineSegment(sketch, "E1724", {"start": v(83.49, -9.63) * mm, "end": v(84.12, -8.87) * mm});
            skLineSegment(sketch, "E1725", {"start": v(84.12, -8.87) * mm, "end": v(84.6, -8) * mm});
            skLineSegment(sketch, "E1726", {"start": v(84.6, -8) * mm, "end": v(84.9, -7.02) * mm});
            skLineSegment(sketch, "E1727", {"start": v(84.9, -7.02) * mm, "end": v(85, -5.99) * mm});
            skLineSegment(sketch, "E1728", {"start": v(85, -5.99) * mm, "end": v(84.9, -4.95) * mm});
            skLineSegment(sketch, "E1729", {"start": v(84.9, -4.95) * mm, "end": v(84.6, -3.98) * mm});
            skLineSegment(sketch, "E1730", {"start": v(84.6, -3.98) * mm, "end": v(84.12, -3.1) * mm});
            skLineSegment(sketch, "E1731", {"start": v(84.12, -3.1) * mm, "end": v(83.49, -2.34) * mm});
            skLineSegment(sketch, "E1732", {"start": v(83.49, -2.34) * mm, "end": v(82.72, -1.71) * mm});
            skLineSegment(sketch, "E1733", {"start": v(82.72, -1.71) * mm, "end": v(81.85, -1.24) * mm});
            skLineSegment(sketch, "E1734", {"start": v(81.85, -1.24) * mm, "end": v(80.88, -0.94) * mm});
            skLineSegment(sketch, "E1735", {"start": v(80.88, -0.94) * mm, "end": v(79.84, -0.83) * mm});
            skLineSegment(sketch, "E1736", {"start": v(18.96, 3.67) * mm, "end": v(18.91, 3.83) * mm});
            skLineSegment(sketch, "E1737", {"start": v(18.91, 3.83) * mm, "end": v(18.87, 3.98) * mm});
            skLineSegment(sketch, "E1738", {"start": v(18.87, 3.98) * mm, "end": v(18.84, 4.14) * mm});
            skLineSegment(sketch, "E1739", {"start": v(18.84, 4.14) * mm, "end": v(18.82, 4.3) * mm});
            skLineSegment(sketch, "E1740", {"start": v(18.82, 4.3) * mm, "end": v(18.8, 4.45) * mm});
            skLineSegment(sketch, "E1741", {"start": v(18.8, 4.45) * mm, "end": v(18.78, 4.61) * mm});
            skLineSegment(sketch, "E1742", {"start": v(18.78, 4.61) * mm, "end": v(18.77, 4.77) * mm});
            skLineSegment(sketch, "E1743", {"start": v(18.77, 4.77) * mm, "end": v(18.77, 4.93) * mm});
            skLineSegment(sketch, "E1744", {"start": v(18.77, 4.93) * mm, "end": v(18.77, 5.1) * mm});
            skLineSegment(sketch, "E1745", {"start": v(18.77, 5.1) * mm, "end": v(18.78, 5.25) * mm});
            skLineSegment(sketch, "E1746", {"start": v(18.78, 5.25) * mm, "end": v(18.8, 5.4) * mm});
            skLineSegment(sketch, "E1747", {"start": v(18.8, 5.4) * mm, "end": v(18.81, 5.56) * mm});
            skLineSegment(sketch, "E1748", {"start": v(18.81, 5.56) * mm, "end": v(18.84, 5.72) * mm});
            skLineSegment(sketch, "E1749", {"start": v(18.84, 5.72) * mm, "end": v(18.87, 5.87) * mm});
            skLineSegment(sketch, "E1750", {"start": v(18.87, 5.87) * mm, "end": v(18.9, 6.03) * mm});
            skLineSegment(sketch, "E1751", {"start": v(18.9, 6.03) * mm, "end": v(18.95, 6.18) * mm});
            skLineSegment(sketch, "E1752", {"start": v(18.95, 6.18) * mm, "end": v(19, 6.33) * mm});
            skLineSegment(sketch, "E1753", {"start": v(19, 6.33) * mm, "end": v(19.05, 6.47) * mm});
            skLineSegment(sketch, "E1754", {"start": v(19.05, 6.47) * mm, "end": v(19.11, 6.61) * mm});
            skLineSegment(sketch, "E1755", {"start": v(19.11, 6.61) * mm, "end": v(19.18, 6.75) * mm});
            skLineSegment(sketch, "E1756", {"start": v(19.18, 6.75) * mm, "end": v(19.25, 6.88) * mm});
            skLineSegment(sketch, "E1757", {"start": v(19.25, 6.88) * mm, "end": v(19.32, 7) * mm});
            skLineSegment(sketch, "E1758", {"start": v(19.32, 7) * mm, "end": v(19.4, 7.13) * mm});
            skLineSegment(sketch, "E1759", {"start": v(19.4, 7.13) * mm, "end": v(19.5, 7.25) * mm});
            skLineSegment(sketch, "E1760", {"start": v(19.5, 7.25) * mm, "end": v(19.59, 7.36) * mm});
            skLineSegment(sketch, "E1761", {"start": v(19.59, 7.36) * mm, "end": v(19.69, 7.47) * mm});
            skLineSegment(sketch, "E1762", {"start": v(19.69, 7.47) * mm, "end": v(19.8, 7.57) * mm});
            skLineSegment(sketch, "E1763", {"start": v(19.8, 7.57) * mm, "end": v(19.9, 7.67) * mm});
            skLineSegment(sketch, "E1764", {"start": v(19.9, 7.67) * mm, "end": v(20.02, 7.76) * mm});
            skLineSegment(sketch, "E1765", {"start": v(20.02, 7.76) * mm, "end": v(20.14, 7.85) * mm});
            skLineSegment(sketch, "E1766", {"start": v(20.14, 7.85) * mm, "end": v(20.27, 7.93) * mm});
            skLineSegment(sketch, "E1767", {"start": v(20.27, 7.93) * mm, "end": v(20.4, 8) * mm});
            skLineSegment(sketch, "E1768", {"start": v(20.4, 8) * mm, "end": v(20.53, 8.07) * mm});
            skLineSegment(sketch, "E1769", {"start": v(20.53, 8.07) * mm, "end": v(20.67, 8.13) * mm});
            skLineSegment(sketch, "E1770", {"start": v(20.67, 8.13) * mm, "end": v(20.82, 8.18) * mm});
            skLineSegment(sketch, "E1771", {"start": v(20.82, 8.18) * mm, "end": v(20.98, 8.22) * mm});
            skLineSegment(sketch, "E1772", {"start": v(20.98, 8.22) * mm, "end": v(21.14, 8.25) * mm});
            skLineSegment(sketch, "E1773", {"start": v(21.14, 8.25) * mm, "end": v(21.3, 8.27) * mm});
            skLineSegment(sketch, "E1774", {"start": v(21.3, 8.27) * mm, "end": v(21.48, 8.28) * mm});
            skLineSegment(sketch, "E1775", {"start": v(21.48, 8.28) * mm, "end": v(21.65, 8.29) * mm});
            skLineSegment(sketch, "E1776", {"start": v(21.65, 8.29) * mm, "end": v(21.83, 8.28) * mm});
            skLineSegment(sketch, "E1777", {"start": v(21.83, 8.28) * mm, "end": v(22, 8.27) * mm});
            skLineSegment(sketch, "E1778", {"start": v(22, 8.27) * mm, "end": v(22.15, 8.25) * mm});
            skLineSegment(sketch, "E1779", {"start": v(22.15, 8.25) * mm, "end": v(22.31, 8.22) * mm});
            skLineSegment(sketch, "E1780", {"start": v(22.31, 8.22) * mm, "end": v(22.46, 8.18) * mm});
            skLineSegment(sketch, "E1781", {"start": v(22.46, 8.18) * mm, "end": v(22.6, 8.13) * mm});
            skLineSegment(sketch, "E1782", {"start": v(22.6, 8.13) * mm, "end": v(22.75, 8.08) * mm});
            skLineSegment(sketch, "E1783", {"start": v(22.75, 8.08) * mm, "end": v(22.88, 8.02) * mm});
            skLineSegment(sketch, "E1784", {"start": v(22.88, 8.02) * mm, "end": v(23.02, 7.95) * mm});
            skLineSegment(sketch, "E1785", {"start": v(23.02, 7.95) * mm, "end": v(23.14, 7.87) * mm});
            skLineSegment(sketch, "E1786", {"start": v(23.14, 7.87) * mm, "end": v(23.26, 7.79) * mm});
            skLineSegment(sketch, "E1787", {"start": v(23.26, 7.79) * mm, "end": v(23.38, 7.7) * mm});
            skLineSegment(sketch, "E1788", {"start": v(23.38, 7.7) * mm, "end": v(23.49, 7.6) * mm});
            skLineSegment(sketch, "E1789", {"start": v(23.49, 7.6) * mm, "end": v(23.6, 7.5) * mm});
            skLineSegment(sketch, "E1790", {"start": v(23.6, 7.5) * mm, "end": v(23.7, 7.4) * mm});
            skLineSegment(sketch, "E1791", {"start": v(23.7, 7.4) * mm, "end": v(23.8, 7.29) * mm});
            skLineSegment(sketch, "E1792", {"start": v(23.8, 7.29) * mm, "end": v(23.88, 7.17) * mm});
            skLineSegment(sketch, "E1793", {"start": v(23.88, 7.17) * mm, "end": v(23.97, 7.05) * mm});
            skLineSegment(sketch, "E1794", {"start": v(23.97, 7.05) * mm, "end": v(24.04, 6.92) * mm});
            skLineSegment(sketch, "E1795", {"start": v(24.04, 6.92) * mm, "end": v(24.12, 6.8) * mm});
            skLineSegment(sketch, "E1796", {"start": v(24.12, 6.8) * mm, "end": v(24.19, 6.66) * mm});
            skLineSegment(sketch, "E1797", {"start": v(24.19, 6.66) * mm, "end": v(24.25, 6.52) * mm});
            skLineSegment(sketch, "E1798", {"start": v(24.25, 6.52) * mm, "end": v(24.3, 6.38) * mm});
            skLineSegment(sketch, "E1799", {"start": v(24.3, 6.38) * mm, "end": v(24.35, 6.23) * mm});
            skLineSegment(sketch, "E1800", {"start": v(24.35, 6.23) * mm, "end": v(24.4, 6.07) * mm});
            skLineSegment(sketch, "E1801", {"start": v(24.4, 6.07) * mm, "end": v(24.44, 5.92) * mm});
            skLineSegment(sketch, "E1802", {"start": v(24.44, 5.92) * mm, "end": v(24.47, 5.76) * mm});
            skLineSegment(sketch, "E1803", {"start": v(24.47, 5.76) * mm, "end": v(24.5, 5.6) * mm});
            skLineSegment(sketch, "E1804", {"start": v(24.5, 5.6) * mm, "end": v(24.52, 5.45) * mm});
            skLineSegment(sketch, "E1805", {"start": v(24.52, 5.45) * mm, "end": v(24.53, 5.29) * mm});
            skLineSegment(sketch, "E1806", {"start": v(24.53, 5.29) * mm, "end": v(24.54, 5.13) * mm});
            skLineSegment(sketch, "E1807", {"start": v(24.54, 5.13) * mm, "end": v(24.54, 4.97) * mm});
            skLineSegment(sketch, "E1808", {"start": v(24.54, 4.97) * mm, "end": v(24.54, 4.8) * mm});
            skLineSegment(sketch, "E1809", {"start": v(24.54, 4.8) * mm, "end": v(24.53, 4.65) * mm});
            skLineSegment(sketch, "E1810", {"start": v(24.53, 4.65) * mm, "end": v(24.52, 4.5) * mm});
            skLineSegment(sketch, "E1811", {"start": v(24.52, 4.5) * mm, "end": v(24.5, 4.34) * mm});
            skLineSegment(sketch, "E1812", {"start": v(24.5, 4.34) * mm, "end": v(24.47, 4.18) * mm});
            skLineSegment(sketch, "E1813", {"start": v(24.47, 4.18) * mm, "end": v(24.44, 4.03) * mm});
            skLineSegment(sketch, "E1814", {"start": v(24.44, 4.03) * mm, "end": v(24.4, 3.87) * mm});
            skLineSegment(sketch, "E1815", {"start": v(24.4, 3.87) * mm, "end": v(24.36, 3.72) * mm});
            skLineSegment(sketch, "E1816", {"start": v(24.36, 3.72) * mm, "end": v(24.31, 3.57) * mm});
            skLineSegment(sketch, "E1817", {"start": v(24.31, 3.57) * mm, "end": v(24.26, 3.43) * mm});
            skLineSegment(sketch, "E1818", {"start": v(24.26, 3.43) * mm, "end": v(24.2, 3.29) * mm});
            skLineSegment(sketch, "E1819", {"start": v(24.2, 3.29) * mm, "end": v(24.13, 3.15) * mm});
            skLineSegment(sketch, "E1820", {"start": v(24.13, 3.15) * mm, "end": v(24.06, 3.02) * mm});
            skLineSegment(sketch, "E1821", {"start": v(24.06, 3.02) * mm, "end": v(23.99, 2.89) * mm});
            skLineSegment(sketch, "E1822", {"start": v(23.99, 2.89) * mm, "end": v(23.9, 2.76) * mm});
            skLineSegment(sketch, "E1823", {"start": v(23.9, 2.76) * mm, "end": v(23.82, 2.64) * mm});
            skLineSegment(sketch, "E1824", {"start": v(23.82, 2.64) * mm, "end": v(23.73, 2.52) * mm});
            skLineSegment(sketch, "E1825", {"start": v(23.73, 2.52) * mm, "end": v(23.63, 2.42) * mm});
            skLineSegment(sketch, "E1826", {"start": v(23.63, 2.42) * mm, "end": v(23.53, 2.31) * mm});
            skLineSegment(sketch, "E1827", {"start": v(23.53, 2.31) * mm, "end": v(23.42, 2.21) * mm});
            skLineSegment(sketch, "E1828", {"start": v(23.42, 2.21) * mm, "end": v(23.3, 2.12) * mm});
            skLineSegment(sketch, "E1829", {"start": v(23.3, 2.12) * mm, "end": v(23.18, 2.03) * mm});
            skLineSegment(sketch, "E1830", {"start": v(23.18, 2.03) * mm, "end": v(23.05, 1.95) * mm});
            skLineSegment(sketch, "E1831", {"start": v(23.05, 1.95) * mm, "end": v(22.92, 1.87) * mm});
            skLineSegment(sketch, "E1832", {"start": v(22.92, 1.87) * mm, "end": v(22.78, 1.8) * mm});
            skLineSegment(sketch, "E1833", {"start": v(22.78, 1.8) * mm, "end": v(22.64, 1.75) * mm});
            skLineSegment(sketch, "E1834", {"start": v(22.64, 1.75) * mm, "end": v(22.5, 1.7) * mm});
            skLineSegment(sketch, "E1835", {"start": v(22.5, 1.7) * mm, "end": v(22.34, 1.66) * mm});
            skLineSegment(sketch, "E1836", {"start": v(22.34, 1.66) * mm, "end": v(22.17, 1.62) * mm});
            skLineSegment(sketch, "E1837", {"start": v(22.17, 1.62) * mm, "end": v(22, 1.6) * mm});
            skLineSegment(sketch, "E1838", {"start": v(22, 1.6) * mm, "end": v(21.83, 1.59) * mm});
            skLineSegment(sketch, "E1839", {"start": v(21.83, 1.59) * mm, "end": v(21.65, 1.58) * mm});
            skLineSegment(sketch, "E1840", {"start": v(21.65, 1.58) * mm, "end": v(21.48, 1.59) * mm});
            skLineSegment(sketch, "E1841", {"start": v(21.48, 1.59) * mm, "end": v(21.32, 1.6) * mm});
            skLineSegment(sketch, "E1842", {"start": v(21.32, 1.6) * mm, "end": v(21.15, 1.62) * mm});
            skLineSegment(sketch, "E1843", {"start": v(21.15, 1.62) * mm, "end": v(21, 1.65) * mm});
            skLineSegment(sketch, "E1844", {"start": v(21, 1.65) * mm, "end": v(20.84, 1.7) * mm});
            skLineSegment(sketch, "E1845", {"start": v(20.84, 1.7) * mm, "end": v(20.7, 1.74) * mm});
            skLineSegment(sketch, "E1846", {"start": v(20.7, 1.74) * mm, "end": v(20.55, 1.8) * mm});
            skLineSegment(sketch, "E1847", {"start": v(20.55, 1.8) * mm, "end": v(20.42, 1.86) * mm});
            skLineSegment(sketch, "E1848", {"start": v(20.42, 1.86) * mm, "end": v(20.29, 1.93) * mm});
            skLineSegment(sketch, "E1849", {"start": v(20.29, 1.93) * mm, "end": v(20.16, 2) * mm});
            skLineSegment(sketch, "E1850", {"start": v(20.16, 2) * mm, "end": v(20.04, 2.1) * mm});
            skLineSegment(sketch, "E1851", {"start": v(20.04, 2.1) * mm, "end": v(19.92, 2.18) * mm});
            skLineSegment(sketch, "E1852", {"start": v(19.92, 2.18) * mm, "end": v(19.81, 2.28) * mm});
            skLineSegment(sketch, "E1853", {"start": v(19.81, 2.28) * mm, "end": v(19.7, 2.38) * mm});
            skLineSegment(sketch, "E1854", {"start": v(19.7, 2.38) * mm, "end": v(19.6, 2.49) * mm});
            skLineSegment(sketch, "E1855", {"start": v(19.6, 2.49) * mm, "end": v(19.51, 2.6) * mm});
            skLineSegment(sketch, "E1856", {"start": v(19.51, 2.6) * mm, "end": v(19.42, 2.72) * mm});
            skLineSegment(sketch, "E1857", {"start": v(19.42, 2.72) * mm, "end": v(19.34, 2.84) * mm});
            skLineSegment(sketch, "E1858", {"start": v(19.34, 2.84) * mm, "end": v(19.26, 2.97) * mm});
            skLineSegment(sketch, "E1859", {"start": v(19.26, 2.97) * mm, "end": v(19.2, 3.1) * mm});
            skLineSegment(sketch, "E1860", {"start": v(19.2, 3.1) * mm, "end": v(19.12, 3.24) * mm});
            skLineSegment(sketch, "E1861", {"start": v(19.12, 3.24) * mm, "end": v(19.06, 3.38) * mm});
            skLineSegment(sketch, "E1862", {"start": v(19.06, 3.38) * mm, "end": v(19, 3.53) * mm});
            skLineSegment(sketch, "E1863", {"start": v(19, 3.53) * mm, "end": v(18.96, 3.67) * mm});
            skLineSegment(sketch, "E1864", {"start": v(-1.4, 8.2) * mm, "end": v(-1.15, 8.2) * mm});
            skLineSegment(sketch, "E1865", {"start": v(-1.15, 8.2) * mm, "end": v(-0.91, 8.2) * mm});
            skLineSegment(sketch, "E1866", {"start": v(-0.91, 8.2) * mm, "end": v(-0.67, 8.2) * mm});
            skLineSegment(sketch, "E1867", {"start": v(-0.67, 8.2) * mm, "end": v(-0.43, 8.2) * mm});
            skLineSegment(sketch, "E1868", {"start": v(-0.43, 8.2) * mm, "end": v(-0.2, 8.2) * mm});
            skLineSegment(sketch, "E1869", {"start": v(-0.2, 8.2) * mm, "end": v(0.04, 8.2) * mm});
            skLineSegment(sketch, "E1870", {"start": v(0.04, 8.2) * mm, "end": v(0.28, 8.2) * mm});
            skLineSegment(sketch, "E1871", {"start": v(0.28, 8.2) * mm, "end": v(0.52, 8.2) * mm});
            skLineSegment(sketch, "E1872", {"start": v(0.52, 8.2) * mm, "end": v(0.57, 8.2) * mm});
            skLineSegment(sketch, "E1873", {"start": v(0.57, 8.2) * mm, "end": v(0.62, 8.2) * mm});
            skLineSegment(sketch, "E1874", {"start": v(0.62, 8.2) * mm, "end": v(0.67, 8.2) * mm});
            skLineSegment(sketch, "E1875", {"start": v(0.67, 8.2) * mm, "end": v(0.72, 8.2) * mm});
            skLineSegment(sketch, "E1876", {"start": v(0.72, 8.2) * mm, "end": v(0.77, 8.19) * mm});
            skLineSegment(sketch, "E1877", {"start": v(0.77, 8.19) * mm, "end": v(0.81, 8.18) * mm});
            skLineSegment(sketch, "E1878", {"start": v(0.81, 8.18) * mm, "end": v(0.86, 8.16) * mm});
            skLineSegment(sketch, "E1879", {"start": v(0.86, 8.16) * mm, "end": v(0.91, 8.15) * mm});
            skLineSegment(sketch, "E1880", {"start": v(0.91, 8.15) * mm, "end": v(0.96, 8.13) * mm});
            skLineSegment(sketch, "E1881", {"start": v(0.96, 8.13) * mm, "end": v(1, 8.1) * mm});
            skLineSegment(sketch, "E1882", {"start": v(1, 8.1) * mm, "end": v(1.05, 8.08) * mm});
            skLineSegment(sketch, "E1883", {"start": v(1.05, 8.08) * mm, "end": v(1.1, 8.06) * mm});
            skLineSegment(sketch, "E1884", {"start": v(1.1, 8.06) * mm, "end": v(1.14, 8.03) * mm});
            skLineSegment(sketch, "E1885", {"start": v(1.14, 8.03) * mm, "end": v(1.18, 8) * mm});
            skLineSegment(sketch, "E1886", {"start": v(1.18, 8) * mm, "end": v(1.22, 7.96) * mm});
            skLineSegment(sketch, "E1887", {"start": v(1.22, 7.96) * mm, "end": v(1.26, 7.92) * mm});
            skLineSegment(sketch, "E1888", {"start": v(1.26, 7.92) * mm, "end": v(1.3, 7.88) * mm});
            skLineSegment(sketch, "E1889", {"start": v(1.3, 7.88) * mm, "end": v(1.33, 7.83) * mm});
            skLineSegment(sketch, "E1890", {"start": v(1.33, 7.83) * mm, "end": v(1.36, 7.78) * mm});
            skLineSegment(sketch, "E1891", {"start": v(1.36, 7.78) * mm, "end": v(1.4, 7.73) * mm});
            skLineSegment(sketch, "E1892", {"start": v(1.4, 7.73) * mm, "end": v(1.43, 7.68) * mm});
            skLineSegment(sketch, "E1893", {"start": v(1.43, 7.68) * mm, "end": v(1.45, 7.62) * mm});
            skLineSegment(sketch, "E1894", {"start": v(1.45, 7.62) * mm, "end": v(1.48, 7.56) * mm});
            skLineSegment(sketch, "E1895", {"start": v(1.48, 7.56) * mm, "end": v(1.5, 7.5) * mm});
            skLineSegment(sketch, "E1896", {"start": v(1.5, 7.5) * mm, "end": v(1.53, 7.43) * mm});
            skLineSegment(sketch, "E1897", {"start": v(1.53, 7.43) * mm, "end": v(1.55, 7.36) * mm});
            skLineSegment(sketch, "E1898", {"start": v(1.55, 7.36) * mm, "end": v(1.56, 7.28) * mm});
            skLineSegment(sketch, "E1899", {"start": v(1.56, 7.28) * mm, "end": v(1.58, 7.2) * mm});
            skLineSegment(sketch, "E1900", {"start": v(1.58, 7.2) * mm, "end": v(1.59, 7.12) * mm});
            skLineSegment(sketch, "E1901", {"start": v(1.59, 7.12) * mm, "end": v(1.6, 7.04) * mm});
            skLineSegment(sketch, "E1902", {"start": v(1.6, 7.04) * mm, "end": v(1.6, 6.95) * mm});
            skLineSegment(sketch, "E1903", {"start": v(1.6, 6.95) * mm, "end": v(1.6, 6.85) * mm});
            skLineSegment(sketch, "E1904", {"start": v(1.6, 6.85) * mm, "end": v(1.6, 6.68) * mm});
            skLineSegment(sketch, "E1905", {"start": v(1.6, 6.68) * mm, "end": v(1.58, 6.52) * mm});
            skLineSegment(sketch, "E1906", {"start": v(1.58, 6.52) * mm, "end": v(1.56, 6.37) * mm});
            skLineSegment(sketch, "E1907", {"start": v(1.56, 6.37) * mm, "end": v(1.53, 6.23) * mm});
            skLineSegment(sketch, "E1908", {"start": v(1.53, 6.23) * mm, "end": v(1.48, 6.1) * mm});
            skLineSegment(sketch, "E1909", {"start": v(1.48, 6.1) * mm, "end": v(1.43, 5.98) * mm});
            skLineSegment(sketch, "E1910", {"start": v(1.43, 5.98) * mm, "end": v(1.37, 5.87) * mm});
            skLineSegment(sketch, "E1911", {"start": v(1.37, 5.87) * mm, "end": v(1.3, 5.78) * mm});
            skLineSegment(sketch, "E1912", {"start": v(1.3, 5.78) * mm, "end": v(1.23, 5.7) * mm});
            skLineSegment(sketch, "E1913", {"start": v(1.23, 5.7) * mm, "end": v(1.15, 5.63) * mm});
            skLineSegment(sketch, "E1914", {"start": v(1.15, 5.63) * mm, "end": v(1.07, 5.57) * mm});
            skLineSegment(sketch, "E1915", {"start": v(1.07, 5.57) * mm, "end": v(0.99, 5.53) * mm});
            skLineSegment(sketch, "E1916", {"start": v(0.99, 5.53) * mm, "end": v(0.9, 5.49) * mm});
            skLineSegment(sketch, "E1917", {"start": v(0.9, 5.49) * mm, "end": v(0.81, 5.46) * mm});
            skLineSegment(sketch, "E1918", {"start": v(0.81, 5.46) * mm, "end": v(0.72, 5.45) * mm});
            skLineSegment(sketch, "E1919", {"start": v(0.72, 5.45) * mm, "end": v(0.62, 5.44) * mm});
            skLineSegment(sketch, "E1920", {"start": v(0.62, 5.44) * mm, "end": v(0.37, 5.44) * mm});
            skLineSegment(sketch, "E1921", {"start": v(0.37, 5.44) * mm, "end": v(0.12, 5.44) * mm});
            skLineSegment(sketch, "E1922", {"start": v(0.12, 5.44) * mm, "end": v(-0.13, 5.44) * mm});
            skLineSegment(sketch, "E1923", {"start": v(-0.13, 5.44) * mm, "end": v(-0.39, 5.44) * mm});
            skLineSegment(sketch, "E1924", {"start": v(-0.39, 5.44) * mm, "end": v(-0.64, 5.44) * mm});
            skLineSegment(sketch, "E1925", {"start": v(-0.64, 5.44) * mm, "end": v(-0.89, 5.44) * mm});
            skLineSegment(sketch, "E1926", {"start": v(-0.89, 5.44) * mm, "end": v(-1.14, 5.44) * mm});
            skLineSegment(sketch, "E1927", {"start": v(-1.14, 5.44) * mm, "end": v(-1.4, 5.44) * mm});
            skLineSegment(sketch, "E1928", {"start": v(-1.4, 5.44) * mm, "end": v(-1.4, 5.79) * mm});
            skLineSegment(sketch, "E1929", {"start": v(-1.4, 5.79) * mm, "end": v(-1.4, 6.13) * mm});
            skLineSegment(sketch, "E1930", {"start": v(-1.4, 6.13) * mm, "end": v(-1.4, 6.48) * mm});
            skLineSegment(sketch, "E1931", {"start": v(-1.4, 6.48) * mm, "end": v(-1.4, 6.82) * mm});
            skLineSegment(sketch, "E1932", {"start": v(-1.4, 6.82) * mm, "end": v(-1.4, 7.16) * mm});
            skLineSegment(sketch, "E1933", {"start": v(-1.4, 7.16) * mm, "end": v(-1.4, 7.5) * mm});
            skLineSegment(sketch, "E1934", {"start": v(-1.4, 7.5) * mm, "end": v(-1.4, 7.85) * mm});
            skLineSegment(sketch, "E1935", {"start": v(-1.4, 7.85) * mm, "end": v(-1.4, 8.2) * mm});
            skLineSegment(sketch, "E1936", {"start": v(-14.11, 3.67) * mm, "end": v(-14.15, 3.83) * mm});
            skLineSegment(sketch, "E1937", {"start": v(-14.15, 3.83) * mm, "end": v(-14.2, 3.98) * mm});
            skLineSegment(sketch, "E1938", {"start": v(-14.2, 3.98) * mm, "end": v(-14.23, 4.14) * mm});
            skLineSegment(sketch, "E1939", {"start": v(-14.23, 4.14) * mm, "end": v(-14.25, 4.3) * mm});
            skLineSegment(sketch, "E1940", {"start": v(-14.25, 4.3) * mm, "end": v(-14.27, 4.45) * mm});
            skLineSegment(sketch, "E1941", {"start": v(-14.27, 4.45) * mm, "end": v(-14.29, 4.61) * mm});
            skLineSegment(sketch, "E1942", {"start": v(-14.29, 4.61) * mm, "end": v(-14.3, 4.77) * mm});
            skLineSegment(sketch, "E1943", {"start": v(-14.3, 4.77) * mm, "end": v(-14.3, 4.93) * mm});
            skLineSegment(sketch, "E1944", {"start": v(-14.3, 4.93) * mm, "end": v(-14.3, 5.1) * mm});
            skLineSegment(sketch, "E1945", {"start": v(-14.3, 5.1) * mm, "end": v(-14.29, 5.25) * mm});
            skLineSegment(sketch, "E1946", {"start": v(-14.29, 5.25) * mm, "end": v(-14.27, 5.4) * mm});
            skLineSegment(sketch, "E1947", {"start": v(-14.27, 5.4) * mm, "end": v(-14.25, 5.56) * mm});
            skLineSegment(sketch, "E1948", {"start": v(-14.25, 5.56) * mm, "end": v(-14.23, 5.72) * mm});
            skLineSegment(sketch, "E1949", {"start": v(-14.23, 5.72) * mm, "end": v(-14.2, 5.87) * mm});
            skLineSegment(sketch, "E1950", {"start": v(-14.2, 5.87) * mm, "end": v(-14.16, 6.03) * mm});
            skLineSegment(sketch, "E1951", {"start": v(-14.16, 6.03) * mm, "end": v(-14.12, 6.18) * mm});
            skLineSegment(sketch, "E1952", {"start": v(-14.12, 6.18) * mm, "end": v(-14.07, 6.33) * mm});
            skLineSegment(sketch, "E1953", {"start": v(-14.07, 6.33) * mm, "end": v(-14.02, 6.47) * mm});
            skLineSegment(sketch, "E1954", {"start": v(-14.02, 6.47) * mm, "end": v(-13.96, 6.61) * mm});
            skLineSegment(sketch, "E1955", {"start": v(-13.96, 6.61) * mm, "end": v(-13.9, 6.75) * mm});
            skLineSegment(sketch, "E1956", {"start": v(-13.9, 6.75) * mm, "end": v(-13.82, 6.88) * mm});
            skLineSegment(sketch, "E1957", {"start": v(-13.82, 6.88) * mm, "end": v(-13.74, 7) * mm});
            skLineSegment(sketch, "E1958", {"start": v(-13.74, 7) * mm, "end": v(-13.66, 7.13) * mm});
            skLineSegment(sketch, "E1959", {"start": v(-13.66, 7.13) * mm, "end": v(-13.57, 7.25) * mm});
            skLineSegment(sketch, "E1960", {"start": v(-13.57, 7.25) * mm, "end": v(-13.48, 7.36) * mm});
            skLineSegment(sketch, "E1961", {"start": v(-13.48, 7.36) * mm, "end": v(-13.38, 7.47) * mm});
            skLineSegment(sketch, "E1962", {"start": v(-13.38, 7.47) * mm, "end": v(-13.27, 7.57) * mm});
            skLineSegment(sketch, "E1963", {"start": v(-13.27, 7.57) * mm, "end": v(-13.16, 7.67) * mm});
            skLineSegment(sketch, "E1964", {"start": v(-13.16, 7.67) * mm, "end": v(-13.05, 7.76) * mm});
            skLineSegment(sketch, "E1965", {"start": v(-13.05, 7.76) * mm, "end": v(-12.93, 7.85) * mm});
            skLineSegment(sketch, "E1966", {"start": v(-12.93, 7.85) * mm, "end": v(-12.8, 7.93) * mm});
            skLineSegment(sketch, "E1967", {"start": v(-12.8, 7.93) * mm, "end": v(-12.67, 8) * mm});
            skLineSegment(sketch, "E1968", {"start": v(-12.67, 8) * mm, "end": v(-12.54, 8.07) * mm});
            skLineSegment(sketch, "E1969", {"start": v(-12.54, 8.07) * mm, "end": v(-12.4, 8.13) * mm});
            skLineSegment(sketch, "E1970", {"start": v(-12.4, 8.13) * mm, "end": v(-12.25, 8.18) * mm});
            skLineSegment(sketch, "E1971", {"start": v(-12.25, 8.18) * mm, "end": v(-12.1, 8.22) * mm});
            skLineSegment(sketch, "E1972", {"start": v(-12.1, 8.22) * mm, "end": v(-11.93, 8.25) * mm});
            skLineSegment(sketch, "E1973", {"start": v(-11.93, 8.25) * mm, "end": v(-11.76, 8.27) * mm});
            skLineSegment(sketch, "E1974", {"start": v(-11.76, 8.27) * mm, "end": v(-11.6, 8.28) * mm});
            skLineSegment(sketch, "E1975", {"start": v(-11.6, 8.28) * mm, "end": v(-11.41, 8.29) * mm});
            skLineSegment(sketch, "E1976", {"start": v(-11.41, 8.29) * mm, "end": v(-11.24, 8.28) * mm});
            skLineSegment(sketch, "E1977", {"start": v(-11.24, 8.28) * mm, "end": v(-11.07, 8.27) * mm});
            skLineSegment(sketch, "E1978", {"start": v(-11.07, 8.27) * mm, "end": v(-10.91, 8.25) * mm});
            skLineSegment(sketch, "E1979", {"start": v(-10.91, 8.25) * mm, "end": v(-10.76, 8.22) * mm});
            skLineSegment(sketch, "E1980", {"start": v(-10.76, 8.22) * mm, "end": v(-10.6, 8.18) * mm});
            skLineSegment(sketch, "E1981", {"start": v(-10.6, 8.18) * mm, "end": v(-10.46, 8.13) * mm});
            skLineSegment(sketch, "E1982", {"start": v(-10.46, 8.13) * mm, "end": v(-10.32, 8.08) * mm});
            skLineSegment(sketch, "E1983", {"start": v(-10.32, 8.08) * mm, "end": v(-10.18, 8.02) * mm});
            skLineSegment(sketch, "E1984", {"start": v(-10.18, 8.02) * mm, "end": v(-10.05, 7.95) * mm});
            skLineSegment(sketch, "E1985", {"start": v(-10.05, 7.95) * mm, "end": v(-9.93, 7.87) * mm});
            skLineSegment(sketch, "E1986", {"start": v(-9.93, 7.87) * mm, "end": v(-9.8, 7.79) * mm});
            skLineSegment(sketch, "E1987", {"start": v(-9.8, 7.79) * mm, "end": v(-9.69, 7.7) * mm});
            skLineSegment(sketch, "E1988", {"start": v(-9.69, 7.7) * mm, "end": v(-9.58, 7.6) * mm});
            skLineSegment(sketch, "E1989", {"start": v(-9.58, 7.6) * mm, "end": v(-9.47, 7.5) * mm});
            skLineSegment(sketch, "E1990", {"start": v(-9.47, 7.5) * mm, "end": v(-9.37, 7.4) * mm});
            skLineSegment(sketch, "E1991", {"start": v(-9.37, 7.4) * mm, "end": v(-9.28, 7.29) * mm});
            skLineSegment(sketch, "E1992", {"start": v(-9.28, 7.29) * mm, "end": v(-9.19, 7.17) * mm});
            skLineSegment(sketch, "E1993", {"start": v(-9.19, 7.17) * mm, "end": v(-9.1, 7.05) * mm});
            skLineSegment(sketch, "E1994", {"start": v(-9.1, 7.05) * mm, "end": v(-9.02, 6.92) * mm});
            skLineSegment(sketch, "E1995", {"start": v(-9.02, 6.92) * mm, "end": v(-8.95, 6.8) * mm});
            skLineSegment(sketch, "E1996", {"start": v(-8.95, 6.8) * mm, "end": v(-8.88, 6.66) * mm});
            skLineSegment(sketch, "E1997", {"start": v(-8.88, 6.66) * mm, "end": v(-8.82, 6.52) * mm});
            skLineSegment(sketch, "E1998", {"start": v(-8.82, 6.52) * mm, "end": v(-8.77, 6.38) * mm});
            skLineSegment(sketch, "E1999", {"start": v(-8.77, 6.38) * mm, "end": v(-8.72, 6.23) * mm});
            skLineSegment(sketch, "E2000", {"start": v(-8.72, 6.23) * mm, "end": v(-8.67, 6.07) * mm});
            skLineSegment(sketch, "E2001", {"start": v(-8.67, 6.07) * mm, "end": v(-8.63, 5.92) * mm});
            skLineSegment(sketch, "E2002", {"start": v(-8.63, 5.92) * mm, "end": v(-8.6, 5.76) * mm});
            skLineSegment(sketch, "E2003", {"start": v(-8.6, 5.76) * mm, "end": v(-8.57, 5.6) * mm});
            skLineSegment(sketch, "E2004", {"start": v(-8.57, 5.6) * mm, "end": v(-8.55, 5.45) * mm});
            skLineSegment(sketch, "E2005", {"start": v(-8.55, 5.45) * mm, "end": v(-8.54, 5.29) * mm});
            skLineSegment(sketch, "E2006", {"start": v(-8.54, 5.29) * mm, "end": v(-8.53, 5.13) * mm});
            skLineSegment(sketch, "E2007", {"start": v(-8.53, 5.13) * mm, "end": v(-8.52, 4.97) * mm});
            skLineSegment(sketch, "E2008", {"start": v(-8.52, 4.97) * mm, "end": v(-8.53, 4.8) * mm});
            skLineSegment(sketch, "E2009", {"start": v(-8.53, 4.8) * mm, "end": v(-8.54, 4.65) * mm});
            skLineSegment(sketch, "E2010", {"start": v(-8.54, 4.65) * mm, "end": v(-8.55, 4.5) * mm});
            skLineSegment(sketch, "E2011", {"start": v(-8.55, 4.5) * mm, "end": v(-8.57, 4.34) * mm});
            skLineSegment(sketch, "E2012", {"start": v(-8.57, 4.34) * mm, "end": v(-8.6, 4.18) * mm});
            skLineSegment(sketch, "E2013", {"start": v(-8.6, 4.18) * mm, "end": v(-8.63, 4.03) * mm});
            skLineSegment(sketch, "E2014", {"start": v(-8.63, 4.03) * mm, "end": v(-8.66, 3.87) * mm});
            skLineSegment(sketch, "E2015", {"start": v(-8.66, 3.87) * mm, "end": v(-8.7, 3.72) * mm});
            skLineSegment(sketch, "E2016", {"start": v(-8.7, 3.72) * mm, "end": v(-8.76, 3.57) * mm});
            skLineSegment(sketch, "E2017", {"start": v(-8.76, 3.57) * mm, "end": v(-8.8, 3.43) * mm});
            skLineSegment(sketch, "E2018", {"start": v(-8.8, 3.43) * mm, "end": v(-8.87, 3.29) * mm});
            skLineSegment(sketch, "E2019", {"start": v(-8.87, 3.29) * mm, "end": v(-8.93, 3.15) * mm});
            skLineSegment(sketch, "E2020", {"start": v(-8.93, 3.15) * mm, "end": v(-9, 3.02) * mm});
            skLineSegment(sketch, "E2021", {"start": v(-9, 3.02) * mm, "end": v(-9.08, 2.89) * mm});
            skLineSegment(sketch, "E2022", {"start": v(-9.08, 2.89) * mm, "end": v(-9.16, 2.76) * mm});
            skLineSegment(sketch, "E2023", {"start": v(-9.16, 2.76) * mm, "end": v(-9.25, 2.64) * mm});
            skLineSegment(sketch, "E2024", {"start": v(-9.25, 2.64) * mm, "end": v(-9.34, 2.52) * mm});
            skLineSegment(sketch, "E2025", {"start": v(-9.34, 2.52) * mm, "end": v(-9.44, 2.42) * mm});
            skLineSegment(sketch, "E2026", {"start": v(-9.44, 2.42) * mm, "end": v(-9.54, 2.31) * mm});
            skLineSegment(sketch, "E2027", {"start": v(-9.54, 2.31) * mm, "end": v(-9.65, 2.21) * mm});
            skLineSegment(sketch, "E2028", {"start": v(-9.65, 2.21) * mm, "end": v(-9.77, 2.12) * mm});
            skLineSegment(sketch, "E2029", {"start": v(-9.77, 2.12) * mm, "end": v(-9.89, 2.03) * mm});
            skLineSegment(sketch, "E2030", {"start": v(-9.89, 2.03) * mm, "end": v(-10.01, 1.95) * mm});
            skLineSegment(sketch, "E2031", {"start": v(-10.01, 1.95) * mm, "end": v(-10.15, 1.87) * mm});
            skLineSegment(sketch, "E2032", {"start": v(-10.15, 1.87) * mm, "end": v(-10.28, 1.8) * mm});
            skLineSegment(sketch, "E2033", {"start": v(-10.28, 1.8) * mm, "end": v(-10.43, 1.75) * mm});
            skLineSegment(sketch, "E2034", {"start": v(-10.43, 1.75) * mm, "end": v(-10.58, 1.7) * mm});
            skLineSegment(sketch, "E2035", {"start": v(-10.58, 1.7) * mm, "end": v(-10.73, 1.66) * mm});
            skLineSegment(sketch, "E2036", {"start": v(-10.73, 1.66) * mm, "end": v(-10.9, 1.62) * mm});
            skLineSegment(sketch, "E2037", {"start": v(-10.9, 1.62) * mm, "end": v(-11.06, 1.6) * mm});
            skLineSegment(sketch, "E2038", {"start": v(-11.06, 1.6) * mm, "end": v(-11.23, 1.59) * mm});
            skLineSegment(sketch, "E2039", {"start": v(-11.23, 1.59) * mm, "end": v(-11.41, 1.58) * mm});
            skLineSegment(sketch, "E2040", {"start": v(-11.41, 1.58) * mm, "end": v(-11.58, 1.59) * mm});
            skLineSegment(sketch, "E2041", {"start": v(-11.58, 1.59) * mm, "end": v(-11.75, 1.6) * mm});
            skLineSegment(sketch, "E2042", {"start": v(-11.75, 1.6) * mm, "end": v(-11.91, 1.62) * mm});
            skLineSegment(sketch, "E2043", {"start": v(-11.91, 1.62) * mm, "end": v(-12.07, 1.65) * mm});
            skLineSegment(sketch, "E2044", {"start": v(-12.07, 1.65) * mm, "end": v(-12.22, 1.7) * mm});
            skLineSegment(sketch, "E2045", {"start": v(-12.22, 1.7) * mm, "end": v(-12.37, 1.74) * mm});
            skLineSegment(sketch, "E2046", {"start": v(-12.37, 1.74) * mm, "end": v(-12.51, 1.8) * mm});
            skLineSegment(sketch, "E2047", {"start": v(-12.51, 1.8) * mm, "end": v(-12.65, 1.86) * mm});
            skLineSegment(sketch, "E2048", {"start": v(-12.65, 1.86) * mm, "end": v(-12.78, 1.93) * mm});
            skLineSegment(sketch, "E2049", {"start": v(-12.78, 1.93) * mm, "end": v(-12.9, 2) * mm});
            skLineSegment(sketch, "E2050", {"start": v(-12.9, 2) * mm, "end": v(-13.03, 2.1) * mm});
            skLineSegment(sketch, "E2051", {"start": v(-13.03, 2.1) * mm, "end": v(-13.15, 2.18) * mm});
            skLineSegment(sketch, "E2052", {"start": v(-13.15, 2.18) * mm, "end": v(-13.26, 2.28) * mm});
            skLineSegment(sketch, "E2053", {"start": v(-13.26, 2.28) * mm, "end": v(-13.36, 2.38) * mm});
            skLineSegment(sketch, "E2054", {"start": v(-13.36, 2.38) * mm, "end": v(-13.46, 2.49) * mm});
            skLineSegment(sketch, "E2055", {"start": v(-13.46, 2.49) * mm, "end": v(-13.55, 2.6) * mm});
            skLineSegment(sketch, "E2056", {"start": v(-13.55, 2.6) * mm, "end": v(-13.64, 2.72) * mm});
            skLineSegment(sketch, "E2057", {"start": v(-13.64, 2.72) * mm, "end": v(-13.73, 2.84) * mm});
            skLineSegment(sketch, "E2058", {"start": v(-13.73, 2.84) * mm, "end": v(-13.8, 2.97) * mm});
            skLineSegment(sketch, "E2059", {"start": v(-13.8, 2.97) * mm, "end": v(-13.88, 3.1) * mm});
            skLineSegment(sketch, "E2060", {"start": v(-13.88, 3.1) * mm, "end": v(-13.94, 3.24) * mm});
            skLineSegment(sketch, "E2061", {"start": v(-13.94, 3.24) * mm, "end": v(-14, 3.38) * mm});
            skLineSegment(sketch, "E2062", {"start": v(-14, 3.38) * mm, "end": v(-14.06, 3.53) * mm});
            skLineSegment(sketch, "E2063", {"start": v(-14.06, 3.53) * mm, "end": v(-14.11, 3.67) * mm});
            skLineSegment(sketch, "E2064", {"start": v(-46.69, 8.3) * mm, "end": v(-46.36, 8.3) * mm});
            skLineSegment(sketch, "E2065", {"start": v(-46.36, 8.3) * mm, "end": v(-46.04, 8.3) * mm});
            skLineSegment(sketch, "E2066", {"start": v(-46.04, 8.3) * mm, "end": v(-45.72, 8.3) * mm});
            skLineSegment(sketch, "E2067", {"start": v(-45.72, 8.3) * mm, "end": v(-45.4, 8.3) * mm});
            skLineSegment(sketch, "E2068", {"start": v(-45.4, 8.3) * mm, "end": v(-45.07, 8.3) * mm});
            skLineSegment(sketch, "E2069", {"start": v(-45.07, 8.3) * mm, "end": v(-44.74, 8.3) * mm});
            skLineSegment(sketch, "E2070", {"start": v(-44.74, 8.3) * mm, "end": v(-44.42, 8.3) * mm});
            skLineSegment(sketch, "E2071", {"start": v(-44.42, 8.3) * mm, "end": v(-44.1, 8.3) * mm});
            skLineSegment(sketch, "E2072", {"start": v(-44.1, 8.3) * mm, "end": v(-44, 8.3) * mm});
            skLineSegment(sketch, "E2073", {"start": v(-44, 8.3) * mm, "end": v(-43.93, 8.29) * mm});
            skLineSegment(sketch, "E2074", {"start": v(-43.93, 8.29) * mm, "end": v(-43.85, 8.27) * mm});
            skLineSegment(sketch, "E2075", {"start": v(-43.85, 8.27) * mm, "end": v(-43.77, 8.24) * mm});
            skLineSegment(sketch, "E2076", {"start": v(-43.77, 8.24) * mm, "end": v(-43.7, 8.2) * mm});
            skLineSegment(sketch, "E2077", {"start": v(-43.7, 8.2) * mm, "end": v(-43.63, 8.17) * mm});
            skLineSegment(sketch, "E2078", {"start": v(-43.63, 8.17) * mm, "end": v(-43.56, 8.12) * mm});
            skLineSegment(sketch, "E2079", {"start": v(-43.56, 8.12) * mm, "end": v(-43.5, 8.06) * mm});
            skLineSegment(sketch, "E2080", {"start": v(-43.5, 8.06) * mm, "end": v(-43.44, 7.99) * mm});
            skLineSegment(sketch, "E2081", {"start": v(-43.44, 7.99) * mm, "end": v(-43.39, 7.91) * mm});
            skLineSegment(sketch, "E2082", {"start": v(-43.39, 7.91) * mm, "end": v(-43.34, 7.83) * mm});
            skLineSegment(sketch, "E2083", {"start": v(-43.34, 7.83) * mm, "end": v(-43.3, 7.74) * mm});
            skLineSegment(sketch, "E2084", {"start": v(-43.3, 7.74) * mm, "end": v(-43.28, 7.64) * mm});
            skLineSegment(sketch, "E2085", {"start": v(-43.28, 7.64) * mm, "end": v(-43.26, 7.53) * mm});
            skLineSegment(sketch, "E2086", {"start": v(-43.26, 7.53) * mm, "end": v(-43.25, 7.42) * mm});
            skLineSegment(sketch, "E2087", {"start": v(-43.25, 7.42) * mm, "end": v(-43.25, 7.3) * mm});
            skLineSegment(sketch, "E2088", {"start": v(-43.25, 7.3) * mm, "end": v(-43.25, 7.16) * mm});
            skLineSegment(sketch, "E2089", {"start": v(-43.25, 7.16) * mm, "end": v(-43.26, 7.04) * mm});
            skLineSegment(sketch, "E2090", {"start": v(-43.26, 7.04) * mm, "end": v(-43.29, 6.93) * mm});
            skLineSegment(sketch, "E2091", {"start": v(-43.29, 6.93) * mm, "end": v(-43.32, 6.83) * mm});
            skLineSegment(sketch, "E2092", {"start": v(-43.32, 6.83) * mm, "end": v(-43.36, 6.74) * mm});
            skLineSegment(sketch, "E2093", {"start": v(-43.36, 6.74) * mm, "end": v(-43.4, 6.65) * mm});
            skLineSegment(sketch, "E2094", {"start": v(-43.4, 6.65) * mm, "end": v(-43.46, 6.58) * mm});
            skLineSegment(sketch, "E2095", {"start": v(-43.46, 6.58) * mm, "end": v(-43.53, 6.51) * mm});
            skLineSegment(sketch, "E2096", {"start": v(-43.53, 6.51) * mm, "end": v(-43.6, 6.45) * mm});
            skLineSegment(sketch, "E2097", {"start": v(-43.6, 6.45) * mm, "end": v(-43.68, 6.4) * mm});
            skLineSegment(sketch, "E2098", {"start": v(-43.68, 6.4) * mm, "end": v(-43.76, 6.36) * mm});
            skLineSegment(sketch, "E2099", {"start": v(-43.76, 6.36) * mm, "end": v(-43.84, 6.32) * mm});
            skLineSegment(sketch, "E2100", {"start": v(-43.84, 6.32) * mm, "end": v(-43.92, 6.3) * mm});
            skLineSegment(sketch, "E2101", {"start": v(-43.92, 6.3) * mm, "end": v(-44.01, 6.27) * mm});
            skLineSegment(sketch, "E2102", {"start": v(-44.01, 6.27) * mm, "end": v(-44.1, 6.26) * mm});
            skLineSegment(sketch, "E2103", {"start": v(-44.1, 6.26) * mm, "end": v(-44.2, 6.26) * mm});
            skLineSegment(sketch, "E2104", {"start": v(-44.2, 6.26) * mm, "end": v(-44.5, 6.26) * mm});
            skLineSegment(sketch, "E2105", {"start": v(-44.5, 6.26) * mm, "end": v(-44.82, 6.26) * mm});
            skLineSegment(sketch, "E2106", {"start": v(-44.82, 6.26) * mm, "end": v(-45.13, 6.26) * mm});
            skLineSegment(sketch, "E2107", {"start": v(-45.13, 6.26) * mm, "end": v(-45.44, 6.26) * mm});
            skLineSegment(sketch, "E2108", {"start": v(-45.44, 6.26) * mm, "end": v(-45.75, 6.26) * mm});
            skLineSegment(sketch, "E2109", {"start": v(-45.75, 6.26) * mm, "end": v(-46.06, 6.26) * mm});
            skLineSegment(sketch, "E2110", {"start": v(-46.06, 6.26) * mm, "end": v(-46.38, 6.26) * mm});
            skLineSegment(sketch, "E2111", {"start": v(-46.38, 6.26) * mm, "end": v(-46.69, 6.26) * mm});
            skLineSegment(sketch, "E2112", {"start": v(-46.69, 6.26) * mm, "end": v(-46.69, 6.51) * mm});
            skLineSegment(sketch, "E2113", {"start": v(-46.69, 6.51) * mm, "end": v(-46.69, 6.77) * mm});
            skLineSegment(sketch, "E2114", {"start": v(-46.69, 6.77) * mm, "end": v(-46.69, 7.02) * mm});
            skLineSegment(sketch, "E2115", {"start": v(-46.69, 7.02) * mm, "end": v(-46.69, 7.28) * mm});
            skLineSegment(sketch, "E2116", {"start": v(-46.69, 7.28) * mm, "end": v(-46.69, 7.53) * mm});
            skLineSegment(sketch, "E2117", {"start": v(-46.69, 7.53) * mm, "end": v(-46.69, 7.8) * mm});
            skLineSegment(sketch, "E2118", {"start": v(-46.69, 7.8) * mm, "end": v(-46.69, 8.05) * mm});
            skLineSegment(sketch, "E2119", {"start": v(-46.69, 8.05) * mm, "end": v(-46.69, 8.3) * mm});
            skLineSegment(sketch, "E2120", {"start": v(-46.69, 3.75) * mm, "end": v(-46.32, 3.75) * mm});
            skLineSegment(sketch, "E2121", {"start": v(-46.32, 3.75) * mm, "end": v(-45.95, 3.75) * mm});
            skLineSegment(sketch, "E2122", {"start": v(-45.95, 3.75) * mm, "end": v(-45.58, 3.75) * mm});
            skLineSegment(sketch, "E2123", {"start": v(-45.58, 3.75) * mm, "end": v(-45.2, 3.75) * mm});
            skLineSegment(sketch, "E2124", {"start": v(-45.2, 3.75) * mm, "end": v(-44.84, 3.75) * mm});
            skLineSegment(sketch, "E2125", {"start": v(-44.84, 3.75) * mm, "end": v(-44.47, 3.75) * mm});
            skLineSegment(sketch, "E2126", {"start": v(-44.47, 3.75) * mm, "end": v(-44.1, 3.75) * mm});
            skLineSegment(sketch, "E2127", {"start": v(-44.1, 3.75) * mm, "end": v(-43.73, 3.75) * mm});
            skLineSegment(sketch, "E2128", {"start": v(-43.73, 3.75) * mm, "end": v(-43.63, 3.75) * mm});
            skLineSegment(sketch, "E2129", {"start": v(-43.63, 3.75) * mm, "end": v(-43.54, 3.73) * mm});
            skLineSegment(sketch, "E2130", {"start": v(-43.54, 3.73) * mm, "end": v(-43.46, 3.7) * mm});
            skLineSegment(sketch, "E2131", {"start": v(-43.46, 3.7) * mm, "end": v(-43.37, 3.67) * mm});
            skLineSegment(sketch, "E2132", {"start": v(-43.37, 3.67) * mm, "end": v(-43.3, 3.63) * mm});
            skLineSegment(sketch, "E2133", {"start": v(-43.3, 3.63) * mm, "end": v(-43.22, 3.57) * mm});
            skLineSegment(sketch, "E2134", {"start": v(-43.22, 3.57) * mm, "end": v(-43.15, 3.5) * mm});
            skLineSegment(sketch, "E2135", {"start": v(-43.15, 3.5) * mm, "end": v(-43.09, 3.44) * mm});
            skLineSegment(sketch, "E2136", {"start": v(-43.09, 3.44) * mm, "end": v(-43.02, 3.35) * mm});
            skLineSegment(sketch, "E2137", {"start": v(-43.02, 3.35) * mm, "end": v(-42.97, 3.26) * mm});
            skLineSegment(sketch, "E2138", {"start": v(-42.97, 3.26) * mm, "end": v(-42.92, 3.17) * mm});
            skLineSegment(sketch, "E2139", {"start": v(-42.92, 3.17) * mm, "end": v(-42.88, 3.07) * mm});
            skLineSegment(sketch, "E2140", {"start": v(-42.88, 3.07) * mm, "end": v(-42.85, 2.97) * mm});
            skLineSegment(sketch, "E2141", {"start": v(-42.85, 2.97) * mm, "end": v(-42.83, 2.87) * mm});
            skLineSegment(sketch, "E2142", {"start": v(-42.83, 2.87) * mm, "end": v(-42.82, 2.75) * mm});
            skLineSegment(sketch, "E2143", {"start": v(-42.82, 2.75) * mm, "end": v(-42.82, 2.64) * mm});
            skLineSegment(sketch, "E2144", {"start": v(-42.82, 2.64) * mm, "end": v(-42.82, 2.52) * mm});
            skLineSegment(sketch, "E2145", {"start": v(-42.82, 2.52) * mm, "end": v(-42.83, 2.4) * mm});
            skLineSegment(sketch, "E2146", {"start": v(-42.83, 2.4) * mm, "end": v(-42.86, 2.3) * mm});
            skLineSegment(sketch, "E2147", {"start": v(-42.86, 2.3) * mm, "end": v(-42.89, 2.2) * mm});
            skLineSegment(sketch, "E2148", {"start": v(-42.89, 2.2) * mm, "end": v(-42.93, 2.1) * mm});
            skLineSegment(sketch, "E2149", {"start": v(-42.93, 2.1) * mm, "end": v(-42.98, 2.01) * mm});
            skLineSegment(sketch, "E2150", {"start": v(-42.98, 2.01) * mm, "end": v(-43.04, 1.93) * mm});
            skLineSegment(sketch, "E2151", {"start": v(-43.04, 1.93) * mm, "end": v(-43.1, 1.86) * mm});
            skLineSegment(sketch, "E2152", {"start": v(-43.1, 1.86) * mm, "end": v(-43.18, 1.79) * mm});
            skLineSegment(sketch, "E2153", {"start": v(-43.18, 1.79) * mm, "end": v(-43.26, 1.73) * mm});
            skLineSegment(sketch, "E2154", {"start": v(-43.26, 1.73) * mm, "end": v(-43.35, 1.68) * mm});
            skLineSegment(sketch, "E2155", {"start": v(-43.35, 1.68) * mm, "end": v(-43.44, 1.64) * mm});
            skLineSegment(sketch, "E2156", {"start": v(-43.44, 1.64) * mm, "end": v(-43.53, 1.6) * mm});
            skLineSegment(sketch, "E2157", {"start": v(-43.53, 1.6) * mm, "end": v(-43.63, 1.58) * mm});
            skLineSegment(sketch, "E2158", {"start": v(-43.63, 1.58) * mm, "end": v(-43.73, 1.57) * mm});
            skLineSegment(sketch, "E2159", {"start": v(-43.73, 1.57) * mm, "end": v(-43.85, 1.56) * mm});
            skLineSegment(sketch, "E2160", {"start": v(-43.85, 1.56) * mm, "end": v(-44.2, 1.56) * mm});
            skLineSegment(sketch, "E2161", {"start": v(-44.2, 1.56) * mm, "end": v(-44.56, 1.56) * mm});
            skLineSegment(sketch, "E2162", {"start": v(-44.56, 1.56) * mm, "end": v(-44.91, 1.56) * mm});
            skLineSegment(sketch, "E2163", {"start": v(-44.91, 1.56) * mm, "end": v(-45.27, 1.56) * mm});
            skLineSegment(sketch, "E2164", {"start": v(-45.27, 1.56) * mm, "end": v(-45.62, 1.56) * mm});
            skLineSegment(sketch, "E2165", {"start": v(-45.62, 1.56) * mm, "end": v(-45.98, 1.56) * mm});
            skLineSegment(sketch, "E2166", {"start": v(-45.98, 1.56) * mm, "end": v(-46.33, 1.56) * mm});
            skLineSegment(sketch, "E2167", {"start": v(-46.33, 1.56) * mm, "end": v(-46.69, 1.56) * mm});
            skLineSegment(sketch, "E2168", {"start": v(-46.69, 1.56) * mm, "end": v(-46.69, 1.84) * mm});
            skLineSegment(sketch, "E2169", {"start": v(-46.69, 1.84) * mm, "end": v(-46.69, 2.11) * mm});
            skLineSegment(sketch, "E2170", {"start": v(-46.69, 2.11) * mm, "end": v(-46.69, 2.38) * mm});
            skLineSegment(sketch, "E2171", {"start": v(-46.69, 2.38) * mm, "end": v(-46.69, 2.66) * mm});
            skLineSegment(sketch, "E2172", {"start": v(-46.69, 2.66) * mm, "end": v(-46.69, 2.93) * mm});
            skLineSegment(sketch, "E2173", {"start": v(-46.69, 2.93) * mm, "end": v(-46.69, 3.2) * mm});
            skLineSegment(sketch, "E2174", {"start": v(-46.69, 3.2) * mm, "end": v(-46.69, 3.48) * mm});
            skLineSegment(sketch, "E2175", {"start": v(-46.69, 3.48) * mm, "end": v(-46.69, 3.75) * mm});
            skLineSegment(sketch, "E2176", {"start": v(57.45, 5.24) * mm, "end": v(58.06, 4.48) * mm});
            skLineSegment(sketch, "E2177", {"start": v(58.06, 4.48) * mm, "end": v(58.68, 3.72) * mm});
            skLineSegment(sketch, "E2178", {"start": v(58.68, 3.72) * mm, "end": v(59.29, 2.96) * mm});
            skLineSegment(sketch, "E2179", {"start": v(59.29, 2.96) * mm, "end": v(59.9, 2.2) * mm});
            skLineSegment(sketch, "E2180", {"start": v(59.9, 2.2) * mm, "end": v(60.51, 1.44) * mm});
            skLineSegment(sketch, "E2181", {"start": v(60.51, 1.44) * mm, "end": v(61.12, 0.68) * mm});
            skLineSegment(sketch, "E2182", {"start": v(61.12, 0.68) * mm, "end": v(61.74, -0.08) * mm});
            skLineSegment(sketch, "E2183", {"start": v(61.74, -0.08) * mm, "end": v(62.35, -0.83) * mm});
            skLineSegment(sketch, "E2184", {"start": v(62.35, -0.83) * mm, "end": v(61.74, -0.83) * mm});
            skLineSegment(sketch, "E2185", {"start": v(61.74, -0.83) * mm, "end": v(61.12, -0.83) * mm});
            skLineSegment(sketch, "E2186", {"start": v(61.12, -0.83) * mm, "end": v(60.51, -0.83) * mm});
            skLineSegment(sketch, "E2187", {"start": v(60.51, -0.83) * mm, "end": v(59.9, -0.83) * mm});
            skLineSegment(sketch, "E2188", {"start": v(59.9, -0.83) * mm, "end": v(59.29, -0.83) * mm});
            skLineSegment(sketch, "E2189", {"start": v(59.29, -0.83) * mm, "end": v(58.68, -0.83) * mm});
            skLineSegment(sketch, "E2190", {"start": v(58.68, -0.83) * mm, "end": v(58.06, -0.83) * mm});
            skLineSegment(sketch, "E2191", {"start": v(58.06, -0.83) * mm, "end": v(57.45, -0.83) * mm});
            skLineSegment(sketch, "E2192", {"start": v(57.45, -0.83) * mm, "end": v(57.45, -0.08) * mm});
            skLineSegment(sketch, "E2193", {"start": v(57.45, -0.08) * mm, "end": v(57.45, 0.68) * mm});
            skLineSegment(sketch, "E2194", {"start": v(57.45, 0.68) * mm, "end": v(57.45, 1.44) * mm});
            skLineSegment(sketch, "E2195", {"start": v(57.45, 1.44) * mm, "end": v(57.45, 2.2) * mm});
            skLineSegment(sketch, "E2196", {"start": v(57.45, 2.2) * mm, "end": v(57.45, 2.96) * mm});
            skLineSegment(sketch, "E2197", {"start": v(57.45, 2.96) * mm, "end": v(57.45, 3.72) * mm});
            skLineSegment(sketch, "E2198", {"start": v(57.45, 3.72) * mm, "end": v(57.45, 4.48) * mm});
            skLineSegment(sketch, "E2199", {"start": v(57.45, 4.48) * mm, "end": v(57.45, 5.24) * mm});
            skLineSegment(sketch, "E2200", {"start": v(47.64, -0.2) * mm, "end": v(47.64, -0.28) * mm});
            skLineSegment(sketch, "E2201", {"start": v(47.64, -0.28) * mm, "end": v(47.64, -0.36) * mm});
            skLineSegment(sketch, "E2202", {"start": v(47.64, -0.36) * mm, "end": v(47.64, -0.44) * mm});
            skLineSegment(sketch, "E2203", {"start": v(47.64, -0.44) * mm, "end": v(47.64, -0.52) * mm});
            skLineSegment(sketch, "E2204", {"start": v(47.64, -0.52) * mm, "end": v(47.64, -0.6) * mm});
            skLineSegment(sketch, "E2205", {"start": v(47.64, -0.6) * mm, "end": v(47.64, -0.68) * mm});
            skLineSegment(sketch, "E2206", {"start": v(47.64, -0.68) * mm, "end": v(47.64, -0.76) * mm});
            skLineSegment(sketch, "E2207", {"start": v(47.64, -0.76) * mm, "end": v(47.64, -0.83) * mm});
            skLineSegment(sketch, "E2208", {"start": v(47.64, -0.83) * mm, "end": v(47.52, -0.83) * mm});
            skLineSegment(sketch, "E2209", {"start": v(47.52, -0.83) * mm, "end": v(47.4, -0.83) * mm});
            skLineSegment(sketch, "E2210", {"start": v(47.4, -0.83) * mm, "end": v(47.26, -0.83) * mm});
            skLineSegment(sketch, "E2211", {"start": v(47.26, -0.83) * mm, "end": v(47.14, -0.83) * mm});
            skLineSegment(sketch, "E2212", {"start": v(47.14, -0.83) * mm, "end": v(47.01, -0.83) * mm});
            skLineSegment(sketch, "E2213", {"start": v(47.01, -0.83) * mm, "end": v(46.88, -0.83) * mm});
            skLineSegment(sketch, "E2214", {"start": v(46.88, -0.83) * mm, "end": v(46.76, -0.83) * mm});
            skLineSegment(sketch, "E2215", {"start": v(46.76, -0.83) * mm, "end": v(46.63, -0.83) * mm});
            skLineSegment(sketch, "E2216", {"start": v(46.63, -0.83) * mm, "end": v(46.76, -0.77) * mm});
            skLineSegment(sketch, "E2217", {"start": v(46.76, -0.77) * mm, "end": v(46.88, -0.7) * mm});
            skLineSegment(sketch, "E2218", {"start": v(46.88, -0.7) * mm, "end": v(47, -0.62) * mm});
            skLineSegment(sketch, "E2219", {"start": v(47, -0.62) * mm, "end": v(47.13, -0.55) * mm});
            skLineSegment(sketch, "E2220", {"start": v(47.13, -0.55) * mm, "end": v(47.26, -0.47) * mm});
            skLineSegment(sketch, "E2221", {"start": v(47.26, -0.47) * mm, "end": v(47.39, -0.38) * mm});
            skLineSegment(sketch, "E2222", {"start": v(47.39, -0.38) * mm, "end": v(47.51, -0.3) * mm});
            skLineSegment(sketch, "E2223", {"start": v(47.51, -0.3) * mm, "end": v(47.64, -0.2) * mm});
            skLineSegment(sketch, "E2224", {"start": v(31.63, 8.2) * mm, "end": v(31.9, 8.2) * mm});
            skLineSegment(sketch, "E2225", {"start": v(31.9, 8.2) * mm, "end": v(32.18, 8.2) * mm});
            skLineSegment(sketch, "E2226", {"start": v(32.18, 8.2) * mm, "end": v(32.45, 8.2) * mm});
            skLineSegment(sketch, "E2227", {"start": v(32.45, 8.2) * mm, "end": v(32.73, 8.2) * mm});
            skLineSegment(sketch, "E2228", {"start": v(32.73, 8.2) * mm, "end": v(33, 8.2) * mm});
            skLineSegment(sketch, "E2229", {"start": v(33, 8.2) * mm, "end": v(33.28, 8.2) * mm});
            skLineSegment(sketch, "E2230", {"start": v(33.28, 8.2) * mm, "end": v(33.56, 8.2) * mm});
            skLineSegment(sketch, "E2231", {"start": v(33.56, 8.2) * mm, "end": v(33.83, 8.2) * mm});
            skLineSegment(sketch, "E2232", {"start": v(33.83, 8.2) * mm, "end": v(33.93, 8.2) * mm});
            skLineSegment(sketch, "E2233", {"start": v(33.93, 8.2) * mm, "end": v(34.02, 8.18) * mm});
            skLineSegment(sketch, "E2234", {"start": v(34.02, 8.18) * mm, "end": v(34.11, 8.15) * mm});
            skLineSegment(sketch, "E2235", {"start": v(34.11, 8.15) * mm, "end": v(34.2, 8.12) * mm});
            skLineSegment(sketch, "E2236", {"start": v(34.2, 8.12) * mm, "end": v(34.29, 8.07) * mm});
            skLineSegment(sketch, "E2237", {"start": v(34.29, 8.07) * mm, "end": v(34.38, 8.01) * mm});
            skLineSegment(sketch, "E2238", {"start": v(34.38, 8.01) * mm, "end": v(34.46, 7.94) * mm});
            skLineSegment(sketch, "E2239", {"start": v(34.46, 7.94) * mm, "end": v(34.55, 7.86) * mm});
            skLineSegment(sketch, "E2240", {"start": v(34.55, 7.86) * mm, "end": v(34.63, 7.76) * mm});
            skLineSegment(sketch, "E2241", {"start": v(34.63, 7.76) * mm, "end": v(34.7, 7.65) * mm});
            skLineSegment(sketch, "E2242", {"start": v(34.7, 7.65) * mm, "end": v(34.76, 7.54) * mm});
            skLineSegment(sketch, "E2243", {"start": v(34.76, 7.54) * mm, "end": v(34.8, 7.42) * mm});
            skLineSegment(sketch, "E2244", {"start": v(34.8, 7.42) * mm, "end": v(34.85, 7.3) * mm});
            skLineSegment(sketch, "E2245", {"start": v(34.85, 7.3) * mm, "end": v(34.87, 7.15) * mm});
            skLineSegment(sketch, "E2246", {"start": v(34.87, 7.15) * mm, "end": v(34.89, 7) * mm});
            skLineSegment(sketch, "E2247", {"start": v(34.89, 7) * mm, "end": v(34.9, 6.84) * mm});
            skLineSegment(sketch, "E2248", {"start": v(34.9, 6.84) * mm, "end": v(34.9, 6.69) * mm});
            skLineSegment(sketch, "E2249", {"start": v(34.9, 6.69) * mm, "end": v(34.88, 6.54) * mm});
            skLineSegment(sketch, "E2250", {"start": v(34.88, 6.54) * mm, "end": v(34.85, 6.4) * mm});
            skLineSegment(sketch, "E2251", {"start": v(34.85, 6.4) * mm, "end": v(34.82, 6.27) * mm});
            skLineSegment(sketch, "E2252", {"start": v(34.82, 6.27) * mm, "end": v(34.77, 6.14) * mm});
            skLineSegment(sketch, "E2253", {"start": v(34.77, 6.14) * mm, "end": v(34.72, 6.02) * mm});
            skLineSegment(sketch, "E2254", {"start": v(34.72, 6.02) * mm, "end": v(34.66, 5.91) * mm});
            skLineSegment(sketch, "E2255", {"start": v(34.66, 5.91) * mm, "end": v(34.59, 5.8) * mm});
            skLineSegment(sketch, "E2256", {"start": v(34.59, 5.8) * mm, "end": v(34.51, 5.72) * mm});
            skLineSegment(sketch, "E2257", {"start": v(34.51, 5.72) * mm, "end": v(34.44, 5.64) * mm});
            skLineSegment(sketch, "E2258", {"start": v(34.44, 5.64) * mm, "end": v(34.36, 5.58) * mm});
            skLineSegment(sketch, "E2259", {"start": v(34.36, 5.58) * mm, "end": v(34.27, 5.53) * mm});
            skLineSegment(sketch, "E2260", {"start": v(34.27, 5.53) * mm, "end": v(34.19, 5.5) * mm});
            skLineSegment(sketch, "E2261", {"start": v(34.19, 5.5) * mm, "end": v(34.1, 5.47) * mm});
            skLineSegment(sketch, "E2262", {"start": v(34.1, 5.47) * mm, "end": v(34, 5.45) * mm});
            skLineSegment(sketch, "E2263", {"start": v(34, 5.45) * mm, "end": v(33.91, 5.44) * mm});
            skLineSegment(sketch, "E2264", {"start": v(33.91, 5.44) * mm, "end": v(33.63, 5.44) * mm});
            skLineSegment(sketch, "E2265", {"start": v(33.63, 5.44) * mm, "end": v(33.34, 5.44) * mm});
            skLineSegment(sketch, "E2266", {"start": v(33.34, 5.44) * mm, "end": v(33.06, 5.44) * mm});
            skLineSegment(sketch, "E2267", {"start": v(33.06, 5.44) * mm, "end": v(32.77, 5.44) * mm});
            skLineSegment(sketch, "E2268", {"start": v(32.77, 5.44) * mm, "end": v(32.49, 5.44) * mm});
            skLineSegment(sketch, "E2269", {"start": v(32.49, 5.44) * mm, "end": v(32.2, 5.44) * mm});
            skLineSegment(sketch, "E2270", {"start": v(32.2, 5.44) * mm, "end": v(31.91, 5.44) * mm});
            skLineSegment(sketch, "E2271", {"start": v(31.91, 5.44) * mm, "end": v(31.63, 5.44) * mm});
            skLineSegment(sketch, "E2272", {"start": v(31.63, 5.44) * mm, "end": v(31.63, 5.79) * mm});
            skLineSegment(sketch, "E2273", {"start": v(31.63, 5.79) * mm, "end": v(31.63, 6.13) * mm});
            skLineSegment(sketch, "E2274", {"start": v(31.63, 6.13) * mm, "end": v(31.63, 6.48) * mm});
            skLineSegment(sketch, "E2275", {"start": v(31.63, 6.48) * mm, "end": v(31.63, 6.82) * mm});
            skLineSegment(sketch, "E2276", {"start": v(31.63, 6.82) * mm, "end": v(31.63, 7.16) * mm});
            skLineSegment(sketch, "E2277", {"start": v(31.63, 7.16) * mm, "end": v(31.63, 7.5) * mm});
            skLineSegment(sketch, "E2278", {"start": v(31.63, 7.5) * mm, "end": v(31.63, 7.85) * mm});
            skLineSegment(sketch, "E2279", {"start": v(31.63, 7.85) * mm, "end": v(31.63, 8.2) * mm});
            skLineSegment(sketch, "E2280", {"start": v(31.63, 2.66) * mm, "end": v(31.81, 2.66) * mm});
            skLineSegment(sketch, "E2281", {"start": v(31.81, 2.66) * mm, "end": v(32, 2.66) * mm});
            skLineSegment(sketch, "E2282", {"start": v(32, 2.66) * mm, "end": v(32.18, 2.66) * mm});
            skLineSegment(sketch, "E2283", {"start": v(32.18, 2.66) * mm, "end": v(32.36, 2.66) * mm});
            skLineSegment(sketch, "E2284", {"start": v(32.36, 2.66) * mm, "end": v(32.54, 2.66) * mm});
            skLineSegment(sketch, "E2285", {"start": v(32.54, 2.66) * mm, "end": v(32.72, 2.66) * mm});
            skLineSegment(sketch, "E2286", {"start": v(32.72, 2.66) * mm, "end": v(32.9, 2.66) * mm});
            skLineSegment(sketch, "E2287", {"start": v(32.9, 2.66) * mm, "end": v(33.09, 2.66) * mm});
            skLineSegment(sketch, "E2288", {"start": v(33.09, 2.66) * mm, "end": v(33.35, 2.22) * mm});
            skLineSegment(sketch, "E2289", {"start": v(33.35, 2.22) * mm, "end": v(33.6, 1.78) * mm});
            skLineSegment(sketch, "E2290", {"start": v(33.6, 1.78) * mm, "end": v(33.87, 1.35) * mm});
            skLineSegment(sketch, "E2291", {"start": v(33.87, 1.35) * mm, "end": v(34.12, 0.91) * mm});
            skLineSegment(sketch, "E2292", {"start": v(34.12, 0.91) * mm, "end": v(34.38, 0.47) * mm});
            skLineSegment(sketch, "E2293", {"start": v(34.38, 0.47) * mm, "end": v(34.64, 0.04) * mm});
            skLineSegment(sketch, "E2294", {"start": v(34.64, 0.04) * mm, "end": v(34.9, -0.4) * mm});
            skLineSegment(sketch, "E2295", {"start": v(34.9, -0.4) * mm, "end": v(35.16, -0.83) * mm});
            skLineSegment(sketch, "E2296", {"start": v(35.16, -0.83) * mm, "end": v(34.72, -0.83) * mm});
            skLineSegment(sketch, "E2297", {"start": v(34.72, -0.83) * mm, "end": v(34.28, -0.83) * mm});
            skLineSegment(sketch, "E2298", {"start": v(34.28, -0.83) * mm, "end": v(33.83, -0.83) * mm});
            skLineSegment(sketch, "E2299", {"start": v(33.83, -0.83) * mm, "end": v(33.4, -0.83) * mm});
            skLineSegment(sketch, "E2300", {"start": v(33.4, -0.83) * mm, "end": v(32.95, -0.83) * mm});
            skLineSegment(sketch, "E2301", {"start": v(32.95, -0.83) * mm, "end": v(32.51, -0.83) * mm});
            skLineSegment(sketch, "E2302", {"start": v(32.51, -0.83) * mm, "end": v(32.07, -0.83) * mm});
            skLineSegment(sketch, "E2303", {"start": v(32.07, -0.83) * mm, "end": v(31.63, -0.83) * mm});
            skLineSegment(sketch, "E2304", {"start": v(31.63, -0.83) * mm, "end": v(31.63, -0.4) * mm});
            skLineSegment(sketch, "E2305", {"start": v(31.63, -0.4) * mm, "end": v(31.63, 0.04) * mm});
            skLineSegment(sketch, "E2306", {"start": v(31.63, 0.04) * mm, "end": v(31.63, 0.47) * mm});
            skLineSegment(sketch, "E2307", {"start": v(31.63, 0.47) * mm, "end": v(31.63, 0.91) * mm});
            skLineSegment(sketch, "E2308", {"start": v(31.63, 0.91) * mm, "end": v(31.63, 1.35) * mm});
            skLineSegment(sketch, "E2309", {"start": v(31.63, 1.35) * mm, "end": v(31.63, 1.78) * mm});
            skLineSegment(sketch, "E2310", {"start": v(31.63, 1.78) * mm, "end": v(31.63, 2.22) * mm});
            skLineSegment(sketch, "E2311", {"start": v(31.63, 2.22) * mm, "end": v(31.63, 2.66) * mm});
            skLineSegment(sketch, "E2312", {"start": v(-25.7, 3.72) * mm, "end": v(-25.16, 3.72) * mm});
            skLineSegment(sketch, "E2313", {"start": v(-25.16, 3.72) * mm, "end": v(-24.62, 3.72) * mm});
            skLineSegment(sketch, "E2314", {"start": v(-24.62, 3.72) * mm, "end": v(-24.08, 3.72) * mm});
            skLineSegment(sketch, "E2315", {"start": v(-24.08, 3.72) * mm, "end": v(-23.55, 3.72) * mm});
            skLineSegment(sketch, "E2316", {"start": v(-23.55, 3.72) * mm, "end": v(-23, 3.72) * mm});
            skLineSegment(sketch, "E2317", {"start": v(-23, 3.72) * mm, "end": v(-22.47, 3.72) * mm});
            skLineSegment(sketch, "E2318", {"start": v(-22.47, 3.72) * mm, "end": v(-21.93, 3.72) * mm});
            skLineSegment(sketch, "E2319", {"start": v(-21.93, 3.72) * mm, "end": v(-21.4, 3.72) * mm});
            skLineSegment(sketch, "E2320", {"start": v(-21.4, 3.72) * mm, "end": v(-21.4, 3.15) * mm});
            skLineSegment(sketch, "E2321", {"start": v(-21.4, 3.15) * mm, "end": v(-21.4, 2.58) * mm});
            skLineSegment(sketch, "E2322", {"start": v(-21.4, 2.58) * mm, "end": v(-21.4, 2) * mm});
            skLineSegment(sketch, "E2323", {"start": v(-21.4, 2) * mm, "end": v(-21.4, 1.44) * mm});
            skLineSegment(sketch, "E2324", {"start": v(-21.4, 1.44) * mm, "end": v(-21.4, 0.87) * mm});
            skLineSegment(sketch, "E2325", {"start": v(-21.4, 0.87) * mm, "end": v(-21.4, 0.3) * mm});
            skLineSegment(sketch, "E2326", {"start": v(-21.4, 0.3) * mm, "end": v(-21.4, -0.27) * mm});
            skLineSegment(sketch, "E2327", {"start": v(-21.4, -0.27) * mm, "end": v(-21.4, -0.83) * mm});
            skLineSegment(sketch, "E2328", {"start": v(-21.4, -0.83) * mm, "end": v(-21.93, -0.83) * mm});
            skLineSegment(sketch, "E2329", {"start": v(-21.93, -0.83) * mm, "end": v(-22.47, -0.83) * mm});
            skLineSegment(sketch, "E2330", {"start": v(-22.47, -0.83) * mm, "end": v(-23, -0.83) * mm});
            skLineSegment(sketch, "E2331", {"start": v(-23, -0.83) * mm, "end": v(-23.55, -0.83) * mm});
            skLineSegment(sketch, "E2332", {"start": v(-23.55, -0.83) * mm, "end": v(-24.08, -0.83) * mm});
            skLineSegment(sketch, "E2333", {"start": v(-24.08, -0.83) * mm, "end": v(-24.62, -0.83) * mm});
            skLineSegment(sketch, "E2334", {"start": v(-24.62, -0.83) * mm, "end": v(-25.16, -0.83) * mm});
            skLineSegment(sketch, "E2335", {"start": v(-25.16, -0.83) * mm, "end": v(-25.7, -0.83) * mm});
            skLineSegment(sketch, "E2336", {"start": v(-25.7, -0.83) * mm, "end": v(-25.7, -0.27) * mm});
            skLineSegment(sketch, "E2337", {"start": v(-25.7, -0.27) * mm, "end": v(-25.7, 0.3) * mm});
            skLineSegment(sketch, "E2338", {"start": v(-25.7, 0.3) * mm, "end": v(-25.7, 0.87) * mm});
            skLineSegment(sketch, "E2339", {"start": v(-25.7, 0.87) * mm, "end": v(-25.7, 1.44) * mm});
            skLineSegment(sketch, "E2340", {"start": v(-25.7, 1.44) * mm, "end": v(-25.7, 2) * mm});
            skLineSegment(sketch, "E2341", {"start": v(-25.7, 2) * mm, "end": v(-25.7, 2.58) * mm});
            skLineSegment(sketch, "E2342", {"start": v(-25.7, 2.58) * mm, "end": v(-25.7, 3.15) * mm});
            skLineSegment(sketch, "E2343", {"start": v(-25.7, 3.15) * mm, "end": v(-25.7, 3.72) * mm});
            skLineSegment(sketch, "E2344", {"start": v(-69, 3.13) * mm, "end": v(-68.8, 2.64) * mm});
            skLineSegment(sketch, "E2345", {"start": v(-68.8, 2.64) * mm, "end": v(-68.6, 2.14) * mm});
            skLineSegment(sketch, "E2346", {"start": v(-68.6, 2.14) * mm, "end": v(-68.4, 1.65) * mm});
            skLineSegment(sketch, "E2347", {"start": v(-68.4, 1.65) * mm, "end": v(-68.2, 1.15) * mm});
            skLineSegment(sketch, "E2348", {"start": v(-68.2, 1.15) * mm, "end": v(-68, 0.65) * mm});
            skLineSegment(sketch, "E2349", {"start": v(-68, 0.65) * mm, "end": v(-67.8, 0.16) * mm});
            skLineSegment(sketch, "E2350", {"start": v(-67.8, 0.16) * mm, "end": v(-67.6, -0.34) * mm});
            skLineSegment(sketch, "E2351", {"start": v(-67.6, -0.34) * mm, "end": v(-67.39, -0.83) * mm});
            skLineSegment(sketch, "E2352", {"start": v(-67.39, -0.83) * mm, "end": v(-67.8, -0.83) * mm});
            skLineSegment(sketch, "E2353", {"start": v(-67.8, -0.83) * mm, "end": v(-68.2, -0.83) * mm});
            skLineSegment(sketch, "E2354", {"start": v(-68.2, -0.83) * mm, "end": v(-68.6, -0.83) * mm});
            skLineSegment(sketch, "E2355", {"start": v(-68.6, -0.83) * mm, "end": v(-69, -0.83) * mm});
            skLineSegment(sketch, "E2356", {"start": v(-69, -0.83) * mm, "end": v(-69.4, -0.83) * mm});
            skLineSegment(sketch, "E2357", {"start": v(-69.4, -0.83) * mm, "end": v(-69.8, -0.83) * mm});
            skLineSegment(sketch, "E2358", {"start": v(-69.8, -0.83) * mm, "end": v(-70.2, -0.83) * mm});
            skLineSegment(sketch, "E2359", {"start": v(-70.2, -0.83) * mm, "end": v(-70.6, -0.83) * mm});
            skLineSegment(sketch, "E2360", {"start": v(-70.6, -0.83) * mm, "end": v(-70.4, -0.34) * mm});
            skLineSegment(sketch, "E2361", {"start": v(-70.4, -0.34) * mm, "end": v(-70.2, 0.16) * mm});
            skLineSegment(sketch, "E2362", {"start": v(-70.2, 0.16) * mm, "end": v(-70, 0.65) * mm});
            skLineSegment(sketch, "E2363", {"start": v(-70, 0.65) * mm, "end": v(-69.8, 1.15) * mm});
            skLineSegment(sketch, "E2364", {"start": v(-69.8, 1.15) * mm, "end": v(-69.6, 1.65) * mm});
            skLineSegment(sketch, "E2365", {"start": v(-69.6, 1.65) * mm, "end": v(-69.4, 2.14) * mm});
            skLineSegment(sketch, "E2366", {"start": v(-69.4, 2.14) * mm, "end": v(-69.2, 2.64) * mm});
            skLineSegment(sketch, "E2367", {"start": v(-69.2, 2.64) * mm, "end": v(-69, 3.13) * mm});
            skLineSegment(sketch, "E2368", {"start": v(79.84, -8.7) * mm, "end": v(59.88, -8.7) * mm});
            skLineSegment(sketch, "E2369", {"start": v(59.88, -8.7) * mm, "end": v(39.92, -8.7) * mm});
            skLineSegment(sketch, "E2370", {"start": v(39.92, -8.7) * mm, "end": v(19.96, -8.7) * mm});
            skLineSegment(sketch, "E2371", {"start": v(19.96, -8.7) * mm, "end": v(0, -8.7) * mm});
            skLineSegment(sketch, "E2372", {"start": v(0, -8.7) * mm, "end": v(-19.96, -8.7) * mm});
            skLineSegment(sketch, "E2373", {"start": v(-19.96, -8.7) * mm, "end": v(-39.92, -8.7) * mm});
            skLineSegment(sketch, "E2374", {"start": v(-39.92, -8.7) * mm, "end": v(-59.88, -8.7) * mm});
            skLineSegment(sketch, "E2375", {"start": v(-59.88, -8.7) * mm, "end": v(-79.84, -8.7) * mm});
            skLineSegment(sketch, "E2376", {"start": v(-79.84, -8.7) * mm, "end": v(-80.39, -8.65) * mm});
            skLineSegment(sketch, "E2377", {"start": v(-80.39, -8.65) * mm, "end": v(-80.9, -8.49) * mm});
            skLineSegment(sketch, "E2378", {"start": v(-80.9, -8.49) * mm, "end": v(-81.36, -8.24) * mm});
            skLineSegment(sketch, "E2379", {"start": v(-81.36, -8.24) * mm, "end": v(-81.77, -7.9) * mm});
            skLineSegment(sketch, "E2380", {"start": v(-81.77, -7.9) * mm, "end": v(-82.1, -7.5) * mm});
            skLineSegment(sketch, "E2381", {"start": v(-82.1, -7.5) * mm, "end": v(-82.35, -7.04) * mm});
            skLineSegment(sketch, "E2382", {"start": v(-82.35, -7.04) * mm, "end": v(-82.51, -6.53) * mm});
            skLineSegment(sketch, "E2383", {"start": v(-82.51, -6.53) * mm, "end": v(-82.57, -5.99) * mm});
            skLineSegment(sketch, "E2384", {"start": v(-82.57, -5.99) * mm, "end": v(-82.51, -5.44) * mm});
            skLineSegment(sketch, "E2385", {"start": v(-82.51, -5.44) * mm, "end": v(-82.35, -4.93) * mm});
            skLineSegment(sketch, "E2386", {"start": v(-82.35, -4.93) * mm, "end": v(-82.1, -4.47) * mm});
            skLineSegment(sketch, "E2387", {"start": v(-82.1, -4.47) * mm, "end": v(-81.77, -4.06) * mm});
            skLineSegment(sketch, "E2388", {"start": v(-81.77, -4.06) * mm, "end": v(-81.36, -3.73) * mm});
            skLineSegment(sketch, "E2389", {"start": v(-81.36, -3.73) * mm, "end": v(-80.9, -3.48) * mm});
            skLineSegment(sketch, "E2390", {"start": v(-80.9, -3.48) * mm, "end": v(-80.39, -3.32) * mm});
            skLineSegment(sketch, "E2391", {"start": v(-80.39, -3.32) * mm, "end": v(-79.84, -3.27) * mm});
            skLineSegment(sketch, "E2392", {"start": v(-79.84, -3.27) * mm, "end": v(-59.88, -3.27) * mm});
            skLineSegment(sketch, "E2393", {"start": v(-59.88, -3.27) * mm, "end": v(-39.92, -3.27) * mm});
            skLineSegment(sketch, "E2394", {"start": v(-39.92, -3.27) * mm, "end": v(-19.96, -3.27) * mm});
            skLineSegment(sketch, "E2395", {"start": v(-19.96, -3.27) * mm, "end": v(0, -3.27) * mm});
            skLineSegment(sketch, "E2396", {"start": v(0, -3.27) * mm, "end": v(19.96, -3.27) * mm});
            skLineSegment(sketch, "E2397", {"start": v(19.96, -3.27) * mm, "end": v(39.92, -3.27) * mm});
            skLineSegment(sketch, "E2398", {"start": v(39.92, -3.27) * mm, "end": v(59.88, -3.27) * mm});
            skLineSegment(sketch, "E2399", {"start": v(59.88, -3.27) * mm, "end": v(79.84, -3.27) * mm});
            skLineSegment(sketch, "E2400", {"start": v(79.84, -3.27) * mm, "end": v(80.39, -3.32) * mm});
            skLineSegment(sketch, "E2401", {"start": v(80.39, -3.32) * mm, "end": v(80.9, -3.48) * mm});
            skLineSegment(sketch, "E2402", {"start": v(80.9, -3.48) * mm, "end": v(81.36, -3.73) * mm});
            skLineSegment(sketch, "E2403", {"start": v(81.36, -3.73) * mm, "end": v(81.77, -4.06) * mm});
            skLineSegment(sketch, "E2404", {"start": v(81.77, -4.06) * mm, "end": v(82.1, -4.47) * mm});
            skLineSegment(sketch, "E2405", {"start": v(82.1, -4.47) * mm, "end": v(82.35, -4.93) * mm});
            skLineSegment(sketch, "E2406", {"start": v(82.35, -4.93) * mm, "end": v(82.51, -5.44) * mm});
            skLineSegment(sketch, "E2407", {"start": v(82.51, -5.44) * mm, "end": v(82.57, -5.99) * mm});
            skLineSegment(sketch, "E2408", {"start": v(82.57, -5.99) * mm, "end": v(82.51, -6.53) * mm});
            skLineSegment(sketch, "E2409", {"start": v(82.51, -6.53) * mm, "end": v(82.35, -7.04) * mm});
            skLineSegment(sketch, "E2410", {"start": v(82.35, -7.04) * mm, "end": v(82.1, -7.5) * mm});
            skLineSegment(sketch, "E2411", {"start": v(82.1, -7.5) * mm, "end": v(81.77, -7.9) * mm});
            skLineSegment(sketch, "E2412", {"start": v(81.77, -7.9) * mm, "end": v(81.36, -8.24) * mm});
            skLineSegment(sketch, "E2413", {"start": v(81.36, -8.24) * mm, "end": v(80.9, -8.49) * mm});
            skLineSegment(sketch, "E2414", {"start": v(80.9, -8.49) * mm, "end": v(80.39, -8.65) * mm});
            skLineSegment(sketch, "E2415", {"start": v(80.39, -8.65) * mm, "end": v(79.84, -8.7) * mm});
            skSolve(sketch);
        }
        {
            var Q0;
            Q0=makeQuery(id+"F0.imprint","IMPRINT",FACE,{"disambiguationData":[TD([[makeQuery(id+"F0.imprint","IMPRINT",EDGE,{"derivedFrom":sQuery(id+"F0.wireOp",EDGE,"E0")}),1.0]])]});
            extrude(context, id + "F1", {"entities" : qUnion([Q0]), "depth" : 8 * mm});
        }
        {
            var Q0;
            Q0=makeQuery(id+"F0.imprint","IMPRINT",FACE,{"disambiguationData":[TD([[makeQuery(id+"F0.imprint","IMPRINT",EDGE,{"derivedFrom":sQuery(id+"F0.wireOp",EDGE,"E2200")}),-1.0]])]});
            extrude(context, id + "F2", {"entities" : qUnion([Q0]), "operationType" : NewBodyOperationType.ADD, "depth" : 8 * mm});
        }
        {
            var Q0;
            Q0=makeQuery(id+"F0.imprint","IMPRINT",FACE,{"disambiguationData":[TD([[makeQuery(id+"F0.imprint","IMPRINT",EDGE,{"derivedFrom":sQuery(id+"F0.wireOp",EDGE,"E2368")}),-1.0]])]});
            extrude(context, id + "F3", {"entities" : qUnion([Q0]), "operationType" : NewBodyOperationType.ADD, "depth" : 1 * mm});
        }
    });
